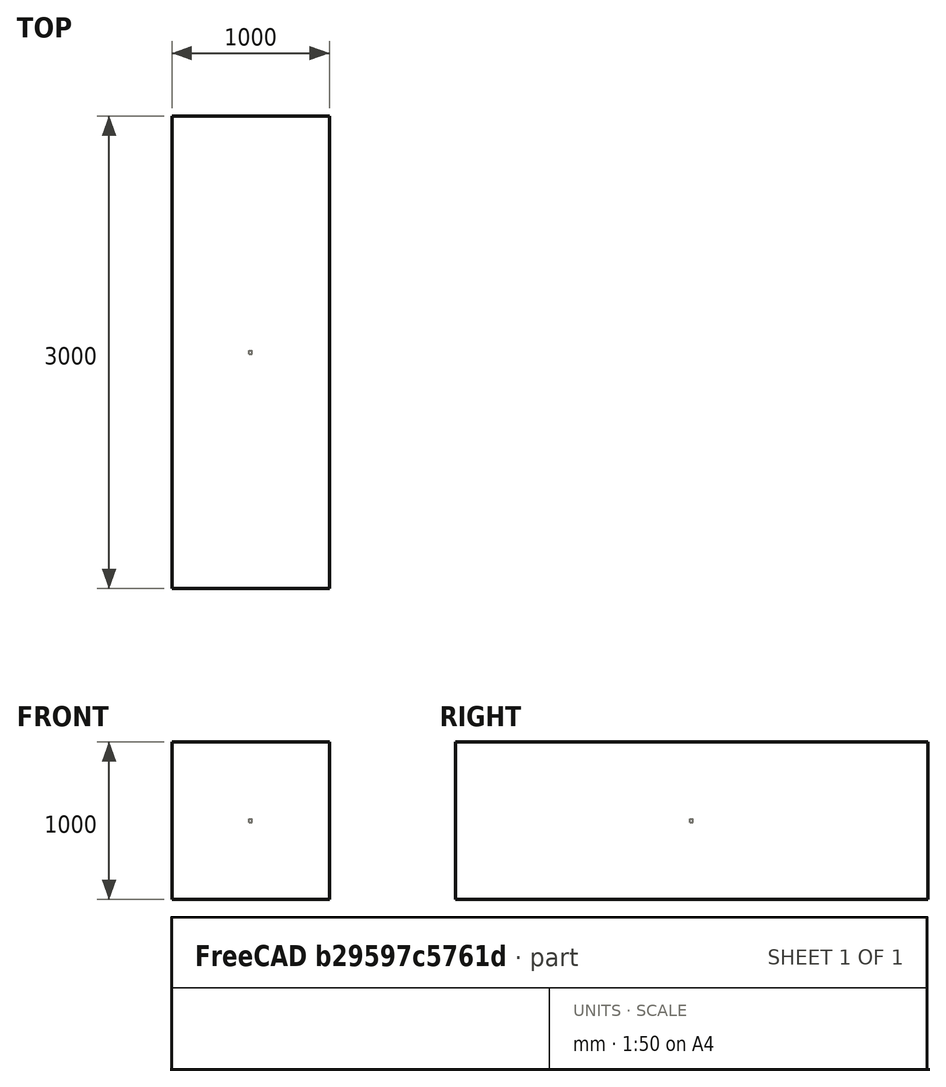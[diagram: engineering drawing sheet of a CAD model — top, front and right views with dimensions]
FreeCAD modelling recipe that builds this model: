
FCSTD DOCUMENT  (FreeCAD 1.0R39109 (Git))
Label: BeamDumpGDML
License: All rights reserved
LicenseURL: https://en.wikipedia.org/wiki/All_rights_reserved
objects: App::DocumentObjectGroupPython×1252, Part::FeaturePython×3, App::Part×3, Spreadsheet::Sheet×2
note: 2 computed .brp shape members not serialized (recipe doc carries the construction recipe); baked Part::Feature solids carry a one-line shape summary decoded from their .brp

FEATURE [Spreadsheet::Sheet] defines
  cells = A1='constant; B1='HALFPI; C1(HALFPI)==pi / 2; A2='constant; B2='PI; C2(PI)==1 * pi; A3='constant; B3='TWOPI; C3(TWOPI)==2 * pi
FEATURE [Spreadsheet::Sheet] gdmlInfo
FEATURE [App::DocumentObjectGroupPython] Define  # scripted group (container) (typed FeaturePython)
  Group = -> [defines,gdmlInfo]
FEATURE [App::DocumentObjectGroupPython] HALFPI  # scripted group (container) (typed FeaturePython)
  name = HALFPI
  value = pi/2.
FEATURE [App::DocumentObjectGroupPython] PI  # scripted group (container) (typed FeaturePython)
  name = PI
  value = 1.*pi
FEATURE [App::DocumentObjectGroupPython] TWOPI  # scripted group (container) (typed FeaturePython)
  name = TWOPI
  value = 2.*pi
FEATURE [App::DocumentObjectGroupPython] Constants  # scripted group (container) (typed FeaturePython)
  Group = -> [HALFPI,PI,TWOPI]
FEATURE [App::DocumentObjectGroupPython] Quantities  # scripted group (container) (typed FeaturePython)
FEATURE [App::DocumentObjectGroupPython] Variables  # scripted group (container) (typed FeaturePython)
FEATURE [App::DocumentObjectGroupPython] Isotopes  # scripted group (container) (typed FeaturePython)
FEATURE [App::DocumentObjectGroupPython] Elements  # scripted group (container) (typed FeaturePython)
FEATURE [App::DocumentObjectGroupPython] Matrix  # scripted group (container) (typed FeaturePython)
FEATURE [App::DocumentObjectGroupPython] Surfaces  # scripted group (container) (typed FeaturePython)
FEATURE [App::DocumentObjectGroupPython] Opticals  # scripted group (container) (typed FeaturePython)
  Group = -> [Matrix,Surfaces]
FEATURE [App::DocumentObjectGroupPython] G4Isotopes  # scripted group (container) (typed FeaturePython)
FEATURE [App::DocumentObjectGroupPython] H_element  # scripted group (container) (typed FeaturePython)
  Z = 1
  atom_value = 1.008
  formula = H
  name = H_element
FEATURE [App::DocumentObjectGroupPython] He_element  # scripted group (container) (typed FeaturePython)
  Z = 2
  atom_value = 4.0026
  formula = He
  name = He_element
FEATURE [App::DocumentObjectGroupPython] Li_element  # scripted group (container) (typed FeaturePython)
  Z = 3
  atom_value = 6.94
  formula = Li
  name = Li_element
FEATURE [App::DocumentObjectGroupPython] Be_element  # scripted group (container) (typed FeaturePython)
  Z = 4
  atom_value = 9.01218
  formula = Be
  name = Be_element
FEATURE [App::DocumentObjectGroupPython] B_element  # scripted group (container) (typed FeaturePython)
  Z = 5
  atom_value = 10.81
  formula = B
  name = B_element
FEATURE [App::DocumentObjectGroupPython] C_element  # scripted group (container) (typed FeaturePython)
  Z = 6
  atom_value = 12.011
  formula = C
  name = C_element
FEATURE [App::DocumentObjectGroupPython] N_element  # scripted group (container) (typed FeaturePython)
  Z = 7
  atom_value = 14.007
  formula = N
  name = N_element
FEATURE [App::DocumentObjectGroupPython] O_element  # scripted group (container) (typed FeaturePython)
  Z = 8
  atom_value = 15.999
  formula = O
  name = O_element
FEATURE [App::DocumentObjectGroupPython] F_element  # scripted group (container) (typed FeaturePython)
  Z = 9
  atom_value = 18.9984
  formula = F
  name = F_element
FEATURE [App::DocumentObjectGroupPython] Ne_element  # scripted group (container) (typed FeaturePython)
  Z = 10
  atom_value = 20.1797
  formula = Ne
  name = Ne_element
FEATURE [App::DocumentObjectGroupPython] Na_element  # scripted group (container) (typed FeaturePython)
  Z = 11
  atom_value = 22.9898
  formula = Na
  name = Na_element
FEATURE [App::DocumentObjectGroupPython] Mg_element  # scripted group (container) (typed FeaturePython)
  Z = 12
  atom_value = 24.305
  formula = Mg
  name = Mg_element
FEATURE [App::DocumentObjectGroupPython] Al_element  # scripted group (container) (typed FeaturePython)
  Z = 13
  atom_value = 26.9815
  formula = Al
  name = Al_element
FEATURE [App::DocumentObjectGroupPython] Si_element  # scripted group (container) (typed FeaturePython)
  Z = 14
  atom_value = 28.085
  formula = Si
  name = Si_element
FEATURE [App::DocumentObjectGroupPython] P_element  # scripted group (container) (typed FeaturePython)
  Z = 15
  atom_value = 30.9738
  formula = P
  name = P_element
FEATURE [App::DocumentObjectGroupPython] S_element  # scripted group (container) (typed FeaturePython)
  Z = 16
  atom_value = 32.06
  formula = S
  name = S_element
FEATURE [App::DocumentObjectGroupPython] Cl_element  # scripted group (container) (typed FeaturePython)
  Z = 17
  atom_value = 35.45
  formula = Cl
  name = Cl_element
FEATURE [App::DocumentObjectGroupPython] Ar_element  # scripted group (container) (typed FeaturePython)
  Z = 18
  atom_value = 39.95
  formula = Ar
  name = Ar_element
FEATURE [App::DocumentObjectGroupPython] K_element  # scripted group (container) (typed FeaturePython)
  Z = 19
  atom_value = 39.0983
  formula = K
  name = K_element
FEATURE [App::DocumentObjectGroupPython] Ca_element  # scripted group (container) (typed FeaturePython)
  Z = 20
  atom_value = 40.078
  formula = Ca
  name = Ca_element
FEATURE [App::DocumentObjectGroupPython] Sc_element  # scripted group (container) (typed FeaturePython)
  Z = 21
  atom_value = 44.9559
  formula = Sc
  name = Sc_element
FEATURE [App::DocumentObjectGroupPython] Ti_element  # scripted group (container) (typed FeaturePython)
  Z = 22
  atom_value = 47.867
  formula = Ti
  name = Ti_element
FEATURE [App::DocumentObjectGroupPython] V_element  # scripted group (container) (typed FeaturePython)
  Z = 23
  atom_value = 50.9415
  formula = V
  name = V_element
FEATURE [App::DocumentObjectGroupPython] Cr_element  # scripted group (container) (typed FeaturePython)
  Z = 24
  atom_value = 51.9961
  formula = Cr
  name = Cr_element
FEATURE [App::DocumentObjectGroupPython] Mn_element  # scripted group (container) (typed FeaturePython)
  Z = 25
  atom_value = 54.938
  formula = Mn
  name = Mn_element
FEATURE [App::DocumentObjectGroupPython] Fe_element  # scripted group (container) (typed FeaturePython)
  Z = 26
  atom_value = 55.845
  formula = Fe
  name = Fe_element
FEATURE [App::DocumentObjectGroupPython] Co_element  # scripted group (container) (typed FeaturePython)
  Z = 27
  atom_value = 58.9332
  formula = Co
  name = Co_element
FEATURE [App::DocumentObjectGroupPython] Ni_element  # scripted group (container) (typed FeaturePython)
  Z = 28
  atom_value = 58.6934
  formula = Ni
  name = Ni_element
FEATURE [App::DocumentObjectGroupPython] Cu_element  # scripted group (container) (typed FeaturePython)
  Z = 29
  atom_value = 63.546
  formula = Cu
  name = Cu_element
FEATURE [App::DocumentObjectGroupPython] Zn_element  # scripted group (container) (typed FeaturePython)
  Z = 30
  atom_value = 65.38
  formula = Zn
  name = Zn_element
FEATURE [App::DocumentObjectGroupPython] Ga_element  # scripted group (container) (typed FeaturePython)
  Z = 31
  atom_value = 69.723
  formula = Ga
  name = Ga_element
FEATURE [App::DocumentObjectGroupPython] Ge_element  # scripted group (container) (typed FeaturePython)
  Z = 32
  atom_value = 72.63
  formula = Ge
  name = Ge_element
FEATURE [App::DocumentObjectGroupPython] As_element  # scripted group (container) (typed FeaturePython)
  Z = 33
  atom_value = 74.9216
  formula = As
  name = As_element
FEATURE [App::DocumentObjectGroupPython] Se_element  # scripted group (container) (typed FeaturePython)
  Z = 34
  atom_value = 78.971
  formula = Se
  name = Se_element
FEATURE [App::DocumentObjectGroupPython] Br_element  # scripted group (container) (typed FeaturePython)
  Z = 35
  atom_value = 79.904
  formula = Br
  name = Br_element
FEATURE [App::DocumentObjectGroupPython] Kr_element  # scripted group (container) (typed FeaturePython)
  Z = 36
  atom_value = 83.798
  formula = Kr
  name = Kr_element
FEATURE [App::DocumentObjectGroupPython] Rb_element  # scripted group (container) (typed FeaturePython)
  Z = 37
  atom_value = 85.4678
  formula = Rb
  name = Rb_element
FEATURE [App::DocumentObjectGroupPython] Sr_element  # scripted group (container) (typed FeaturePython)
  Z = 38
  atom_value = 87.62
  formula = Sr
  name = Sr_element
FEATURE [App::DocumentObjectGroupPython] Y_element  # scripted group (container) (typed FeaturePython)
  Z = 39
  atom_value = 88.9058
  formula = Y
  name = Y_element
FEATURE [App::DocumentObjectGroupPython] Zr_element  # scripted group (container) (typed FeaturePython)
  Z = 40
  atom_value = 91.224
  formula = Zr
  name = Zr_element
FEATURE [App::DocumentObjectGroupPython] Nb_element  # scripted group (container) (typed FeaturePython)
  Z = 41
  atom_value = 92.9064
  formula = Nb
  name = Nb_element
FEATURE [App::DocumentObjectGroupPython] Mo_element  # scripted group (container) (typed FeaturePython)
  Z = 42
  atom_value = 95.95
  formula = Mo
  name = Mo_element
FEATURE [App::DocumentObjectGroupPython] Tc_element  # scripted group (container) (typed FeaturePython)
  Z = 43
  atom_value = 97
  formula = Tc
  name = Tc_element
FEATURE [App::DocumentObjectGroupPython] Ru_element  # scripted group (container) (typed FeaturePython)
  Z = 44
  atom_value = 101.07
  formula = Ru
  name = Ru_element
FEATURE [App::DocumentObjectGroupPython] Rh_element  # scripted group (container) (typed FeaturePython)
  Z = 45
  atom_value = 102.905
  formula = Rh
  name = Rh_element
FEATURE [App::DocumentObjectGroupPython] Pd_element  # scripted group (container) (typed FeaturePython)
  Z = 46
  atom_value = 106.42
  formula = Pd
  name = Pd_element
FEATURE [App::DocumentObjectGroupPython] Ag_element  # scripted group (container) (typed FeaturePython)
  Z = 47
  atom_value = 107.868
  formula = Ag
  name = Ag_element
FEATURE [App::DocumentObjectGroupPython] Cd_element  # scripted group (container) (typed FeaturePython)
  Z = 48
  atom_value = 112.414
  formula = Cd
  name = Cd_element
FEATURE [App::DocumentObjectGroupPython] In_element  # scripted group (container) (typed FeaturePython)
  Z = 49
  atom_value = 114.818
  formula = In
  name = In_element
FEATURE [App::DocumentObjectGroupPython] Sn_element  # scripted group (container) (typed FeaturePython)
  Z = 50
  atom_value = 118.71
  formula = Sn
  name = Sn_element
FEATURE [App::DocumentObjectGroupPython] Sb_element  # scripted group (container) (typed FeaturePython)
  Z = 51
  atom_value = 121.76
  formula = Sb
  name = Sb_element
FEATURE [App::DocumentObjectGroupPython] Te_element  # scripted group (container) (typed FeaturePython)
  Z = 52
  atom_value = 127.6
  formula = Te
  name = Te_element
FEATURE [App::DocumentObjectGroupPython] I_element  # scripted group (container) (typed FeaturePython)
  Z = 53
  atom_value = 126.904
  formula = I
  name = I_element
FEATURE [App::DocumentObjectGroupPython] Xe_element  # scripted group (container) (typed FeaturePython)
  Z = 54
  atom_value = 131.293
  formula = Xe
  name = Xe_element
FEATURE [App::DocumentObjectGroupPython] Cs_element  # scripted group (container) (typed FeaturePython)
  Z = 55
  atom_value = 132.905
  formula = Cs
  name = Cs_element
FEATURE [App::DocumentObjectGroupPython] Ba_element  # scripted group (container) (typed FeaturePython)
  Z = 56
  atom_value = 137.327
  formula = Ba
  name = Ba_element
FEATURE [App::DocumentObjectGroupPython] La_element  # scripted group (container) (typed FeaturePython)
  Z = 57
  atom_value = 138.905
  formula = La
  name = La_element
FEATURE [App::DocumentObjectGroupPython] Ce_element  # scripted group (container) (typed FeaturePython)
  Z = 58
  atom_value = 140.116
  formula = Ce
  name = Ce_element
FEATURE [App::DocumentObjectGroupPython] Pr_element  # scripted group (container) (typed FeaturePython)
  Z = 59
  atom_value = 140.908
  formula = Pr
  name = Pr_element
FEATURE [App::DocumentObjectGroupPython] Nd_element  # scripted group (container) (typed FeaturePython)
  Z = 60
  atom_value = 144.242
  formula = Nd
  name = Nd_element
FEATURE [App::DocumentObjectGroupPython] Pm_element  # scripted group (container) (typed FeaturePython)
  Z = 61
  atom_value = 145
  formula = Pm
  name = Pm_element
FEATURE [App::DocumentObjectGroupPython] Sm_element  # scripted group (container) (typed FeaturePython)
  Z = 62
  atom_value = 150.36
  formula = Sm
  name = Sm_element
FEATURE [App::DocumentObjectGroupPython] Eu_element  # scripted group (container) (typed FeaturePython)
  Z = 63
  atom_value = 151.964
  formula = Eu
  name = Eu_element
FEATURE [App::DocumentObjectGroupPython] Gd_element  # scripted group (container) (typed FeaturePython)
  Z = 64
  atom_value = 157.25
  formula = Gd
  name = Gd_element
FEATURE [App::DocumentObjectGroupPython] Tb_element  # scripted group (container) (typed FeaturePython)
  Z = 65
  atom_value = 158.925
  formula = Tb
  name = Tb_element
FEATURE [App::DocumentObjectGroupPython] Dy_element  # scripted group (container) (typed FeaturePython)
  Z = 66
  atom_value = 162.5
  formula = Dy
  name = Dy_element
FEATURE [App::DocumentObjectGroupPython] Ho_element  # scripted group (container) (typed FeaturePython)
  Z = 67
  atom_value = 164.93
  formula = Ho
  name = Ho_element
FEATURE [App::DocumentObjectGroupPython] Er_element  # scripted group (container) (typed FeaturePython)
  Z = 68
  atom_value = 167.259
  formula = Er
  name = Er_element
FEATURE [App::DocumentObjectGroupPython] Tm_element  # scripted group (container) (typed FeaturePython)
  Z = 69
  atom_value = 168.934
  formula = Tm
  name = Tm_element
FEATURE [App::DocumentObjectGroupPython] Yb_element  # scripted group (container) (typed FeaturePython)
  Z = 70
  atom_value = 173.045
  formula = Yb
  name = Yb_element
FEATURE [App::DocumentObjectGroupPython] Lu_element  # scripted group (container) (typed FeaturePython)
  Z = 71
  atom_value = 174.967
  formula = Lu
  name = Lu_element
FEATURE [App::DocumentObjectGroupPython] Hf_element  # scripted group (container) (typed FeaturePython)
  Z = 72
  atom_value = 178.49
  formula = Hf
  name = Hf_element
FEATURE [App::DocumentObjectGroupPython] Ta_element  # scripted group (container) (typed FeaturePython)
  Z = 73
  atom_value = 180.948
  formula = Ta
  name = Ta_element
FEATURE [App::DocumentObjectGroupPython] W_element  # scripted group (container) (typed FeaturePython)
  Z = 74
  atom_value = 183.84
  formula = W
  name = W_element
FEATURE [App::DocumentObjectGroupPython] Re_element  # scripted group (container) (typed FeaturePython)
  Z = 75
  atom_value = 186.207
  formula = Re
  name = Re_element
FEATURE [App::DocumentObjectGroupPython] Os_element  # scripted group (container) (typed FeaturePython)
  Z = 76
  atom_value = 190.23
  formula = Os
  name = Os_element
FEATURE [App::DocumentObjectGroupPython] Ir_element  # scripted group (container) (typed FeaturePython)
  Z = 77
  atom_value = 192.217
  formula = Ir
  name = Ir_element
FEATURE [App::DocumentObjectGroupPython] Pt_element  # scripted group (container) (typed FeaturePython)
  Z = 78
  atom_value = 195.084
  formula = Pt
  name = Pt_element
FEATURE [App::DocumentObjectGroupPython] Au_element  # scripted group (container) (typed FeaturePython)
  Z = 79
  atom_value = 196.967
  formula = Au
  name = Au_element
FEATURE [App::DocumentObjectGroupPython] Hg_element  # scripted group (container) (typed FeaturePython)
  Z = 80
  atom_value = 200.592
  formula = Hg
  name = Hg_element
FEATURE [App::DocumentObjectGroupPython] Tl_element  # scripted group (container) (typed FeaturePython)
  Z = 81
  atom_value = 204.38
  formula = Tl
  name = Tl_element
FEATURE [App::DocumentObjectGroupPython] Pb_element  # scripted group (container) (typed FeaturePython)
  Z = 82
  atom_value = 207.2
  formula = Pb
  name = Pb_element
FEATURE [App::DocumentObjectGroupPython] Bi_element  # scripted group (container) (typed FeaturePython)
  Z = 83
  atom_value = 208.98
  formula = Bi
  name = Bi_element
FEATURE [App::DocumentObjectGroupPython] Po_element  # scripted group (container) (typed FeaturePython)
  Z = 84
  atom_value = 209
  formula = Po
  name = Po_element
FEATURE [App::DocumentObjectGroupPython] At_element  # scripted group (container) (typed FeaturePython)
  Z = 85
  atom_value = 210
  formula = At
  name = At_element
FEATURE [App::DocumentObjectGroupPython] Rn_element  # scripted group (container) (typed FeaturePython)
  Z = 86
  atom_value = 222
  formula = Rn
  name = Rn_element
FEATURE [App::DocumentObjectGroupPython] Fr_element  # scripted group (container) (typed FeaturePython)
  Z = 87
  atom_value = 223
  formula = Fr
  name = Fr_element
FEATURE [App::DocumentObjectGroupPython] Ra_element  # scripted group (container) (typed FeaturePython)
  Z = 88
  atom_value = 226
  formula = Ra
  name = Ra_element
FEATURE [App::DocumentObjectGroupPython] Ac_element  # scripted group (container) (typed FeaturePython)
  Z = 89
  atom_value = 227
  formula = Ac
  name = Ac_element
FEATURE [App::DocumentObjectGroupPython] Th_element  # scripted group (container) (typed FeaturePython)
  Z = 90
  atom_value = 232.038
  formula = Th
  name = Th_element
FEATURE [App::DocumentObjectGroupPython] Pa_element  # scripted group (container) (typed FeaturePython)
  Z = 91
  atom_value = 231.036
  formula = Pa
  name = Pa_element
FEATURE [App::DocumentObjectGroupPython] U_element  # scripted group (container) (typed FeaturePython)
  Z = 92
  atom_value = 238.029
  formula = U
  name = U_element
FEATURE [App::DocumentObjectGroupPython] Np_element  # scripted group (container) (typed FeaturePython)
  Z = 93
  atom_value = 237
  formula = Np
  name = Np_element
FEATURE [App::DocumentObjectGroupPython] Pu_element  # scripted group (container) (typed FeaturePython)
  Z = 94
  atom_value = 244
  formula = Pu
  name = Pu_element
FEATURE [App::DocumentObjectGroupPython] Am_element  # scripted group (container) (typed FeaturePython)
  Z = 95
  atom_value = 243
  formula = Am
  name = Am_element
FEATURE [App::DocumentObjectGroupPython] Cm_element  # scripted group (container) (typed FeaturePython)
  Z = 96
  atom_value = 247
  formula = Cm
  name = Cm_element
FEATURE [App::DocumentObjectGroupPython] Bk_element  # scripted group (container) (typed FeaturePython)
  Z = 97
  atom_value = 247
  formula = Bk
  name = Bk_element
FEATURE [App::DocumentObjectGroupPython] Cf_element  # scripted group (container) (typed FeaturePython)
  Z = 98
  atom_value = 251
  formula = Cf
  name = Cf_element
FEATURE [App::DocumentObjectGroupPython] G4Elements  # scripted group (container) (typed FeaturePython)
  Group = -> [H_element,He_element,Li_element,Be_element,B_element,C_element,N_element,O_element,F_element,Ne_element,Na_element,Mg_element,Al_element,Si_element,P_element,S_element,Cl_element,Ar_element,K_element,Ca_element,Sc_element,Ti_element,V_element,Cr_element,Mn_element,Fe_element,Co_element,Ni_element,Cu_element,Zn_element,Ga_element,Ge_element,As_element,Se_element,Br_element,Kr_element,Rb_element,+61 more]
FEATURE [App::DocumentObjectGroupPython] H_element001  label="H_element : 0.101"  # scripted group (container) (typed FeaturePython)
  n = 0.101327
FEATURE [App::DocumentObjectGroupPython] C_element001  label="C_element : 0.775"  # scripted group (container) (typed FeaturePython)
  n = 0.7755
FEATURE [App::DocumentObjectGroupPython] N_element001  label="N_element : 0.035"  # scripted group (container) (typed FeaturePython)
  n = 0.035057
FEATURE [App::DocumentObjectGroupPython] O_element001  label="O_element : 0.052"  # scripted group (container) (typed FeaturePython)
  n = 0.0523159
FEATURE [App::DocumentObjectGroupPython] F_element001  label="F_element : 0.017"  # scripted group (container) (typed FeaturePython)
  n = 0.017422
FEATURE [App::DocumentObjectGroupPython] Ca_element001  label="Ca_element : 0.018"  # scripted group (container) (typed FeaturePython)
  n = 0.018378
FEATURE [App::DocumentObjectGroupPython] G4_A_150_TISSUE  label="G4_A-150_TISSUE"  # scripted group (container) (typed FeaturePython)
  Dunit = g/cm3
  Dvalue = 1.127
  Group = -> [H_element001,C_element001,N_element001,O_element001,F_element001,Ca_element001]
  conduct = 2
  density = 1
  expand = 3
  formula = G4_A-150_TISSUE
  name = G4_A-150_TISSUE
  specific = 4
FEATURE [App::DocumentObjectGroupPython] C_element002  label="C_element : 3"  # scripted group (container) (typed FeaturePython)
  n = 3
  ref = C_element
FEATURE [App::DocumentObjectGroupPython] H_element002  label="H_element : 6"  # scripted group (container) (typed FeaturePython)
  n = 6
  ref = H_element
FEATURE [App::DocumentObjectGroupPython] O_element002  label="O_element : 1"  # scripted group (container) (typed FeaturePython)
  n = 1
  ref = O_element
FEATURE [App::DocumentObjectGroupPython] G4_ACETONE  # scripted group (container) (typed FeaturePython)
  Dunit = g/cm3
  Dvalue = 0.7899
  Group = -> [C_element002,H_element002,O_element002]
  conduct = 2
  density = 1
  expand = 3
  formula = G4_ACETONE
  name = G4_ACETONE
  specific = 4
FEATURE [App::DocumentObjectGroupPython] C_element003  label="C_element : 2"  # scripted group (container) (typed FeaturePython)
  n = 2
  ref = C_element
FEATURE [App::DocumentObjectGroupPython] H_element003  label="H_element : 2"  # scripted group (container) (typed FeaturePython)
  n = 2
  ref = H_element
FEATURE [App::DocumentObjectGroupPython] G4_ACETYLENE  # scripted group (container) (typed FeaturePython)
  Dunit = g/cm3
  Dvalue = 0.0010967
  Group = -> [C_element003,H_element003]
  conduct = 2
  density = 1
  expand = 3
  formula = G4_ACETYLENE
  name = G4_ACETYLENE
  specific = 4
FEATURE [App::DocumentObjectGroupPython] C_element004  label="C_element : 5"  # scripted group (container) (typed FeaturePython)
  n = 5
  ref = C_element
FEATURE [App::DocumentObjectGroupPython] H_element004  label="H_element : 5"  # scripted group (container) (typed FeaturePython)
  n = 5
  ref = H_element
FEATURE [App::DocumentObjectGroupPython] N_element002  label="N_element : 5"  # scripted group (container) (typed FeaturePython)
  n = 5
  ref = N_element
FEATURE [App::DocumentObjectGroupPython] G4_ADENINE  # scripted group (container) (typed FeaturePython)
  Dunit = g/cm3
  Dvalue = 1.6
  Group = -> [C_element004,H_element004,N_element002]
  conduct = 2
  density = 1
  expand = 3
  formula = G4_ADENINE
  name = G4_ADENINE
  specific = 4
FEATURE [App::DocumentObjectGroupPython] H_element005  label="H_element : 0.114"  # scripted group (container) (typed FeaturePython)
  n = 0.114
FEATURE [App::DocumentObjectGroupPython] C_element005  label="C_element : 0.598"  # scripted group (container) (typed FeaturePython)
  n = 0.598
FEATURE [App::DocumentObjectGroupPython] N_element003  label="N_element : 0.007"  # scripted group (container) (typed FeaturePython)
  n = 0.007
FEATURE [App::DocumentObjectGroupPython] O_element003  label="O_element : 0.278"  # scripted group (container) (typed FeaturePython)
  n = 0.278
FEATURE [App::DocumentObjectGroupPython] Na_element001  label="Na_element : 0.001"  # scripted group (container) (typed FeaturePython)
  n = 0.001
FEATURE [App::DocumentObjectGroupPython] S_element001  label="S_element : 0.001"  # scripted group (container) (typed FeaturePython)
  n = 0.001
FEATURE [App::DocumentObjectGroupPython] Cl_element001  label="Cl_element : 0.001"  # scripted group (container) (typed FeaturePython)
  n = 0.001
FEATURE [App::DocumentObjectGroupPython] G4_ADIPOSE_TISSUE_ICRP  # scripted group (container) (typed FeaturePython)
  Dunit = g/cm3
  Dvalue = 0.95
  Group = -> [H_element005,C_element005,N_element003,O_element003,Na_element001,S_element001,Cl_element001]
  conduct = 2
  density = 1
  expand = 3
  formula = G4_ADIPOSE_TISSUE_ICRP
  name = G4_ADIPOSE_TISSUE_ICRP
  specific = 4
FEATURE [App::DocumentObjectGroupPython] C_element006  label="C_element : 0.000"  # scripted group (container) (typed FeaturePython)
  n = 0.000124
FEATURE [App::DocumentObjectGroupPython] N_element004  label="N_element : 0.755"  # scripted group (container) (typed FeaturePython)
  n = 0.755268
FEATURE [App::DocumentObjectGroupPython] O_element004  label="O_element : 0.232"  # scripted group (container) (typed FeaturePython)
  n = 0.231781
FEATURE [App::DocumentObjectGroupPython] Ar_element001  label="Ar_element : 0.013"  # scripted group (container) (typed FeaturePython)
  n = 0.012827
FEATURE [App::DocumentObjectGroupPython] G4_AIR  # scripted group (container) (typed FeaturePython)
  Dunit = g/cm3
  Dvalue = 0.00120479
  Group = -> [C_element006,N_element004,O_element004,Ar_element001]
  conduct = 2
  density = 1
  expand = 3
  formula = G4_AIR
  name = G4_AIR
  specific = 4
FEATURE [App::DocumentObjectGroupPython] C_element007  label="C_element : 006"  # scripted group (container) (typed FeaturePython)
  n = 3
  ref = C_element
FEATURE [App::DocumentObjectGroupPython] H_element006  label="H_element : 7"  # scripted group (container) (typed FeaturePython)
  n = 7
  ref = H_element
FEATURE [App::DocumentObjectGroupPython] N_element005  label="N_element : 1"  # scripted group (container) (typed FeaturePython)
  n = 1
  ref = N_element
FEATURE [App::DocumentObjectGroupPython] O_element005  label="O_element : 2"  # scripted group (container) (typed FeaturePython)
  n = 2
  ref = O_element
FEATURE [App::DocumentObjectGroupPython] G4_ALANINE  # scripted group (container) (typed FeaturePython)
  Dunit = g/cm3
  Dvalue = 1.42
  Group = -> [C_element007,H_element006,N_element005,O_element005]
  conduct = 2
  density = 1
  expand = 3
  formula = G4_ALANINE
  name = G4_ALANINE
  specific = 4
FEATURE [App::DocumentObjectGroupPython] Al_element001  label="Al_element : 2"  # scripted group (container) (typed FeaturePython)
  n = 2
  ref = Al_element
FEATURE [App::DocumentObjectGroupPython] O_element006  label="O_element : 3"  # scripted group (container) (typed FeaturePython)
  n = 3
  ref = O_element
FEATURE [App::DocumentObjectGroupPython] G4_ALUMINUM_OXIDE  # scripted group (container) (typed FeaturePython)
  Dunit = g/cm3
  Dvalue = 3.97
  Group = -> [Al_element001,O_element006]
  conduct = 2
  density = 1
  expand = 3
  formula = G4_ALUMINUM_OXIDE
  name = G4_ALUMINUM_OXIDE
  specific = 4
FEATURE [App::DocumentObjectGroupPython] H_element007  label="H_element : 0.106"  # scripted group (container) (typed FeaturePython)
  n = 0.10593
FEATURE [App::DocumentObjectGroupPython] C_element008  label="C_element : 0.789"  # scripted group (container) (typed FeaturePython)
  n = 0.788974
FEATURE [App::DocumentObjectGroupPython] O_element007  label="O_element : 0.105"  # scripted group (container) (typed FeaturePython)
  n = 0.105096
FEATURE [App::DocumentObjectGroupPython] G4_AMBER  # scripted group (container) (typed FeaturePython)
  Dunit = g/cm3
  Dvalue = 1.1
  Group = -> [H_element007,C_element008,O_element007]
  conduct = 2
  density = 1
  expand = 3
  formula = G4_AMBER
  name = G4_AMBER
  specific = 4
FEATURE [App::DocumentObjectGroupPython] N_element006  label="N_element : 006"  # scripted group (container) (typed FeaturePython)
  n = 1
  ref = N_element
FEATURE [App::DocumentObjectGroupPython] H_element008  label="H_element : 3"  # scripted group (container) (typed FeaturePython)
  n = 3
  ref = H_element
FEATURE [App::DocumentObjectGroupPython] G4_AMMONIA  # scripted group (container) (typed FeaturePython)
  Dunit = g/cm3
  Dvalue = 0.000826019
  Group = -> [N_element006,H_element008]
  conduct = 2
  density = 1
  expand = 3
  formula = G4_AMMONIA
  name = G4_AMMONIA
  specific = 4
FEATURE [App::DocumentObjectGroupPython] C_element009  label="C_element : 6"  # scripted group (container) (typed FeaturePython)
  n = 6
  ref = C_element
FEATURE [App::DocumentObjectGroupPython] H_element009  label="H_element : 008"  # scripted group (container) (typed FeaturePython)
  n = 7
  ref = H_element
FEATURE [App::DocumentObjectGroupPython] N_element007  label="N_element : 007"  # scripted group (container) (typed FeaturePython)
  n = 1
  ref = N_element
FEATURE [App::DocumentObjectGroupPython] G4_ANILINE  # scripted group (container) (typed FeaturePython)
  Dunit = g/cm3
  Dvalue = 1.0235
  Group = -> [C_element009,H_element009,N_element007]
  conduct = 2
  density = 1
  expand = 3
  formula = G4_ANILINE
  name = G4_ANILINE
  specific = 4
FEATURE [App::DocumentObjectGroupPython] C_element010  label="C_element : 14"  # scripted group (container) (typed FeaturePython)
  n = 14
  ref = C_element
FEATURE [App::DocumentObjectGroupPython] H_element010  label="H_element : 10"  # scripted group (container) (typed FeaturePython)
  n = 10
  ref = H_element
FEATURE [App::DocumentObjectGroupPython] G4_ANTHRACENE  # scripted group (container) (typed FeaturePython)
  Dunit = g/cm3
  Dvalue = 1.283
  Group = -> [C_element010,H_element010]
  conduct = 2
  density = 1
  expand = 3
  formula = G4_ANTHRACENE
  name = G4_ANTHRACENE
  specific = 4
FEATURE [App::DocumentObjectGroupPython] H_element011  label="H_element : 0.065"  # scripted group (container) (typed FeaturePython)
  n = 0.0654709
FEATURE [App::DocumentObjectGroupPython] C_element011  label="C_element : 0.537"  # scripted group (container) (typed FeaturePython)
  n = 0.536944
FEATURE [App::DocumentObjectGroupPython] N_element008  label="N_element : 0.021"  # scripted group (container) (typed FeaturePython)
  n = 0.0215
FEATURE [App::DocumentObjectGroupPython] O_element008  label="O_element : 0.032"  # scripted group (container) (typed FeaturePython)
  n = 0.032085
FEATURE [App::DocumentObjectGroupPython] F_element002  label="F_element : 0.167"  # scripted group (container) (typed FeaturePython)
  n = 0.167411
FEATURE [App::DocumentObjectGroupPython] Ca_element002  label="Ca_element : 0.177"  # scripted group (container) (typed FeaturePython)
  n = 0.176589
FEATURE [App::DocumentObjectGroupPython] G4_B_100_BONE  label="G4_B-100_BONE"  # scripted group (container) (typed FeaturePython)
  Dunit = g/cm3
  Dvalue = 1.45
  Group = -> [H_element011,C_element011,N_element008,O_element008,F_element002,Ca_element002]
  conduct = 2
  density = 1
  expand = 3
  formula = G4_B-100_BONE
  name = G4_B-100_BONE
  specific = 4
FEATURE [App::DocumentObjectGroupPython] H_element012  label="H_element : 0.057"  # scripted group (container) (typed FeaturePython)
  n = 0.057441
FEATURE [App::DocumentObjectGroupPython] C_element012  label="C_element : 0.790"  # scripted group (container) (typed FeaturePython)
  n = 0.774591
FEATURE [App::DocumentObjectGroupPython] O_element009  label="O_element : 0.168"  # scripted group (container) (typed FeaturePython)
  n = 0.167968
FEATURE [App::DocumentObjectGroupPython] G4_BAKELITE  # scripted group (container) (typed FeaturePython)
  Dunit = g/cm3
  Dvalue = 1.25
  Group = -> [H_element012,C_element012,O_element009]
  conduct = 2
  density = 1
  expand = 3
  formula = G4_BAKELITE
  name = G4_BAKELITE
  specific = 4
FEATURE [App::DocumentObjectGroupPython] Ba_element001  label="Ba_element : 1"  # scripted group (container) (typed FeaturePython)
  n = 1
  ref = Ba_element
FEATURE [App::DocumentObjectGroupPython] F_element003  label="F_element : 2"  # scripted group (container) (typed FeaturePython)
  n = 2
  ref = F_element
FEATURE [App::DocumentObjectGroupPython] G4_BARIUM_FLUORIDE  # scripted group (container) (typed FeaturePython)
  Dunit = g/cm3
  Dvalue = 4.89
  Group = -> [Ba_element001,F_element003]
  conduct = 2
  density = 1
  expand = 3
  formula = G4_BARIUM_FLUORIDE
  name = G4_BARIUM_FLUORIDE
  specific = 4
FEATURE [App::DocumentObjectGroupPython] Ba_element002  label="Ba_element : 002"  # scripted group (container) (typed FeaturePython)
  n = 1
  ref = Ba_element
FEATURE [App::DocumentObjectGroupPython] S_element002  label="S_element : 1"  # scripted group (container) (typed FeaturePython)
  n = 1
  ref = S_element
FEATURE [App::DocumentObjectGroupPython] O_element010  label="O_element : 4"  # scripted group (container) (typed FeaturePython)
  n = 4
  ref = O_element
FEATURE [App::DocumentObjectGroupPython] G4_BARIUM_SULFATE  # scripted group (container) (typed FeaturePython)
  Dunit = g/cm3
  Dvalue = 4.5
  Group = -> [Ba_element002,S_element002,O_element010]
  conduct = 2
  density = 1
  expand = 3
  formula = G4_BARIUM_SULFATE
  name = G4_BARIUM_SULFATE
  specific = 4
FEATURE [App::DocumentObjectGroupPython] C_element013  label="C_element : 007"  # scripted group (container) (typed FeaturePython)
  n = 6
  ref = C_element
FEATURE [App::DocumentObjectGroupPython] H_element013  label="H_element : 009"  # scripted group (container) (typed FeaturePython)
  n = 6
  ref = H_element
FEATURE [App::DocumentObjectGroupPython] G4_BENZENE  # scripted group (container) (typed FeaturePython)
  Dunit = g/cm3
  Dvalue = 0.87865
  Group = -> [C_element013,H_element013]
  conduct = 2
  density = 1
  expand = 3
  formula = G4_BENZENE
  name = G4_BENZENE
  specific = 4
FEATURE [App::DocumentObjectGroupPython] Be_element001  label="Be_element : 1"  # scripted group (container) (typed FeaturePython)
  n = 1
  ref = Be_element
FEATURE [App::DocumentObjectGroupPython] O_element011  label="O_element : 005"  # scripted group (container) (typed FeaturePython)
  n = 1
  ref = O_element
FEATURE [App::DocumentObjectGroupPython] G4_BERYLLIUM_OXIDE  # scripted group (container) (typed FeaturePython)
  Dunit = g/cm3
  Dvalue = 3.01
  Group = -> [Be_element001,O_element011]
  conduct = 2
  density = 1
  expand = 3
  formula = G4_BERYLLIUM_OXIDE
  name = G4_BERYLLIUM_OXIDE
  specific = 4
FEATURE [App::DocumentObjectGroupPython] Bi_element001  label="Bi_element : 4"  # scripted group (container) (typed FeaturePython)
  n = 4
  ref = Bi_element
FEATURE [App::DocumentObjectGroupPython] Ge_element001  label="Ge_element : 3"  # scripted group (container) (typed FeaturePython)
  n = 3
  ref = Ge_element
FEATURE [App::DocumentObjectGroupPython] O_element012  label="O_element : 12"  # scripted group (container) (typed FeaturePython)
  n = 12
  ref = O_element
FEATURE [App::DocumentObjectGroupPython] G4_BGO  # scripted group (container) (typed FeaturePython)
  Dunit = g/cm3
  Dvalue = 7.13
  Group = -> [Bi_element001,Ge_element001,O_element012]
  conduct = 2
  density = 1
  expand = 3
  formula = G4_BGO
  name = G4_BGO
  specific = 4
FEATURE [App::DocumentObjectGroupPython] H_element014  label="H_element : 0.102"  # scripted group (container) (typed FeaturePython)
  n = 0.102
FEATURE [App::DocumentObjectGroupPython] C_element014  label="C_element : 0.110"  # scripted group (container) (typed FeaturePython)
  n = 0.11
FEATURE [App::DocumentObjectGroupPython] N_element009  label="N_element : 0.033"  # scripted group (container) (typed FeaturePython)
  n = 0.033
FEATURE [App::DocumentObjectGroupPython] O_element013  label="O_element : 0.745"  # scripted group (container) (typed FeaturePython)
  n = 0.745
FEATURE [App::DocumentObjectGroupPython] Na_element002  label="Na_element : 0.002"  # scripted group (container) (typed FeaturePython)
  n = 0.001
FEATURE [App::DocumentObjectGroupPython] P_element001  label="P_element : 0.001"  # scripted group (container) (typed FeaturePython)
  n = 0.001
FEATURE [App::DocumentObjectGroupPython] S_element003  label="S_element : 0.002"  # scripted group (container) (typed FeaturePython)
  n = 0.002
FEATURE [App::DocumentObjectGroupPython] Cl_element002  label="Cl_element : 0.003"  # scripted group (container) (typed FeaturePython)
  n = 0.003
FEATURE [App::DocumentObjectGroupPython] K_element001  label="K_element : 0.002"  # scripted group (container) (typed FeaturePython)
  n = 0.002
FEATURE [App::DocumentObjectGroupPython] Fe_element001  label="Fe_element : 0.001"  # scripted group (container) (typed FeaturePython)
  n = 0.001
FEATURE [App::DocumentObjectGroupPython] G4_BLOOD_ICRP  # scripted group (container) (typed FeaturePython)
  Dunit = g/cm3
  Dvalue = 1.06
  Group = -> [H_element014,C_element014,N_element009,O_element013,Na_element002,P_element001,S_element003,Cl_element002,K_element001,Fe_element001]
  conduct = 2
  density = 1
  expand = 3
  formula = G4_BLOOD_ICRP
  name = G4_BLOOD_ICRP
  specific = 4
FEATURE [App::DocumentObjectGroupPython] H_element015  label="H_element : 0.064"  # scripted group (container) (typed FeaturePython)
  n = 0.064
FEATURE [App::DocumentObjectGroupPython] C_element015  label="C_element : 0.278"  # scripted group (container) (typed FeaturePython)
  n = 0.278
FEATURE [App::DocumentObjectGroupPython] N_element010  label="N_element : 0.027"  # scripted group (container) (typed FeaturePython)
  n = 0.027
FEATURE [App::DocumentObjectGroupPython] O_element014  label="O_element : 0.410"  # scripted group (container) (typed FeaturePython)
  n = 0.41
FEATURE [App::DocumentObjectGroupPython] Mg_element001  label="Mg_element : 0.002"  # scripted group (container) (typed FeaturePython)
  n = 0.002
FEATURE [App::DocumentObjectGroupPython] P_element002  label="P_element : 0.070"  # scripted group (container) (typed FeaturePython)
  n = 0.07
FEATURE [App::DocumentObjectGroupPython] S_element004  label="S_element : 0.003"  # scripted group (container) (typed FeaturePython)
  n = 0.002
FEATURE [App::DocumentObjectGroupPython] Ca_element003  label="Ca_element : 0.147"  # scripted group (container) (typed FeaturePython)
  n = 0.147
FEATURE [App::DocumentObjectGroupPython] G4_BONE_COMPACT_ICRU  # scripted group (container) (typed FeaturePython)
  Dunit = g/cm3
  Dvalue = 1.85
  Group = -> [H_element015,C_element015,N_element010,O_element014,Mg_element001,P_element002,S_element004,Ca_element003]
  conduct = 2
  density = 1
  expand = 3
  formula = G4_BONE_COMPACT_ICRU
  name = G4_BONE_COMPACT_ICRU
  specific = 4
FEATURE [App::DocumentObjectGroupPython] H_element016  label="H_element : 0.034"  # scripted group (container) (typed FeaturePython)
  n = 0.034
FEATURE [App::DocumentObjectGroupPython] C_element016  label="C_element : 0.155"  # scripted group (container) (typed FeaturePython)
  n = 0.155
FEATURE [App::DocumentObjectGroupPython] N_element011  label="N_element : 0.042"  # scripted group (container) (typed FeaturePython)
  n = 0.042
FEATURE [App::DocumentObjectGroupPython] O_element015  label="O_element : 0.435"  # scripted group (container) (typed FeaturePython)
  n = 0.435
FEATURE [App::DocumentObjectGroupPython] Na_element003  label="Na_element : 0.003"  # scripted group (container) (typed FeaturePython)
  n = 0.001
FEATURE [App::DocumentObjectGroupPython] Mg_element002  label="Mg_element : 0.003"  # scripted group (container) (typed FeaturePython)
  n = 0.002
FEATURE [App::DocumentObjectGroupPython] P_element003  label="P_element : 0.103"  # scripted group (container) (typed FeaturePython)
  n = 0.103
FEATURE [App::DocumentObjectGroupPython] S_element005  label="S_element : 0.004"  # scripted group (container) (typed FeaturePython)
  n = 0.003
FEATURE [App::DocumentObjectGroupPython] Ca_element004  label="Ca_element : 0.225"  # scripted group (container) (typed FeaturePython)
  n = 0.225
FEATURE [App::DocumentObjectGroupPython] G4_BONE_CORTICAL_ICRP  # scripted group (container) (typed FeaturePython)
  Dunit = g/cm3
  Dvalue = 1.92
  Group = -> [H_element016,C_element016,N_element011,O_element015,Na_element003,Mg_element002,P_element003,S_element005,Ca_element004]
  conduct = 2
  density = 1
  expand = 3
  formula = G4_BONE_CORTICAL_ICRP
  name = G4_BONE_CORTICAL_ICRP
  specific = 4
FEATURE [App::DocumentObjectGroupPython] B_element001  label="B_element : 4"  # scripted group (container) (typed FeaturePython)
  n = 4
  ref = B_element
FEATURE [App::DocumentObjectGroupPython] C_element017  label="C_element : 1"  # scripted group (container) (typed FeaturePython)
  n = 1
  ref = C_element
FEATURE [App::DocumentObjectGroupPython] G4_BORON_CARBIDE  # scripted group (container) (typed FeaturePython)
  Dunit = g/cm3
  Dvalue = 2.52
  Group = -> [B_element001,C_element017]
  conduct = 2
  density = 1
  expand = 3
  formula = G4_BORON_CARBIDE
  name = G4_BORON_CARBIDE
  specific = 4
FEATURE [App::DocumentObjectGroupPython] B_element002  label="B_element : 2"  # scripted group (container) (typed FeaturePython)
  n = 2
  ref = B_element
FEATURE [App::DocumentObjectGroupPython] O_element016  label="O_element : 006"  # scripted group (container) (typed FeaturePython)
  n = 3
  ref = O_element
FEATURE [App::DocumentObjectGroupPython] G4_BORON_OXIDE  # scripted group (container) (typed FeaturePython)
  Dunit = g/cm3
  Dvalue = 1.812
  Group = -> [B_element002,O_element016]
  conduct = 2
  density = 1
  expand = 3
  formula = G4_BORON_OXIDE
  name = G4_BORON_OXIDE
  specific = 4
FEATURE [App::DocumentObjectGroupPython] H_element017  label="H_element : 0.107"  # scripted group (container) (typed FeaturePython)
  n = 0.107
FEATURE [App::DocumentObjectGroupPython] C_element018  label="C_element : 0.145"  # scripted group (container) (typed FeaturePython)
  n = 0.145
FEATURE [App::DocumentObjectGroupPython] N_element012  label="N_element : 0.022"  # scripted group (container) (typed FeaturePython)
  n = 0.022
FEATURE [App::DocumentObjectGroupPython] O_element017  label="O_element : 0.712"  # scripted group (container) (typed FeaturePython)
  n = 0.712
FEATURE [App::DocumentObjectGroupPython] Na_element004  label="Na_element : 0.004"  # scripted group (container) (typed FeaturePython)
  n = 0.002
FEATURE [App::DocumentObjectGroupPython] P_element004  label="P_element : 0.004"  # scripted group (container) (typed FeaturePython)
  n = 0.004
FEATURE [App::DocumentObjectGroupPython] S_element006  label="S_element : 0.005"  # scripted group (container) (typed FeaturePython)
  n = 0.002
FEATURE [App::DocumentObjectGroupPython] Cl_element003  label="Cl_element : 0.004"  # scripted group (container) (typed FeaturePython)
  n = 0.003
FEATURE [App::DocumentObjectGroupPython] K_element002  label="K_element : 0.003"  # scripted group (container) (typed FeaturePython)
  n = 0.003
FEATURE [App::DocumentObjectGroupPython] G4_BRAIN_ICRP  # scripted group (container) (typed FeaturePython)
  Dunit = g/cm3
  Dvalue = 1.04
  Group = -> [H_element017,C_element018,N_element012,O_element017,Na_element004,P_element004,S_element006,Cl_element003,K_element002]
  conduct = 2
  density = 1
  expand = 3
  formula = G4_BRAIN_ICRP
  name = G4_BRAIN_ICRP
  specific = 4
FEATURE [App::DocumentObjectGroupPython] C_element019  label="C_element : 4"  # scripted group (container) (typed FeaturePython)
  n = 4
  ref = C_element
FEATURE [App::DocumentObjectGroupPython] H_element018  label="H_element : 010"  # scripted group (container) (typed FeaturePython)
  n = 10
  ref = H_element
FEATURE [App::DocumentObjectGroupPython] G4_BUTANE  # scripted group (container) (typed FeaturePython)
  Dunit = g/cm3
  Dvalue = 0.00249343
  Group = -> [C_element019,H_element018]
  conduct = 2
  density = 1
  expand = 3
  formula = G4_BUTANE
  name = G4_BUTANE
  specific = 4
FEATURE [App::DocumentObjectGroupPython] C_element020  label="C_element : 008"  # scripted group (container) (typed FeaturePython)
  n = 4
  ref = C_element
FEATURE [App::DocumentObjectGroupPython] H_element019  label="H_element : 011"  # scripted group (container) (typed FeaturePython)
  n = 10
  ref = H_element
FEATURE [App::DocumentObjectGroupPython] O_element018  label="O_element : 007"  # scripted group (container) (typed FeaturePython)
  n = 1
  ref = O_element
FEATURE [App::DocumentObjectGroupPython] G4_N_BUTYL_ALCOHOL  label="G4_N-BUTYL_ALCOHOL"  # scripted group (container) (typed FeaturePython)
  Dunit = g/cm3
  Dvalue = 0.8098
  Group = -> [C_element020,H_element019,O_element018]
  conduct = 2
  density = 1
  expand = 3
  formula = G4_N-BUTYL_ALCOHOL
  name = G4_N-BUTYL_ALCOHOL
  specific = 4
FEATURE [App::DocumentObjectGroupPython] H_element020  label="H_element : 0.025"  # scripted group (container) (typed FeaturePython)
  n = 0.02468
FEATURE [App::DocumentObjectGroupPython] C_element021  label="C_element : 0.502"  # scripted group (container) (typed FeaturePython)
  n = 0.501611
FEATURE [App::DocumentObjectGroupPython] O_element019  label="O_element : 0.005"  # scripted group (container) (typed FeaturePython)
  n = 0.004527
FEATURE [App::DocumentObjectGroupPython] F_element004  label="F_element : 0.465"  # scripted group (container) (typed FeaturePython)
  n = 0.465209
FEATURE [App::DocumentObjectGroupPython] Si_element001  label="Si_element : 0.004"  # scripted group (container) (typed FeaturePython)
  n = 0.003973
FEATURE [App::DocumentObjectGroupPython] G4_C_552  label="G4_C-552"  # scripted group (container) (typed FeaturePython)
  Dunit = g/cm3
  Dvalue = 1.76
  Group = -> [H_element020,C_element021,O_element019,F_element004,Si_element001]
  conduct = 2
  density = 1
  expand = 3
  formula = G4_C-552
  name = G4_C-552
  specific = 4
FEATURE [App::DocumentObjectGroupPython] Cd_element001  label="Cd_element : 1"  # scripted group (container) (typed FeaturePython)
  n = 1
  ref = Cd_element
FEATURE [App::DocumentObjectGroupPython] Te_element001  label="Te_element : 1"  # scripted group (container) (typed FeaturePython)
  n = 1
  ref = Te_element
FEATURE [App::DocumentObjectGroupPython] G4_CADMIUM_TELLURIDE  # scripted group (container) (typed FeaturePython)
  Dunit = g/cm3
  Dvalue = 6.2
  Group = -> [Cd_element001,Te_element001]
  conduct = 2
  density = 1
  expand = 3
  formula = G4_CADMIUM_TELLURIDE
  name = G4_CADMIUM_TELLURIDE
  specific = 4
FEATURE [App::DocumentObjectGroupPython] Cd_element002  label="Cd_element : 002"  # scripted group (container) (typed FeaturePython)
  n = 1
  ref = Cd_element
FEATURE [App::DocumentObjectGroupPython] W_element001  label="W_element : 1"  # scripted group (container) (typed FeaturePython)
  n = 1
  ref = W_element
FEATURE [App::DocumentObjectGroupPython] O_element020  label="O_element : 008"  # scripted group (container) (typed FeaturePython)
  n = 4
  ref = O_element
FEATURE [App::DocumentObjectGroupPython] G4_CADMIUM_TUNGSTATE  # scripted group (container) (typed FeaturePython)
  Dunit = g/cm3
  Dvalue = 7.9
  Group = -> [Cd_element002,W_element001,O_element020]
  conduct = 2
  density = 1
  expand = 3
  formula = G4_CADMIUM_TUNGSTATE
  name = G4_CADMIUM_TUNGSTATE
  specific = 4
FEATURE [App::DocumentObjectGroupPython] Ca_element005  label="Ca_element : 1"  # scripted group (container) (typed FeaturePython)
  n = 1
  ref = Ca_element
FEATURE [App::DocumentObjectGroupPython] C_element022  label="C_element : 009"  # scripted group (container) (typed FeaturePython)
  n = 1
  ref = C_element
FEATURE [App::DocumentObjectGroupPython] O_element021  label="O_element : 009"  # scripted group (container) (typed FeaturePython)
  n = 3
  ref = O_element
FEATURE [App::DocumentObjectGroupPython] G4_CALCIUM_CARBONATE  # scripted group (container) (typed FeaturePython)
  Dunit = g/cm3
  Dvalue = 2.8
  Group = -> [Ca_element005,C_element022,O_element021]
  conduct = 2
  density = 1
  expand = 3
  formula = G4_CALCIUM_CARBONATE
  name = G4_CALCIUM_CARBONATE
  specific = 4
FEATURE [App::DocumentObjectGroupPython] Ca_element006  label="Ca_element : 002"  # scripted group (container) (typed FeaturePython)
  n = 1
  ref = Ca_element
FEATURE [App::DocumentObjectGroupPython] F_element005  label="F_element : 003"  # scripted group (container) (typed FeaturePython)
  n = 2
  ref = F_element
FEATURE [App::DocumentObjectGroupPython] G4_CALCIUM_FLUORIDE  # scripted group (container) (typed FeaturePython)
  Dunit = g/cm3
  Dvalue = 3.18
  Group = -> [Ca_element006,F_element005]
  conduct = 2
  density = 1
  expand = 3
  formula = G4_CALCIUM_FLUORIDE
  name = G4_CALCIUM_FLUORIDE
  specific = 4
FEATURE [App::DocumentObjectGroupPython] Ca_element007  label="Ca_element : 003"  # scripted group (container) (typed FeaturePython)
  n = 1
  ref = Ca_element
FEATURE [App::DocumentObjectGroupPython] O_element022  label="O_element : 010"  # scripted group (container) (typed FeaturePython)
  n = 1
  ref = O_element
FEATURE [App::DocumentObjectGroupPython] G4_CALCIUM_OXIDE  # scripted group (container) (typed FeaturePython)
  Dunit = g/cm3
  Dvalue = 3.3
  Group = -> [Ca_element007,O_element022]
  conduct = 2
  density = 1
  expand = 3
  formula = G4_CALCIUM_OXIDE
  name = G4_CALCIUM_OXIDE
  specific = 4
FEATURE [App::DocumentObjectGroupPython] Ca_element008  label="Ca_element : 004"  # scripted group (container) (typed FeaturePython)
  n = 1
  ref = Ca_element
FEATURE [App::DocumentObjectGroupPython] S_element007  label="S_element : 002"  # scripted group (container) (typed FeaturePython)
  n = 1
  ref = S_element
FEATURE [App::DocumentObjectGroupPython] O_element023  label="O_element : 011"  # scripted group (container) (typed FeaturePython)
  n = 4
  ref = O_element
FEATURE [App::DocumentObjectGroupPython] G4_CALCIUM_SULFATE  # scripted group (container) (typed FeaturePython)
  Dunit = g/cm3
  Dvalue = 2.96
  Group = -> [Ca_element008,S_element007,O_element023]
  conduct = 2
  density = 1
  expand = 3
  formula = G4_CALCIUM_SULFATE
  name = G4_CALCIUM_SULFATE
  specific = 4
FEATURE [App::DocumentObjectGroupPython] Ca_element009  label="Ca_element : 005"  # scripted group (container) (typed FeaturePython)
  n = 1
  ref = Ca_element
FEATURE [App::DocumentObjectGroupPython] W_element002  label="W_element : 002"  # scripted group (container) (typed FeaturePython)
  n = 1
  ref = W_element
FEATURE [App::DocumentObjectGroupPython] O_element024  label="O_element : 012"  # scripted group (container) (typed FeaturePython)
  n = 4
  ref = O_element
FEATURE [App::DocumentObjectGroupPython] G4_CALCIUM_TUNGSTATE  # scripted group (container) (typed FeaturePython)
  Dunit = g/cm3
  Dvalue = 6.062
  Group = -> [Ca_element009,W_element002,O_element024]
  conduct = 2
  density = 1
  expand = 3
  formula = G4_CALCIUM_TUNGSTATE
  name = G4_CALCIUM_TUNGSTATE
  specific = 4
FEATURE [App::DocumentObjectGroupPython] C_element023  label="C_element : 010"  # scripted group (container) (typed FeaturePython)
  n = 1
  ref = C_element
FEATURE [App::DocumentObjectGroupPython] O_element025  label="O_element : 013"  # scripted group (container) (typed FeaturePython)
  n = 2
  ref = O_element
FEATURE [App::DocumentObjectGroupPython] G4_CARBON_DIOXIDE  # scripted group (container) (typed FeaturePython)
  Dunit = g/cm3
  Dvalue = 0.00184212
  Group = -> [C_element023,O_element025]
  conduct = 2
  density = 1
  expand = 3
  formula = G4_CARBON_DIOXIDE
  name = G4_CARBON_DIOXIDE
  specific = 4
FEATURE [App::DocumentObjectGroupPython] C_element024  label="C_element : 011"  # scripted group (container) (typed FeaturePython)
  n = 1
  ref = C_element
FEATURE [App::DocumentObjectGroupPython] Cl_element004  label="Cl_element : 4"  # scripted group (container) (typed FeaturePython)
  n = 4
  ref = Cl_element
FEATURE [App::DocumentObjectGroupPython] G4_CARBON_TETRACHLORIDE  # scripted group (container) (typed FeaturePython)
  Dunit = g/cm3
  Dvalue = 1.594
  Group = -> [C_element024,Cl_element004]
  conduct = 2
  density = 1
  expand = 3
  formula = G4_CARBON_TETRACHLORIDE
  name = G4_CARBON_TETRACHLORIDE
  specific = 4
FEATURE [App::DocumentObjectGroupPython] C_element025  label="C_element : 012"  # scripted group (container) (typed FeaturePython)
  n = 6
  ref = C_element
FEATURE [App::DocumentObjectGroupPython] H_element021  label="H_element : 012"  # scripted group (container) (typed FeaturePython)
  n = 10
  ref = H_element
FEATURE [App::DocumentObjectGroupPython] O_element026  label="O_element : 5"  # scripted group (container) (typed FeaturePython)
  n = 5
  ref = O_element
FEATURE [App::DocumentObjectGroupPython] G4_CELLULOSE_CELLOPHANE  # scripted group (container) (typed FeaturePython)
  Dunit = g/cm3
  Dvalue = 1.42
  Group = -> [C_element025,H_element021,O_element026]
  conduct = 2
  density = 1
  expand = 3
  formula = G4_CELLULOSE_CELLOPHANE
  name = G4_CELLULOSE_CELLOPHANE
  specific = 4
FEATURE [App::DocumentObjectGroupPython] H_element022  label="H_element : 0.067"  # scripted group (container) (typed FeaturePython)
  n = 0.067125
FEATURE [App::DocumentObjectGroupPython] C_element026  label="C_element : 0.545"  # scripted group (container) (typed FeaturePython)
  n = 0.545403
FEATURE [App::DocumentObjectGroupPython] O_element027  label="O_element : 0.387"  # scripted group (container) (typed FeaturePython)
  n = 0.387472
FEATURE [App::DocumentObjectGroupPython] G4_CELLULOSE_BUTYRATE  # scripted group (container) (typed FeaturePython)
  Dunit = g/cm3
  Dvalue = 1.2
  Group = -> [H_element022,C_element026,O_element027]
  conduct = 2
  density = 1
  expand = 3
  formula = G4_CELLULOSE_BUTYRATE
  name = G4_CELLULOSE_BUTYRATE
  specific = 4
FEATURE [App::DocumentObjectGroupPython] H_element023  label="H_element : 0.029"  # scripted group (container) (typed FeaturePython)
  n = 0.029216
FEATURE [App::DocumentObjectGroupPython] C_element027  label="C_element : 0.271"  # scripted group (container) (typed FeaturePython)
  n = 0.271296
FEATURE [App::DocumentObjectGroupPython] N_element013  label="N_element : 0.121"  # scripted group (container) (typed FeaturePython)
  n = 0.121276
FEATURE [App::DocumentObjectGroupPython] O_element028  label="O_element : 0.578"  # scripted group (container) (typed FeaturePython)
  n = 0.578212
FEATURE [App::DocumentObjectGroupPython] G4_CELLULOSE_NITRATE  # scripted group (container) (typed FeaturePython)
  Dunit = g/cm3
  Dvalue = 1.49
  Group = -> [H_element023,C_element027,N_element013,O_element028]
  conduct = 2
  density = 1
  expand = 3
  formula = G4_CELLULOSE_NITRATE
  name = G4_CELLULOSE_NITRATE
  specific = 4
FEATURE [App::DocumentObjectGroupPython] H_element024  label="H_element : 0.108"  # scripted group (container) (typed FeaturePython)
  n = 0.107596
FEATURE [App::DocumentObjectGroupPython] N_element014  label="N_element : 0.001"  # scripted group (container) (typed FeaturePython)
  n = 0.0008
FEATURE [App::DocumentObjectGroupPython] O_element029  label="O_element : 0.875"  # scripted group (container) (typed FeaturePython)
  n = 0.874976
FEATURE [App::DocumentObjectGroupPython] S_element008  label="S_element : 0.015"  # scripted group (container) (typed FeaturePython)
  n = 0.014627
FEATURE [App::DocumentObjectGroupPython] Ce_element001  label="Ce_element : 0.002"  # scripted group (container) (typed FeaturePython)
  n = 0.002001
FEATURE [App::DocumentObjectGroupPython] G4_CERIC_SULFATE  # scripted group (container) (typed FeaturePython)
  Dunit = g/cm3
  Dvalue = 1.03
  Group = -> [H_element024,N_element014,O_element029,S_element008,Ce_element001]
  conduct = 2
  density = 1
  expand = 3
  formula = G4_CERIC_SULFATE
  name = G4_CERIC_SULFATE
  specific = 4
FEATURE [App::DocumentObjectGroupPython] Cs_element001  label="Cs_element : 1"  # scripted group (container) (typed FeaturePython)
  n = 1
  ref = Cs_element
FEATURE [App::DocumentObjectGroupPython] F_element006  label="F_element : 1"  # scripted group (container) (typed FeaturePython)
  n = 1
  ref = F_element
FEATURE [App::DocumentObjectGroupPython] G4_CESIUM_FLUORIDE  # scripted group (container) (typed FeaturePython)
  Dunit = g/cm3
  Dvalue = 4.115
  Group = -> [Cs_element001,F_element006]
  conduct = 2
  density = 1
  expand = 3
  formula = G4_CESIUM_FLUORIDE
  name = G4_CESIUM_FLUORIDE
  specific = 4
FEATURE [App::DocumentObjectGroupPython] Cs_element002  label="Cs_element : 002"  # scripted group (container) (typed FeaturePython)
  n = 1
  ref = Cs_element
FEATURE [App::DocumentObjectGroupPython] I_element001  label="I_element : 1"  # scripted group (container) (typed FeaturePython)
  n = 1
  ref = I_element
FEATURE [App::DocumentObjectGroupPython] G4_CESIUM_IODIDE  # scripted group (container) (typed FeaturePython)
  Dunit = g/cm3
  Dvalue = 4.51
  Group = -> [Cs_element002,I_element001]
  conduct = 2
  density = 1
  expand = 3
  formula = G4_CESIUM_IODIDE
  name = G4_CESIUM_IODIDE
  specific = 4
FEATURE [App::DocumentObjectGroupPython] C_element028  label="C_element : 013"  # scripted group (container) (typed FeaturePython)
  n = 6
  ref = C_element
FEATURE [App::DocumentObjectGroupPython] H_element025  label="H_element : 013"  # scripted group (container) (typed FeaturePython)
  n = 5
  ref = H_element
FEATURE [App::DocumentObjectGroupPython] Cl_element005  label="Cl_element : 1"  # scripted group (container) (typed FeaturePython)
  n = 1
  ref = Cl_element
FEATURE [App::DocumentObjectGroupPython] G4_CHLOROBENZENE  # scripted group (container) (typed FeaturePython)
  Dunit = g/cm3
  Dvalue = 1.1058
  Group = -> [C_element028,H_element025,Cl_element005]
  conduct = 2
  density = 1
  expand = 3
  formula = G4_CHLOROBENZENE
  name = G4_CHLOROBENZENE
  specific = 4
FEATURE [App::DocumentObjectGroupPython] C_element029  label="C_element : 014"  # scripted group (container) (typed FeaturePython)
  n = 1
  ref = C_element
FEATURE [App::DocumentObjectGroupPython] H_element026  label="H_element : 1"  # scripted group (container) (typed FeaturePython)
  n = 1
  ref = H_element
FEATURE [App::DocumentObjectGroupPython] Cl_element006  label="Cl_element : 3"  # scripted group (container) (typed FeaturePython)
  n = 3
  ref = Cl_element
FEATURE [App::DocumentObjectGroupPython] G4_CHLOROFORM  # scripted group (container) (typed FeaturePython)
  Dunit = g/cm3
  Dvalue = 1.4832
  Group = -> [C_element029,H_element026,Cl_element006]
  conduct = 2
  density = 1
  expand = 3
  formula = G4_CHLOROFORM
  name = G4_CHLOROFORM
  specific = 4
FEATURE [App::DocumentObjectGroupPython] H_element027  label="H_element : 0.010"  # scripted group (container) (typed FeaturePython)
  n = 0.01
FEATURE [App::DocumentObjectGroupPython] C_element030  label="C_element : 0.001"  # scripted group (container) (typed FeaturePython)
  n = 0.001
FEATURE [App::DocumentObjectGroupPython] O_element030  label="O_element : 0.529"  # scripted group (container) (typed FeaturePython)
  n = 0.529107
FEATURE [App::DocumentObjectGroupPython] Na_element005  label="Na_element : 0.016"  # scripted group (container) (typed FeaturePython)
  n = 0.016
FEATURE [App::DocumentObjectGroupPython] Mg_element003  label="Mg_element : 0.004"  # scripted group (container) (typed FeaturePython)
  n = 0.002
FEATURE [App::DocumentObjectGroupPython] Al_element002  label="Al_element : 0.034"  # scripted group (container) (typed FeaturePython)
  n = 0.033872
FEATURE [App::DocumentObjectGroupPython] Si_element002  label="Si_element : 0.337"  # scripted group (container) (typed FeaturePython)
  n = 0.337021
FEATURE [App::DocumentObjectGroupPython] K_element003  label="K_element : 0.013"  # scripted group (container) (typed FeaturePython)
  n = 0.013
FEATURE [App::DocumentObjectGroupPython] Ca_element010  label="Ca_element : 0.044"  # scripted group (container) (typed FeaturePython)
  n = 0.044
FEATURE [App::DocumentObjectGroupPython] Fe_element002  label="Fe_element : 0.014"  # scripted group (container) (typed FeaturePython)
  n = 0.014
FEATURE [App::DocumentObjectGroupPython] G4_CONCRETE  # scripted group (container) (typed FeaturePython)
  Dunit = g/cm3
  Dvalue = 2.3
  Group = -> [H_element027,C_element030,O_element030,Na_element005,Mg_element003,Al_element002,Si_element002,K_element003,Ca_element010,Fe_element002]
  conduct = 2
  density = 1
  expand = 3
  formula = G4_CONCRETE
  name = G4_CONCRETE
  specific = 4
FEATURE [App::DocumentObjectGroupPython] C_element031  label="C_element : 015"  # scripted group (container) (typed FeaturePython)
  n = 6
  ref = C_element
FEATURE [App::DocumentObjectGroupPython] H_element028  label="H_element : 12"  # scripted group (container) (typed FeaturePython)
  n = 12
  ref = H_element
FEATURE [App::DocumentObjectGroupPython] G4_CYCLOHEXANE  # scripted group (container) (typed FeaturePython)
  Dunit = g/cm3
  Dvalue = 0.779
  Group = -> [C_element031,H_element028]
  conduct = 2
  density = 1
  expand = 3
  formula = G4_CYCLOHEXANE
  name = G4_CYCLOHEXANE
  specific = 4
FEATURE [App::DocumentObjectGroupPython] C_element032  label="C_element : 016"  # scripted group (container) (typed FeaturePython)
  n = 6
  ref = C_element
FEATURE [App::DocumentObjectGroupPython] H_element029  label="H_element : 4"  # scripted group (container) (typed FeaturePython)
  n = 4
  ref = H_element
FEATURE [App::DocumentObjectGroupPython] Cl_element007  label="Cl_element : 2"  # scripted group (container) (typed FeaturePython)
  n = 2
  ref = Cl_element
FEATURE [App::DocumentObjectGroupPython] G4_1_2_DICHLOROBENZENE  label="G4_1.2-DICHLOROBENZENE"  # scripted group (container) (typed FeaturePython)
  Dunit = g/cm3
  Dvalue = 1.3048
  Group = -> [C_element032,H_element029,Cl_element007]
  conduct = 2
  density = 1
  expand = 3
  formula = G4_1.2-DICHLOROBENZENE
  name = G4_1.2-DICHLOROBENZENE
  specific = 4
FEATURE [App::DocumentObjectGroupPython] C_element033  label="C_element : 017"  # scripted group (container) (typed FeaturePython)
  n = 4
  ref = C_element
FEATURE [App::DocumentObjectGroupPython] H_element030  label="H_element : 8"  # scripted group (container) (typed FeaturePython)
  n = 8
  ref = H_element
FEATURE [App::DocumentObjectGroupPython] O_element031  label="O_element : 014"  # scripted group (container) (typed FeaturePython)
  n = 1
  ref = O_element
FEATURE [App::DocumentObjectGroupPython] Cl_element008  label="Cl_element : 005"  # scripted group (container) (typed FeaturePython)
  n = 2
  ref = Cl_element
FEATURE [App::DocumentObjectGroupPython] G4_DICHLORODIETHYL_ETHER  # scripted group (container) (typed FeaturePython)
  Dunit = g/cm3
  Dvalue = 1.2199
  Group = -> [C_element033,H_element030,O_element031,Cl_element008]
  conduct = 2
  density = 1
  expand = 3
  formula = G4_DICHLORODIETHYL_ETHER
  name = G4_DICHLORODIETHYL_ETHER
  specific = 4
FEATURE [App::DocumentObjectGroupPython] C_element034  label="C_element : 018"  # scripted group (container) (typed FeaturePython)
  n = 2
  ref = C_element
FEATURE [App::DocumentObjectGroupPython] H_element031  label="H_element : 014"  # scripted group (container) (typed FeaturePython)
  n = 4
  ref = H_element
FEATURE [App::DocumentObjectGroupPython] Cl_element009  label="Cl_element : 006"  # scripted group (container) (typed FeaturePython)
  n = 2
  ref = Cl_element
FEATURE [App::DocumentObjectGroupPython] G4_1_2_DICHLOROETHANE  label="G4_1.2-DICHLOROETHANE"  # scripted group (container) (typed FeaturePython)
  Dunit = g/cm3
  Dvalue = 1.2351
  Group = -> [C_element034,H_element031,Cl_element009]
  conduct = 2
  density = 1
  expand = 3
  formula = G4_1.2-DICHLOROETHANE
  name = G4_1.2-DICHLOROETHANE
  specific = 4
FEATURE [App::DocumentObjectGroupPython] C_element035  label="C_element : 019"  # scripted group (container) (typed FeaturePython)
  n = 4
  ref = C_element
FEATURE [App::DocumentObjectGroupPython] H_element032  label="H_element : 015"  # scripted group (container) (typed FeaturePython)
  n = 10
  ref = H_element
FEATURE [App::DocumentObjectGroupPython] O_element032  label="O_element : 015"  # scripted group (container) (typed FeaturePython)
  n = 1
  ref = O_element
FEATURE [App::DocumentObjectGroupPython] G4_DIETHYL_ETHER  # scripted group (container) (typed FeaturePython)
  Dunit = g/cm3
  Dvalue = 0.71378
  Group = -> [C_element035,H_element032,O_element032]
  conduct = 2
  density = 1
  expand = 3
  formula = G4_DIETHYL_ETHER
  name = G4_DIETHYL_ETHER
  specific = 4
FEATURE [App::DocumentObjectGroupPython] C_element036  label="C_element : 020"  # scripted group (container) (typed FeaturePython)
  n = 3
  ref = C_element
FEATURE [App::DocumentObjectGroupPython] H_element033  label="H_element : 016"  # scripted group (container) (typed FeaturePython)
  n = 7
  ref = H_element
FEATURE [App::DocumentObjectGroupPython] N_element015  label="N_element : 008"  # scripted group (container) (typed FeaturePython)
  n = 1
  ref = N_element
FEATURE [App::DocumentObjectGroupPython] O_element033  label="O_element : 016"  # scripted group (container) (typed FeaturePython)
  n = 1
  ref = O_element
FEATURE [App::DocumentObjectGroupPython] G4_N_N_DIMETHYL_FORMAMIDE  label="G4_N.N-DIMETHYL_FORMAMIDE"  # scripted group (container) (typed FeaturePython)
  Dunit = g/cm3
  Dvalue = 0.9487
  Group = -> [C_element036,H_element033,N_element015,O_element033]
  conduct = 2
  density = 1
  expand = 3
  formula = G4_N.N-DIMETHYL_FORMAMIDE
  name = G4_N.N-DIMETHYL_FORMAMIDE
  specific = 4
FEATURE [App::DocumentObjectGroupPython] C_element037  label="C_element : 021"  # scripted group (container) (typed FeaturePython)
  n = 2
  ref = C_element
FEATURE [App::DocumentObjectGroupPython] H_element034  label="H_element : 017"  # scripted group (container) (typed FeaturePython)
  n = 6
  ref = H_element
FEATURE [App::DocumentObjectGroupPython] O_element034  label="O_element : 017"  # scripted group (container) (typed FeaturePython)
  n = 1
  ref = O_element
FEATURE [App::DocumentObjectGroupPython] S_element009  label="S_element : 003"  # scripted group (container) (typed FeaturePython)
  n = 1
  ref = S_element
FEATURE [App::DocumentObjectGroupPython] G4_DIMETHYL_SULFOXIDE  # scripted group (container) (typed FeaturePython)
  Dunit = g/cm3
  Dvalue = 1.1014
  Group = -> [C_element037,H_element034,O_element034,S_element009]
  conduct = 2
  density = 1
  expand = 3
  formula = G4_DIMETHYL_SULFOXIDE
  name = G4_DIMETHYL_SULFOXIDE
  specific = 4
FEATURE [App::DocumentObjectGroupPython] C_element038  label="C_element : 022"  # scripted group (container) (typed FeaturePython)
  n = 2
  ref = C_element
FEATURE [App::DocumentObjectGroupPython] H_element035  label="H_element : 018"  # scripted group (container) (typed FeaturePython)
  n = 6
  ref = H_element
FEATURE [App::DocumentObjectGroupPython] G4_ETHANE  # scripted group (container) (typed FeaturePython)
  Dunit = g/cm3
  Dvalue = 0.00125324
  Group = -> [C_element038,H_element035]
  conduct = 2
  density = 1
  expand = 3
  formula = G4_ETHANE
  name = G4_ETHANE
  specific = 4
FEATURE [App::DocumentObjectGroupPython] C_element039  label="C_element : 023"  # scripted group (container) (typed FeaturePython)
  n = 2
  ref = C_element
FEATURE [App::DocumentObjectGroupPython] H_element036  label="H_element : 019"  # scripted group (container) (typed FeaturePython)
  n = 6
  ref = H_element
FEATURE [App::DocumentObjectGroupPython] O_element035  label="O_element : 018"  # scripted group (container) (typed FeaturePython)
  n = 1
  ref = O_element
FEATURE [App::DocumentObjectGroupPython] G4_ETHYL_ALCOHOL  # scripted group (container) (typed FeaturePython)
  Dunit = g/cm3
  Dvalue = 0.7893
  Group = -> [C_element039,H_element036,O_element035]
  conduct = 2
  density = 1
  expand = 3
  formula = G4_ETHYL_ALCOHOL
  name = G4_ETHYL_ALCOHOL
  specific = 4
FEATURE [App::DocumentObjectGroupPython] H_element037  label="H_element : 0.090"  # scripted group (container) (typed FeaturePython)
  n = 0.090027
FEATURE [App::DocumentObjectGroupPython] C_element040  label="C_element : 0.585"  # scripted group (container) (typed FeaturePython)
  n = 0.585182
FEATURE [App::DocumentObjectGroupPython] O_element036  label="O_element : 0.325"  # scripted group (container) (typed FeaturePython)
  n = 0.324791
FEATURE [App::DocumentObjectGroupPython] G4_ETHYL_CELLULOSE  # scripted group (container) (typed FeaturePython)
  Dunit = g/cm3
  Dvalue = 1.13
  Group = -> [H_element037,C_element040,O_element036]
  conduct = 2
  density = 1
  expand = 3
  formula = G4_ETHYL_CELLULOSE
  name = G4_ETHYL_CELLULOSE
  specific = 4
FEATURE [App::DocumentObjectGroupPython] C_element041  label="C_element : 024"  # scripted group (container) (typed FeaturePython)
  n = 2
  ref = C_element
FEATURE [App::DocumentObjectGroupPython] H_element038  label="H_element : 020"  # scripted group (container) (typed FeaturePython)
  n = 4
  ref = H_element
FEATURE [App::DocumentObjectGroupPython] G4_ETHYLENE  # scripted group (container) (typed FeaturePython)
  Dunit = g/cm3
  Dvalue = 0.00117497
  Group = -> [C_element041,H_element038]
  conduct = 2
  density = 1
  expand = 3
  formula = G4_ETHYLENE
  name = G4_ETHYLENE
  specific = 4
FEATURE [App::DocumentObjectGroupPython] H_element039  label="H_element : 0.096"  # scripted group (container) (typed FeaturePython)
  n = 0.096
FEATURE [App::DocumentObjectGroupPython] C_element042  label="C_element : 0.195"  # scripted group (container) (typed FeaturePython)
  n = 0.195
FEATURE [App::DocumentObjectGroupPython] N_element016  label="N_element : 0.057"  # scripted group (container) (typed FeaturePython)
  n = 0.057
FEATURE [App::DocumentObjectGroupPython] O_element037  label="O_element : 0.646"  # scripted group (container) (typed FeaturePython)
  n = 0.646
FEATURE [App::DocumentObjectGroupPython] Na_element006  label="Na_element : 0.017"  # scripted group (container) (typed FeaturePython)
  n = 0.001
FEATURE [App::DocumentObjectGroupPython] P_element005  label="P_element : 0.104"  # scripted group (container) (typed FeaturePython)
  n = 0.001
FEATURE [App::DocumentObjectGroupPython] S_element010  label="S_element : 0.016"  # scripted group (container) (typed FeaturePython)
  n = 0.003
FEATURE [App::DocumentObjectGroupPython] Cl_element010  label="Cl_element : 0.005"  # scripted group (container) (typed FeaturePython)
  n = 0.001
FEATURE [App::DocumentObjectGroupPython] G4_EYE_LENS_ICRP  # scripted group (container) (typed FeaturePython)
  Dunit = g/cm3
  Dvalue = 1.07
  Group = -> [H_element039,C_element042,N_element016,O_element037,Na_element006,P_element005,S_element010,Cl_element010]
  conduct = 2
  density = 1
  expand = 3
  formula = G4_EYE_LENS_ICRP
  name = G4_EYE_LENS_ICRP
  specific = 4
FEATURE [App::DocumentObjectGroupPython] Fe_element003  label="Fe_element : 2"  # scripted group (container) (typed FeaturePython)
  n = 2
  ref = Fe_element
FEATURE [App::DocumentObjectGroupPython] O_element038  label="O_element : 019"  # scripted group (container) (typed FeaturePython)
  n = 3
  ref = O_element
FEATURE [App::DocumentObjectGroupPython] G4_FERRIC_OXIDE  # scripted group (container) (typed FeaturePython)
  Dunit = g/cm3
  Dvalue = 5.2
  Group = -> [Fe_element003,O_element038]
  conduct = 2
  density = 1
  expand = 3
  formula = G4_FERRIC_OXIDE
  name = G4_FERRIC_OXIDE
  specific = 4
FEATURE [App::DocumentObjectGroupPython] Fe_element004  label="Fe_element : 1"  # scripted group (container) (typed FeaturePython)
  n = 1
  ref = Fe_element
FEATURE [App::DocumentObjectGroupPython] B_element003  label="B_element : 1"  # scripted group (container) (typed FeaturePython)
  n = 1
  ref = B_element
FEATURE [App::DocumentObjectGroupPython] G4_FERROBORIDE  # scripted group (container) (typed FeaturePython)
  Dunit = g/cm3
  Dvalue = 7.15
  Group = -> [Fe_element004,B_element003]
  conduct = 2
  density = 1
  expand = 3
  formula = G4_FERROBORIDE
  name = G4_FERROBORIDE
  specific = 4
FEATURE [App::DocumentObjectGroupPython] Fe_element005  label="Fe_element : 003"  # scripted group (container) (typed FeaturePython)
  n = 1
  ref = Fe_element
FEATURE [App::DocumentObjectGroupPython] O_element039  label="O_element : 020"  # scripted group (container) (typed FeaturePython)
  n = 1
  ref = O_element
FEATURE [App::DocumentObjectGroupPython] G4_FERROUS_OXIDE  # scripted group (container) (typed FeaturePython)
  Dunit = g/cm3
  Dvalue = 5.7
  Group = -> [Fe_element005,O_element039]
  conduct = 2
  density = 1
  expand = 3
  formula = G4_FERROUS_OXIDE
  name = G4_FERROUS_OXIDE
  specific = 4
FEATURE [App::DocumentObjectGroupPython] H_element040  label="H_element : 0.115"  # scripted group (container) (typed FeaturePython)
  n = 0.108259
FEATURE [App::DocumentObjectGroupPython] N_element017  label="N_element : 0.000"  # scripted group (container) (typed FeaturePython)
  n = 2.7e-05
FEATURE [App::DocumentObjectGroupPython] O_element040  label="O_element : 0.879"  # scripted group (container) (typed FeaturePython)
  n = 0.878636
FEATURE [App::DocumentObjectGroupPython] Na_element007  label="Na_element : 0.000"  # scripted group (container) (typed FeaturePython)
  n = 2.2e-05
FEATURE [App::DocumentObjectGroupPython] S_element011  label="S_element : 0.013"  # scripted group (container) (typed FeaturePython)
  n = 0.012968
FEATURE [App::DocumentObjectGroupPython] Cl_element011  label="Cl_element : 0.000"  # scripted group (container) (typed FeaturePython)
  n = 3.4e-05
FEATURE [App::DocumentObjectGroupPython] Fe_element006  label="Fe_element : 0.000"  # scripted group (container) (typed FeaturePython)
  n = 5.4e-05
FEATURE [App::DocumentObjectGroupPython] G4_FERROUS_SULFATE  # scripted group (container) (typed FeaturePython)
  Dunit = g/cm3
  Dvalue = 1.024
  Group = -> [H_element040,N_element017,O_element040,Na_element007,S_element011,Cl_element011,Fe_element006]
  conduct = 2
  density = 1
  expand = 3
  formula = G4_FERROUS_SULFATE
  name = G4_FERROUS_SULFATE
  specific = 4
FEATURE [App::DocumentObjectGroupPython] C_element043  label="C_element : 0.099"  # scripted group (container) (typed FeaturePython)
  n = 0.099335
FEATURE [App::DocumentObjectGroupPython] F_element007  label="F_element : 0.314"  # scripted group (container) (typed FeaturePython)
  n = 0.314247
FEATURE [App::DocumentObjectGroupPython] Cl_element012  label="Cl_element : 0.586"  # scripted group (container) (typed FeaturePython)
  n = 0.586418
FEATURE [App::DocumentObjectGroupPython] G4_FREON_12  label="G4_FREON-12"  # scripted group (container) (typed FeaturePython)
  Dunit = g/cm3
  Dvalue = 1.12
  Group = -> [C_element043,F_element007,Cl_element012]
  conduct = 2
  density = 1
  expand = 3
  formula = G4_FREON-12
  name = G4_FREON-12
  specific = 4
FEATURE [App::DocumentObjectGroupPython] C_element044  label="C_element : 0.057"  # scripted group (container) (typed FeaturePython)
  n = 0.057245
FEATURE [App::DocumentObjectGroupPython] F_element008  label="F_element : 0.181"  # scripted group (container) (typed FeaturePython)
  n = 0.181096
FEATURE [App::DocumentObjectGroupPython] Br_element001  label="Br_element : 0.762"  # scripted group (container) (typed FeaturePython)
  n = 0.761659
FEATURE [App::DocumentObjectGroupPython] G4_FREON_12B2  label="G4_FREON-12B2"  # scripted group (container) (typed FeaturePython)
  Dunit = g/cm3
  Dvalue = 1.8
  Group = -> [C_element044,F_element008,Br_element001]
  conduct = 2
  density = 1
  expand = 3
  formula = G4_FREON-12B2
  name = G4_FREON-12B2
  specific = 4
FEATURE [App::DocumentObjectGroupPython] C_element045  label="C_element : 0.115"  # scripted group (container) (typed FeaturePython)
  n = 0.114983
FEATURE [App::DocumentObjectGroupPython] F_element009  label="F_element : 0.546"  # scripted group (container) (typed FeaturePython)
  n = 0.545621
FEATURE [App::DocumentObjectGroupPython] Cl_element013  label="Cl_element : 0.339"  # scripted group (container) (typed FeaturePython)
  n = 0.339396
FEATURE [App::DocumentObjectGroupPython] G4_FREON_13  label="G4_FREON-13"  # scripted group (container) (typed FeaturePython)
  Dunit = g/cm3
  Dvalue = 0.95
  Group = -> [C_element045,F_element009,Cl_element013]
  conduct = 2
  density = 1
  expand = 3
  formula = G4_FREON-13
  name = G4_FREON-13
  specific = 4
FEATURE [App::DocumentObjectGroupPython] C_element046  label="C_element : 025"  # scripted group (container) (typed FeaturePython)
  n = 1
  ref = C_element
FEATURE [App::DocumentObjectGroupPython] F_element010  label="F_element : 3"  # scripted group (container) (typed FeaturePython)
  n = 3
  ref = F_element
FEATURE [App::DocumentObjectGroupPython] Br_element002  label="Br_element : 1"  # scripted group (container) (typed FeaturePython)
  n = 1
  ref = Br_element
FEATURE [App::DocumentObjectGroupPython] G4_FREON_13B1  label="G4_FREON-13B1"  # scripted group (container) (typed FeaturePython)
  Dunit = g/cm3
  Dvalue = 1.5
  Group = -> [C_element046,F_element010,Br_element002]
  conduct = 2
  density = 1
  expand = 3
  formula = G4_FREON-13B1
  name = G4_FREON-13B1
  specific = 4
FEATURE [App::DocumentObjectGroupPython] C_element047  label="C_element : 0.061"  # scripted group (container) (typed FeaturePython)
  n = 0.061309
FEATURE [App::DocumentObjectGroupPython] F_element011  label="F_element : 0.291"  # scripted group (container) (typed FeaturePython)
  n = 0.290924
FEATURE [App::DocumentObjectGroupPython] I_element002  label="I_element : 0.648"  # scripted group (container) (typed FeaturePython)
  n = 0.647767
FEATURE [App::DocumentObjectGroupPython] G4_FREON_13I1  label="G4_FREON-13I1"  # scripted group (container) (typed FeaturePython)
  Dunit = g/cm3
  Dvalue = 1.8
  Group = -> [C_element047,F_element011,I_element002]
  conduct = 2
  density = 1
  expand = 3
  formula = G4_FREON-13I1
  name = G4_FREON-13I1
  specific = 4
FEATURE [App::DocumentObjectGroupPython] Gd_element001  label="Gd_element : 2"  # scripted group (container) (typed FeaturePython)
  n = 2
  ref = Gd_element
FEATURE [App::DocumentObjectGroupPython] O_element041  label="O_element : 021"  # scripted group (container) (typed FeaturePython)
  n = 2
  ref = O_element
FEATURE [App::DocumentObjectGroupPython] S_element012  label="S_element : 004"  # scripted group (container) (typed FeaturePython)
  n = 1
  ref = S_element
FEATURE [App::DocumentObjectGroupPython] G4_GADOLINIUM_OXYSULFIDE  # scripted group (container) (typed FeaturePython)
  Dunit = g/cm3
  Dvalue = 7.44
  Group = -> [Gd_element001,O_element041,S_element012]
  conduct = 2
  density = 1
  expand = 3
  formula = G4_GADOLINIUM_OXYSULFIDE
  name = G4_GADOLINIUM_OXYSULFIDE
  specific = 4
FEATURE [App::DocumentObjectGroupPython] Ga_element001  label="Ga_element : 1"  # scripted group (container) (typed FeaturePython)
  n = 1
  ref = Ga_element
FEATURE [App::DocumentObjectGroupPython] As_element001  label="As_element : 1"  # scripted group (container) (typed FeaturePython)
  n = 1
  ref = As_element
FEATURE [App::DocumentObjectGroupPython] G4_GALLIUM_ARSENIDE  # scripted group (container) (typed FeaturePython)
  Dunit = g/cm3
  Dvalue = 5.31
  Group = -> [Ga_element001,As_element001]
  conduct = 2
  density = 1
  expand = 3
  formula = G4_GALLIUM_ARSENIDE
  name = G4_GALLIUM_ARSENIDE
  specific = 4
FEATURE [App::DocumentObjectGroupPython] H_element041  label="H_element : 0.081"  # scripted group (container) (typed FeaturePython)
  n = 0.08118
FEATURE [App::DocumentObjectGroupPython] C_element048  label="C_element : 0.416"  # scripted group (container) (typed FeaturePython)
  n = 0.41606
FEATURE [App::DocumentObjectGroupPython] N_element018  label="N_element : 0.111"  # scripted group (container) (typed FeaturePython)
  n = 0.11124
FEATURE [App::DocumentObjectGroupPython] O_element042  label="O_element : 0.381"  # scripted group (container) (typed FeaturePython)
  n = 0.38064
FEATURE [App::DocumentObjectGroupPython] S_element013  label="S_element : 0.011"  # scripted group (container) (typed FeaturePython)
  n = 0.01088
FEATURE [App::DocumentObjectGroupPython] G4_GEL_PHOTO_EMULSION  # scripted group (container) (typed FeaturePython)
  Dunit = g/cm3
  Dvalue = 1.2914
  Group = -> [H_element041,C_element048,N_element018,O_element042,S_element013]
  conduct = 2
  density = 1
  expand = 3
  formula = G4_GEL_PHOTO_EMULSION
  name = G4_GEL_PHOTO_EMULSION
  specific = 4
FEATURE [App::DocumentObjectGroupPython] B_element004  label="B_element : 0.040"  # scripted group (container) (typed FeaturePython)
  n = 0.0400639
FEATURE [App::DocumentObjectGroupPython] O_element043  label="O_element : 0.540"  # scripted group (container) (typed FeaturePython)
  n = 0.539561
FEATURE [App::DocumentObjectGroupPython] Na_element008  label="Na_element : 0.028"  # scripted group (container) (typed FeaturePython)
  n = 0.0281909
FEATURE [App::DocumentObjectGroupPython] Al_element003  label="Al_element : 0.012"  # scripted group (container) (typed FeaturePython)
  n = 0.011644
FEATURE [App::DocumentObjectGroupPython] Si_element003  label="Si_element : 0.377"  # scripted group (container) (typed FeaturePython)
  n = 0.377219
FEATURE [App::DocumentObjectGroupPython] K_element004  label="K_element : 0.014"  # scripted group (container) (typed FeaturePython)
  n = 0.00332099
FEATURE [App::DocumentObjectGroupPython] G4_Pyrex_Glass  # scripted group (container) (typed FeaturePython)
  Dunit = g/cm3
  Dvalue = 2.23
  Group = -> [B_element004,O_element043,Na_element008,Al_element003,Si_element003,K_element004]
  conduct = 2
  density = 1
  expand = 3
  formula = G4_Pyrex_Glass
  name = G4_Pyrex_Glass
  specific = 4
FEATURE [App::DocumentObjectGroupPython] O_element044  label="O_element : 0.156"  # scripted group (container) (typed FeaturePython)
  n = 0.156453
FEATURE [App::DocumentObjectGroupPython] Si_element004  label="Si_element : 0.081"  # scripted group (container) (typed FeaturePython)
  n = 0.080866
FEATURE [App::DocumentObjectGroupPython] Ti_element001  label="Ti_element : 0.008"  # scripted group (container) (typed FeaturePython)
  n = 0.008092
FEATURE [App::DocumentObjectGroupPython] As_element002  label="As_element : 0.003"  # scripted group (container) (typed FeaturePython)
  n = 0.002651
FEATURE [App::DocumentObjectGroupPython] Pb_element001  label="Pb_element : 0.752"  # scripted group (container) (typed FeaturePython)
  n = 0.751938
FEATURE [App::DocumentObjectGroupPython] G4_GLASS_LEAD  # scripted group (container) (typed FeaturePython)
  Dunit = g/cm3
  Dvalue = 6.22
  Group = -> [O_element044,Si_element004,Ti_element001,As_element002,Pb_element001]
  conduct = 2
  density = 1
  expand = 3
  formula = G4_GLASS_LEAD
  name = G4_GLASS_LEAD
  specific = 4
FEATURE [App::DocumentObjectGroupPython] O_element045  label="O_element : 0.460"  # scripted group (container) (typed FeaturePython)
  n = 0.4598
FEATURE [App::DocumentObjectGroupPython] Na_element009  label="Na_element : 0.096"  # scripted group (container) (typed FeaturePython)
  n = 0.0964411
FEATURE [App::DocumentObjectGroupPython] Si_element005  label="Si_element : 0.378"  # scripted group (container) (typed FeaturePython)
  n = 0.336553
FEATURE [App::DocumentObjectGroupPython] Ca_element011  label="Ca_element : 0.107"  # scripted group (container) (typed FeaturePython)
  n = 0.107205
FEATURE [App::DocumentObjectGroupPython] G4_GLASS_PLATE  # scripted group (container) (typed FeaturePython)
  Dunit = g/cm3
  Dvalue = 2.4
  Group = -> [O_element045,Na_element009,Si_element005,Ca_element011]
  conduct = 2
  density = 1
  expand = 3
  formula = G4_GLASS_PLATE
  name = G4_GLASS_PLATE
  specific = 4
FEATURE [App::DocumentObjectGroupPython] C_element049  label="C_element : 026"  # scripted group (container) (typed FeaturePython)
  n = 5
  ref = C_element
FEATURE [App::DocumentObjectGroupPython] H_element042  label="H_element : 021"  # scripted group (container) (typed FeaturePython)
  n = 10
  ref = H_element
FEATURE [App::DocumentObjectGroupPython] N_element019  label="N_element : 2"  # scripted group (container) (typed FeaturePython)
  n = 2
  ref = N_element
FEATURE [App::DocumentObjectGroupPython] O_element046  label="O_element : 022"  # scripted group (container) (typed FeaturePython)
  n = 3
  ref = O_element
FEATURE [App::DocumentObjectGroupPython] G4_GLUTAMINE  # scripted group (container) (typed FeaturePython)
  Dunit = g/cm3
  Dvalue = 1.46
  Group = -> [C_element049,H_element042,N_element019,O_element046]
  conduct = 2
  density = 1
  expand = 3
  formula = G4_GLUTAMINE
  name = G4_GLUTAMINE
  specific = 4
FEATURE [App::DocumentObjectGroupPython] C_element050  label="C_element : 027"  # scripted group (container) (typed FeaturePython)
  n = 3
  ref = C_element
FEATURE [App::DocumentObjectGroupPython] H_element043  label="H_element : 022"  # scripted group (container) (typed FeaturePython)
  n = 8
  ref = H_element
FEATURE [App::DocumentObjectGroupPython] O_element047  label="O_element : 023"  # scripted group (container) (typed FeaturePython)
  n = 3
  ref = O_element
FEATURE [App::DocumentObjectGroupPython] G4_GLYCEROL  # scripted group (container) (typed FeaturePython)
  Dunit = g/cm3
  Dvalue = 1.2613
  Group = -> [C_element050,H_element043,O_element047]
  conduct = 2
  density = 1
  expand = 3
  formula = G4_GLYCEROL
  name = G4_GLYCEROL
  specific = 4
FEATURE [App::DocumentObjectGroupPython] C_element051  label="C_element : 028"  # scripted group (container) (typed FeaturePython)
  n = 5
  ref = C_element
FEATURE [App::DocumentObjectGroupPython] H_element044  label="H_element : 023"  # scripted group (container) (typed FeaturePython)
  n = 5
  ref = H_element
FEATURE [App::DocumentObjectGroupPython] N_element020  label="N_element : 009"  # scripted group (container) (typed FeaturePython)
  n = 5
  ref = N_element
FEATURE [App::DocumentObjectGroupPython] O_element048  label="O_element : 024"  # scripted group (container) (typed FeaturePython)
  n = 1
  ref = O_element
FEATURE [App::DocumentObjectGroupPython] G4_GUANINE  # scripted group (container) (typed FeaturePython)
  Dunit = g/cm3
  Dvalue = 2.2
  Group = -> [C_element051,H_element044,N_element020,O_element048]
  conduct = 2
  density = 1
  expand = 3
  formula = G4_GUANINE
  name = G4_GUANINE
  specific = 4
FEATURE [App::DocumentObjectGroupPython] Ca_element012  label="Ca_element : 006"  # scripted group (container) (typed FeaturePython)
  n = 1
  ref = Ca_element
FEATURE [App::DocumentObjectGroupPython] S_element014  label="S_element : 005"  # scripted group (container) (typed FeaturePython)
  n = 1
  ref = S_element
FEATURE [App::DocumentObjectGroupPython] O_element049  label="O_element : 6"  # scripted group (container) (typed FeaturePython)
  n = 6
  ref = O_element
FEATURE [App::DocumentObjectGroupPython] H_element045  label="H_element : 024"  # scripted group (container) (typed FeaturePython)
  n = 4
  ref = H_element
FEATURE [App::DocumentObjectGroupPython] G4_GYPSUM  # scripted group (container) (typed FeaturePython)
  Dunit = g/cm3
  Dvalue = 2.32
  Group = -> [Ca_element012,S_element014,O_element049,H_element045]
  conduct = 2
  density = 1
  expand = 3
  formula = G4_GYPSUM
  name = G4_GYPSUM
  specific = 4
FEATURE [App::DocumentObjectGroupPython] C_element052  label="C_element : 7"  # scripted group (container) (typed FeaturePython)
  n = 7
  ref = C_element
FEATURE [App::DocumentObjectGroupPython] H_element046  label="H_element : 16"  # scripted group (container) (typed FeaturePython)
  n = 16
  ref = H_element
FEATURE [App::DocumentObjectGroupPython] G4_N_HEPTANE  label="G4_N-HEPTANE"  # scripted group (container) (typed FeaturePython)
  Dunit = g/cm3
  Dvalue = 0.68376
  Group = -> [C_element052,H_element046]
  conduct = 2
  density = 1
  expand = 3
  formula = G4_N-HEPTANE
  name = G4_N-HEPTANE
  specific = 4
FEATURE [App::DocumentObjectGroupPython] C_element053  label="C_element : 029"  # scripted group (container) (typed FeaturePython)
  n = 6
  ref = C_element
FEATURE [App::DocumentObjectGroupPython] H_element047  label="H_element : 14"  # scripted group (container) (typed FeaturePython)
  n = 14
  ref = H_element
FEATURE [App::DocumentObjectGroupPython] G4_N_HEXANE  label="G4_N-HEXANE"  # scripted group (container) (typed FeaturePython)
  Dunit = g/cm3
  Dvalue = 0.6603
  Group = -> [C_element053,H_element047]
  conduct = 2
  density = 1
  expand = 3
  formula = G4_N-HEXANE
  name = G4_N-HEXANE
  specific = 4
FEATURE [App::DocumentObjectGroupPython] C_element054  label="C_element : 22"  # scripted group (container) (typed FeaturePython)
  n = 22
  ref = C_element
FEATURE [App::DocumentObjectGroupPython] H_element048  label="H_element : 025"  # scripted group (container) (typed FeaturePython)
  n = 10
  ref = H_element
FEATURE [App::DocumentObjectGroupPython] N_element021  label="N_element : 010"  # scripted group (container) (typed FeaturePython)
  n = 2
  ref = N_element
FEATURE [App::DocumentObjectGroupPython] O_element050  label="O_element : 025"  # scripted group (container) (typed FeaturePython)
  n = 5
  ref = O_element
FEATURE [App::DocumentObjectGroupPython] G4_KAPTON  # scripted group (container) (typed FeaturePython)
  Dunit = g/cm3
  Dvalue = 1.42
  Group = -> [C_element054,H_element048,N_element021,O_element050]
  conduct = 2
  density = 1
  expand = 3
  formula = G4_KAPTON
  name = G4_KAPTON
  specific = 4
FEATURE [App::DocumentObjectGroupPython] La_element001  label="La_element : 1"  # scripted group (container) (typed FeaturePython)
  n = 1
  ref = La_element
FEATURE [App::DocumentObjectGroupPython] Br_element003  label="Br_element : 002"  # scripted group (container) (typed FeaturePython)
  n = 1
  ref = Br_element
FEATURE [App::DocumentObjectGroupPython] O_element051  label="O_element : 026"  # scripted group (container) (typed FeaturePython)
  n = 1
  ref = O_element
FEATURE [App::DocumentObjectGroupPython] G4_LANTHANUM_OXYBROMIDE  # scripted group (container) (typed FeaturePython)
  Dunit = g/cm3
  Dvalue = 6.28
  Group = -> [La_element001,Br_element003,O_element051]
  conduct = 2
  density = 1
  expand = 3
  formula = G4_LANTHANUM_OXYBROMIDE
  name = G4_LANTHANUM_OXYBROMIDE
  specific = 4
FEATURE [App::DocumentObjectGroupPython] La_element002  label="La_element : 2"  # scripted group (container) (typed FeaturePython)
  n = 2
  ref = La_element
FEATURE [App::DocumentObjectGroupPython] O_element052  label="O_element : 027"  # scripted group (container) (typed FeaturePython)
  n = 2
  ref = O_element
FEATURE [App::DocumentObjectGroupPython] S_element015  label="S_element : 006"  # scripted group (container) (typed FeaturePython)
  n = 1
  ref = S_element
FEATURE [App::DocumentObjectGroupPython] G4_LANTHANUM_OXYSULFIDE  # scripted group (container) (typed FeaturePython)
  Dunit = g/cm3
  Dvalue = 5.86
  Group = -> [La_element002,O_element052,S_element015]
  conduct = 2
  density = 1
  expand = 3
  formula = G4_LANTHANUM_OXYSULFIDE
  name = G4_LANTHANUM_OXYSULFIDE
  specific = 4
FEATURE [App::DocumentObjectGroupPython] O_element053  label="O_element : 0.072"  # scripted group (container) (typed FeaturePython)
  n = 0.071682
FEATURE [App::DocumentObjectGroupPython] Pb_element002  label="Pb_element : 0.928"  # scripted group (container) (typed FeaturePython)
  n = 0.928318
FEATURE [App::DocumentObjectGroupPython] G4_LEAD_OXIDE  # scripted group (container) (typed FeaturePython)
  Dunit = g/cm3
  Dvalue = 9.53
  Group = -> [O_element053,Pb_element002]
  conduct = 2
  density = 1
  expand = 3
  formula = G4_LEAD_OXIDE
  name = G4_LEAD_OXIDE
  specific = 4
FEATURE [App::DocumentObjectGroupPython] Li_element001  label="Li_element : 1"  # scripted group (container) (typed FeaturePython)
  n = 1
  ref = Li_element
FEATURE [App::DocumentObjectGroupPython] N_element022  label="N_element : 011"  # scripted group (container) (typed FeaturePython)
  n = 1
  ref = N_element
FEATURE [App::DocumentObjectGroupPython] H_element049  label="H_element : 026"  # scripted group (container) (typed FeaturePython)
  n = 2
  ref = H_element
FEATURE [App::DocumentObjectGroupPython] G4_LITHIUM_AMIDE  # scripted group (container) (typed FeaturePython)
  Dunit = g/cm3
  Dvalue = 1.178
  Group = -> [Li_element001,N_element022,H_element049]
  conduct = 2
  density = 1
  expand = 3
  formula = G4_LITHIUM_AMIDE
  name = G4_LITHIUM_AMIDE
  specific = 4
FEATURE [App::DocumentObjectGroupPython] Li_element002  label="Li_element : 2"  # scripted group (container) (typed FeaturePython)
  n = 2
  ref = Li_element
FEATURE [App::DocumentObjectGroupPython] C_element055  label="C_element : 030"  # scripted group (container) (typed FeaturePython)
  n = 1
  ref = C_element
FEATURE [App::DocumentObjectGroupPython] O_element054  label="O_element : 028"  # scripted group (container) (typed FeaturePython)
  n = 3
  ref = O_element
FEATURE [App::DocumentObjectGroupPython] G4_LITHIUM_CARBONATE  # scripted group (container) (typed FeaturePython)
  Dunit = g/cm3
  Dvalue = 2.11
  Group = -> [Li_element002,C_element055,O_element054]
  conduct = 2
  density = 1
  expand = 3
  formula = G4_LITHIUM_CARBONATE
  name = G4_LITHIUM_CARBONATE
  specific = 4
FEATURE [App::DocumentObjectGroupPython] Li_element003  label="Li_element : 003"  # scripted group (container) (typed FeaturePython)
  n = 1
  ref = Li_element
FEATURE [App::DocumentObjectGroupPython] F_element012  label="F_element : 004"  # scripted group (container) (typed FeaturePython)
  n = 1
  ref = F_element
FEATURE [App::DocumentObjectGroupPython] G4_LITHIUM_FLUORIDE  # scripted group (container) (typed FeaturePython)
  Dunit = g/cm3
  Dvalue = 2.635
  Group = -> [Li_element003,F_element012]
  conduct = 2
  density = 1
  expand = 3
  formula = G4_LITHIUM_FLUORIDE
  name = G4_LITHIUM_FLUORIDE
  specific = 4
FEATURE [App::DocumentObjectGroupPython] Li_element004  label="Li_element : 004"  # scripted group (container) (typed FeaturePython)
  n = 1
  ref = Li_element
FEATURE [App::DocumentObjectGroupPython] H_element050  label="H_element : 027"  # scripted group (container) (typed FeaturePython)
  n = 1
  ref = H_element
FEATURE [App::DocumentObjectGroupPython] G4_LITHIUM_HYDRIDE  # scripted group (container) (typed FeaturePython)
  Dunit = g/cm3
  Dvalue = 0.82
  Group = -> [Li_element004,H_element050]
  conduct = 2
  density = 1
  expand = 3
  formula = G4_LITHIUM_HYDRIDE
  name = G4_LITHIUM_HYDRIDE
  specific = 4
FEATURE [App::DocumentObjectGroupPython] Li_element005  label="Li_element : 005"  # scripted group (container) (typed FeaturePython)
  n = 1
  ref = Li_element
FEATURE [App::DocumentObjectGroupPython] I_element003  label="I_element : 002"  # scripted group (container) (typed FeaturePython)
  n = 1
  ref = I_element
FEATURE [App::DocumentObjectGroupPython] G4_LITHIUM_IODIDE  # scripted group (container) (typed FeaturePython)
  Dunit = g/cm3
  Dvalue = 3.494
  Group = -> [Li_element005,I_element003]
  conduct = 2
  density = 1
  expand = 3
  formula = G4_LITHIUM_IODIDE
  name = G4_LITHIUM_IODIDE
  specific = 4
FEATURE [App::DocumentObjectGroupPython] Li_element006  label="Li_element : 006"  # scripted group (container) (typed FeaturePython)
  n = 2
  ref = Li_element
FEATURE [App::DocumentObjectGroupPython] O_element055  label="O_element : 029"  # scripted group (container) (typed FeaturePython)
  n = 1
  ref = O_element
FEATURE [App::DocumentObjectGroupPython] G4_LITHIUM_OXIDE  # scripted group (container) (typed FeaturePython)
  Dunit = g/cm3
  Dvalue = 2.013
  Group = -> [Li_element006,O_element055]
  conduct = 2
  density = 1
  expand = 3
  formula = G4_LITHIUM_OXIDE
  name = G4_LITHIUM_OXIDE
  specific = 4
FEATURE [App::DocumentObjectGroupPython] Li_element007  label="Li_element : 007"  # scripted group (container) (typed FeaturePython)
  n = 2
  ref = Li_element
FEATURE [App::DocumentObjectGroupPython] B_element005  label="B_element : 005"  # scripted group (container) (typed FeaturePython)
  n = 4
  ref = B_element
FEATURE [App::DocumentObjectGroupPython] O_element056  label="O_element : 7"  # scripted group (container) (typed FeaturePython)
  n = 7
  ref = O_element
FEATURE [App::DocumentObjectGroupPython] G4_LITHIUM_TETRABORATE  # scripted group (container) (typed FeaturePython)
  Dunit = g/cm3
  Dvalue = 2.44
  Group = -> [Li_element007,B_element005,O_element056]
  conduct = 2
  density = 1
  expand = 3
  formula = G4_LITHIUM_TETRABORATE
  name = G4_LITHIUM_TETRABORATE
  specific = 4
FEATURE [App::DocumentObjectGroupPython] H_element051  label="H_element : 0.105"  # scripted group (container) (typed FeaturePython)
  n = 0.105
FEATURE [App::DocumentObjectGroupPython] C_element056  label="C_element : 0.083"  # scripted group (container) (typed FeaturePython)
  n = 0.083
FEATURE [App::DocumentObjectGroupPython] N_element023  label="N_element : 0.023"  # scripted group (container) (typed FeaturePython)
  n = 0.023
FEATURE [App::DocumentObjectGroupPython] O_element057  label="O_element : 0.779"  # scripted group (container) (typed FeaturePython)
  n = 0.779
FEATURE [App::DocumentObjectGroupPython] Na_element010  label="Na_element : 0.097"  # scripted group (container) (typed FeaturePython)
  n = 0.002
FEATURE [App::DocumentObjectGroupPython] P_element006  label="P_element : 0.105"  # scripted group (container) (typed FeaturePython)
  n = 0.001
FEATURE [App::DocumentObjectGroupPython] S_element016  label="S_element : 0.017"  # scripted group (container) (typed FeaturePython)
  n = 0.002
FEATURE [App::DocumentObjectGroupPython] Cl_element014  label="Cl_element : 0.587"  # scripted group (container) (typed FeaturePython)
  n = 0.003
FEATURE [App::DocumentObjectGroupPython] K_element005  label="K_element : 0.015"  # scripted group (container) (typed FeaturePython)
  n = 0.002
FEATURE [App::DocumentObjectGroupPython] G4_LUNG_ICRP  # scripted group (container) (typed FeaturePython)
  Dunit = g/cm3
  Dvalue = 1.04
  Group = -> [H_element051,C_element056,N_element023,O_element057,Na_element010,P_element006,S_element016,Cl_element014,K_element005]
  conduct = 2
  density = 1
  expand = 3
  formula = G4_LUNG_ICRP
  name = G4_LUNG_ICRP
  specific = 4
FEATURE [App::DocumentObjectGroupPython] H_element052  label="H_element : 0.116"  # scripted group (container) (typed FeaturePython)
  n = 0.114318
FEATURE [App::DocumentObjectGroupPython] C_element057  label="C_element : 0.656"  # scripted group (container) (typed FeaturePython)
  n = 0.655824
FEATURE [App::DocumentObjectGroupPython] O_element058  label="O_element : 0.092"  # scripted group (container) (typed FeaturePython)
  n = 0.0921831
FEATURE [App::DocumentObjectGroupPython] Mg_element004  label="Mg_element : 0.135"  # scripted group (container) (typed FeaturePython)
  n = 0.134792
FEATURE [App::DocumentObjectGroupPython] Ca_element013  label="Ca_element : 0.003"  # scripted group (container) (typed FeaturePython)
  n = 0.002883
FEATURE [App::DocumentObjectGroupPython] G4_M3_WAX  # scripted group (container) (typed FeaturePython)
  Dunit = g/cm3
  Dvalue = 1.05
  Group = -> [H_element052,C_element057,O_element058,Mg_element004,Ca_element013]
  conduct = 2
  density = 1
  expand = 3
  formula = G4_M3_WAX
  name = G4_M3_WAX
  specific = 4
FEATURE [App::DocumentObjectGroupPython] Mg_element005  label="Mg_element : 1"  # scripted group (container) (typed FeaturePython)
  n = 1
  ref = Mg_element
FEATURE [App::DocumentObjectGroupPython] C_element058  label="C_element : 031"  # scripted group (container) (typed FeaturePython)
  n = 1
  ref = C_element
FEATURE [App::DocumentObjectGroupPython] O_element059  label="O_element : 030"  # scripted group (container) (typed FeaturePython)
  n = 3
  ref = O_element
FEATURE [App::DocumentObjectGroupPython] G4_MAGNESIUM_CARBONATE  # scripted group (container) (typed FeaturePython)
  Dunit = g/cm3
  Dvalue = 2.958
  Group = -> [Mg_element005,C_element058,O_element059]
  conduct = 2
  density = 1
  expand = 3
  formula = G4_MAGNESIUM_CARBONATE
  name = G4_MAGNESIUM_CARBONATE
  specific = 4
FEATURE [App::DocumentObjectGroupPython] Mg_element006  label="Mg_element : 002"  # scripted group (container) (typed FeaturePython)
  n = 1
  ref = Mg_element
FEATURE [App::DocumentObjectGroupPython] F_element013  label="F_element : 005"  # scripted group (container) (typed FeaturePython)
  n = 2
  ref = F_element
FEATURE [App::DocumentObjectGroupPython] G4_MAGNESIUM_FLUORIDE  # scripted group (container) (typed FeaturePython)
  Dunit = g/cm3
  Dvalue = 3
  Group = -> [Mg_element006,F_element013]
  conduct = 2
  density = 1
  expand = 3
  formula = G4_MAGNESIUM_FLUORIDE
  name = G4_MAGNESIUM_FLUORIDE
  specific = 4
FEATURE [App::DocumentObjectGroupPython] Mg_element007  label="Mg_element : 003"  # scripted group (container) (typed FeaturePython)
  n = 1
  ref = Mg_element
FEATURE [App::DocumentObjectGroupPython] O_element060  label="O_element : 031"  # scripted group (container) (typed FeaturePython)
  n = 1
  ref = O_element
FEATURE [App::DocumentObjectGroupPython] G4_MAGNESIUM_OXIDE  # scripted group (container) (typed FeaturePython)
  Dunit = g/cm3
  Dvalue = 3.58
  Group = -> [Mg_element007,O_element060]
  conduct = 2
  density = 1
  expand = 3
  formula = G4_MAGNESIUM_OXIDE
  name = G4_MAGNESIUM_OXIDE
  specific = 4
FEATURE [App::DocumentObjectGroupPython] Mg_element008  label="Mg_element : 004"  # scripted group (container) (typed FeaturePython)
  n = 1
  ref = Mg_element
FEATURE [App::DocumentObjectGroupPython] B_element006  label="B_element : 006"  # scripted group (container) (typed FeaturePython)
  n = 4
  ref = B_element
FEATURE [App::DocumentObjectGroupPython] O_element061  label="O_element : 032"  # scripted group (container) (typed FeaturePython)
  n = 7
  ref = O_element
FEATURE [App::DocumentObjectGroupPython] G4_MAGNESIUM_TETRABORATE  # scripted group (container) (typed FeaturePython)
  Dunit = g/cm3
  Dvalue = 2.53
  Group = -> [Mg_element008,B_element006,O_element061]
  conduct = 2
  density = 1
  expand = 3
  formula = G4_MAGNESIUM_TETRABORATE
  name = G4_MAGNESIUM_TETRABORATE
  specific = 4
FEATURE [App::DocumentObjectGroupPython] Hg_element001  label="Hg_element : 1"  # scripted group (container) (typed FeaturePython)
  n = 1
  ref = Hg_element
FEATURE [App::DocumentObjectGroupPython] I_element004  label="I_element : 2"  # scripted group (container) (typed FeaturePython)
  n = 2
  ref = I_element
FEATURE [App::DocumentObjectGroupPython] G4_MERCURIC_IODIDE  # scripted group (container) (typed FeaturePython)
  Dunit = g/cm3
  Dvalue = 6.36
  Group = -> [Hg_element001,I_element004]
  conduct = 2
  density = 1
  expand = 3
  formula = G4_MERCURIC_IODIDE
  name = G4_MERCURIC_IODIDE
  specific = 4
FEATURE [App::DocumentObjectGroupPython] C_element059  label="C_element : 032"  # scripted group (container) (typed FeaturePython)
  n = 1
  ref = C_element
FEATURE [App::DocumentObjectGroupPython] H_element053  label="H_element : 028"  # scripted group (container) (typed FeaturePython)
  n = 4
  ref = H_element
FEATURE [App::DocumentObjectGroupPython] G4_METHANE  # scripted group (container) (typed FeaturePython)
  Dunit = g/cm3
  Dvalue = 0.000667151
  Group = -> [C_element059,H_element053]
  conduct = 2
  density = 1
  expand = 3
  formula = G4_METHANE
  name = G4_METHANE
  specific = 4
FEATURE [App::DocumentObjectGroupPython] C_element060  label="C_element : 033"  # scripted group (container) (typed FeaturePython)
  n = 1
  ref = C_element
FEATURE [App::DocumentObjectGroupPython] H_element054  label="H_element : 029"  # scripted group (container) (typed FeaturePython)
  n = 4
  ref = H_element
FEATURE [App::DocumentObjectGroupPython] O_element062  label="O_element : 033"  # scripted group (container) (typed FeaturePython)
  n = 1
  ref = O_element
FEATURE [App::DocumentObjectGroupPython] G4_METHANOL  # scripted group (container) (typed FeaturePython)
  Dunit = g/cm3
  Dvalue = 0.7914
  Group = -> [C_element060,H_element054,O_element062]
  conduct = 2
  density = 1
  expand = 3
  formula = G4_METHANOL
  name = G4_METHANOL
  specific = 4
FEATURE [App::DocumentObjectGroupPython] H_element055  label="H_element : 0.134"  # scripted group (container) (typed FeaturePython)
  n = 0.13404
FEATURE [App::DocumentObjectGroupPython] C_element061  label="C_element : 0.778"  # scripted group (container) (typed FeaturePython)
  n = 0.77796
FEATURE [App::DocumentObjectGroupPython] O_element063  label="O_element : 0.035"  # scripted group (container) (typed FeaturePython)
  n = 0.03502
FEATURE [App::DocumentObjectGroupPython] Mg_element009  label="Mg_element : 0.039"  # scripted group (container) (typed FeaturePython)
  n = 0.038594
FEATURE [App::DocumentObjectGroupPython] Ti_element002  label="Ti_element : 0.014"  # scripted group (container) (typed FeaturePython)
  n = 0.014386
FEATURE [App::DocumentObjectGroupPython] G4_MIX_D_WAX  # scripted group (container) (typed FeaturePython)
  Dunit = g/cm3
  Dvalue = 0.99
  Group = -> [H_element055,C_element061,O_element063,Mg_element009,Ti_element002]
  conduct = 2
  density = 1
  expand = 3
  formula = G4_MIX_D_WAX
  name = G4_MIX_D_WAX
  specific = 4
FEATURE [App::DocumentObjectGroupPython] H_element056  label="H_element : 0.135"  # scripted group (container) (typed FeaturePython)
  n = 0.081192
FEATURE [App::DocumentObjectGroupPython] C_element062  label="C_element : 0.583"  # scripted group (container) (typed FeaturePython)
  n = 0.583442
FEATURE [App::DocumentObjectGroupPython] N_element024  label="N_element : 0.018"  # scripted group (container) (typed FeaturePython)
  n = 0.017798
FEATURE [App::DocumentObjectGroupPython] O_element064  label="O_element : 0.186"  # scripted group (container) (typed FeaturePython)
  n = 0.186381
FEATURE [App::DocumentObjectGroupPython] Mg_element010  label="Mg_element : 0.130"  # scripted group (container) (typed FeaturePython)
  n = 0.130287
FEATURE [App::DocumentObjectGroupPython] Cl_element015  label="Cl_element : 0.588"  # scripted group (container) (typed FeaturePython)
  n = 0.0009
FEATURE [App::DocumentObjectGroupPython] G4_MS20_TISSUE  # scripted group (container) (typed FeaturePython)
  Dunit = g/cm3
  Dvalue = 1
  Group = -> [H_element056,C_element062,N_element024,O_element064,Mg_element010,Cl_element015]
  conduct = 2
  density = 1
  expand = 3
  formula = G4_MS20_TISSUE
  name = G4_MS20_TISSUE
  specific = 4
FEATURE [App::DocumentObjectGroupPython] H_element057  label="H_element : 0.136"  # scripted group (container) (typed FeaturePython)
  n = 0.102
FEATURE [App::DocumentObjectGroupPython] C_element063  label="C_element : 0.143"  # scripted group (container) (typed FeaturePython)
  n = 0.143
FEATURE [App::DocumentObjectGroupPython] N_element025  label="N_element : 0.034"  # scripted group (container) (typed FeaturePython)
  n = 0.034
FEATURE [App::DocumentObjectGroupPython] O_element065  label="O_element : 0.710"  # scripted group (container) (typed FeaturePython)
  n = 0.71
FEATURE [App::DocumentObjectGroupPython] Na_element011  label="Na_element : 0.098"  # scripted group (container) (typed FeaturePython)
  n = 0.001
FEATURE [App::DocumentObjectGroupPython] P_element007  label="P_element : 0.002"  # scripted group (container) (typed FeaturePython)
  n = 0.002
FEATURE [App::DocumentObjectGroupPython] S_element017  label="S_element : 0.018"  # scripted group (container) (typed FeaturePython)
  n = 0.003
FEATURE [App::DocumentObjectGroupPython] Cl_element016  label="Cl_element : 0.589"  # scripted group (container) (typed FeaturePython)
  n = 0.001
FEATURE [App::DocumentObjectGroupPython] K_element006  label="K_element : 0.004"  # scripted group (container) (typed FeaturePython)
  n = 0.004
FEATURE [App::DocumentObjectGroupPython] G4_MUSCLE_SKELETAL_ICRP  # scripted group (container) (typed FeaturePython)
  Dunit = g/cm3
  Dvalue = 1.05
  Group = -> [H_element057,C_element063,N_element025,O_element065,Na_element011,P_element007,S_element017,Cl_element016,K_element006]
  conduct = 2
  density = 1
  expand = 3
  formula = G4_MUSCLE_SKELETAL_ICRP
  name = G4_MUSCLE_SKELETAL_ICRP
  specific = 4
FEATURE [App::DocumentObjectGroupPython] H_element058  label="H_element : 0.137"  # scripted group (container) (typed FeaturePython)
  n = 0.102102
FEATURE [App::DocumentObjectGroupPython] C_element064  label="C_element : 0.123"  # scripted group (container) (typed FeaturePython)
  n = 0.123123
FEATURE [App::DocumentObjectGroupPython] N_element026  label="N_element : 0.756"  # scripted group (container) (typed FeaturePython)
  n = 0.035035
FEATURE [App::DocumentObjectGroupPython] O_element066  label="O_element : 0.730"  # scripted group (container) (typed FeaturePython)
  n = 0.72973
FEATURE [App::DocumentObjectGroupPython] Na_element012  label="Na_element : 0.099"  # scripted group (container) (typed FeaturePython)
  n = 0.001001
FEATURE [App::DocumentObjectGroupPython] P_element008  label="P_element : 0.106"  # scripted group (container) (typed FeaturePython)
  n = 0.002002
FEATURE [App::DocumentObjectGroupPython] S_element018  label="S_element : 0.019"  # scripted group (container) (typed FeaturePython)
  n = 0.004004
FEATURE [App::DocumentObjectGroupPython] K_element007  label="K_element : 0.016"  # scripted group (container) (typed FeaturePython)
  n = 0.003003
FEATURE [App::DocumentObjectGroupPython] G4_MUSCLE_STRIATED_ICRU  # scripted group (container) (typed FeaturePython)
  Dunit = g/cm3
  Dvalue = 1.04
  Group = -> [H_element058,C_element064,N_element026,O_element066,Na_element012,P_element008,S_element018,K_element007]
  conduct = 2
  density = 1
  expand = 3
  formula = G4_MUSCLE_STRIATED_ICRU
  name = G4_MUSCLE_STRIATED_ICRU
  specific = 4
FEATURE [App::DocumentObjectGroupPython] H_element059  label="H_element : 0.098"  # scripted group (container) (typed FeaturePython)
  n = 0.0982341
FEATURE [App::DocumentObjectGroupPython] C_element065  label="C_element : 0.156"  # scripted group (container) (typed FeaturePython)
  n = 0.156214
FEATURE [App::DocumentObjectGroupPython] N_element027  label="N_element : 0.757"  # scripted group (container) (typed FeaturePython)
  n = 0.035451
FEATURE [App::DocumentObjectGroupPython] O_element067  label="O_element : 0.880"  # scripted group (container) (typed FeaturePython)
  n = 0.710101
FEATURE [App::DocumentObjectGroupPython] G4_MUSCLE_WITH_SUCROSE  # scripted group (container) (typed FeaturePython)
  Dunit = g/cm3
  Dvalue = 1.11
  Group = -> [H_element059,C_element065,N_element027,O_element067]
  conduct = 2
  density = 1
  expand = 3
  formula = G4_MUSCLE_WITH_SUCROSE
  name = G4_MUSCLE_WITH_SUCROSE
  specific = 4
FEATURE [App::DocumentObjectGroupPython] H_element060  label="H_element : 0.138"  # scripted group (container) (typed FeaturePython)
  n = 0.101969
FEATURE [App::DocumentObjectGroupPython] C_element066  label="C_element : 0.120"  # scripted group (container) (typed FeaturePython)
  n = 0.120058
FEATURE [App::DocumentObjectGroupPython] N_element028  label="N_element : 0.758"  # scripted group (container) (typed FeaturePython)
  n = 0.035451
FEATURE [App::DocumentObjectGroupPython] O_element068  label="O_element : 0.743"  # scripted group (container) (typed FeaturePython)
  n = 0.742522
FEATURE [App::DocumentObjectGroupPython] G4_MUSCLE_WITHOUT_SUCROSE  # scripted group (container) (typed FeaturePython)
  Dunit = g/cm3
  Dvalue = 1.07
  Group = -> [H_element060,C_element066,N_element028,O_element068]
  conduct = 2
  density = 1
  expand = 3
  formula = G4_MUSCLE_WITHOUT_SUCROSE
  name = G4_MUSCLE_WITHOUT_SUCROSE
  specific = 4
FEATURE [App::DocumentObjectGroupPython] C_element067  label="C_element : 10"  # scripted group (container) (typed FeaturePython)
  n = 10
  ref = C_element
FEATURE [App::DocumentObjectGroupPython] H_element061  label="H_element : 030"  # scripted group (container) (typed FeaturePython)
  n = 8
  ref = H_element
FEATURE [App::DocumentObjectGroupPython] G4_NAPHTHALENE  # scripted group (container) (typed FeaturePython)
  Dunit = g/cm3
  Dvalue = 1.145
  Group = -> [C_element067,H_element061]
  conduct = 2
  density = 1
  expand = 3
  formula = G4_NAPHTHALENE
  name = G4_NAPHTHALENE
  specific = 4
FEATURE [App::DocumentObjectGroupPython] C_element068  label="C_element : 034"  # scripted group (container) (typed FeaturePython)
  n = 6
  ref = C_element
FEATURE [App::DocumentObjectGroupPython] H_element062  label="H_element : 031"  # scripted group (container) (typed FeaturePython)
  n = 5
  ref = H_element
FEATURE [App::DocumentObjectGroupPython] N_element029  label="N_element : 012"  # scripted group (container) (typed FeaturePython)
  n = 1
  ref = N_element
FEATURE [App::DocumentObjectGroupPython] O_element069  label="O_element : 034"  # scripted group (container) (typed FeaturePython)
  n = 2
  ref = O_element
FEATURE [App::DocumentObjectGroupPython] G4_NITROBENZENE  # scripted group (container) (typed FeaturePython)
  Dunit = g/cm3
  Dvalue = 1.19867
  Group = -> [C_element068,H_element062,N_element029,O_element069]
  conduct = 2
  density = 1
  expand = 3
  formula = G4_NITROBENZENE
  name = G4_NITROBENZENE
  specific = 4
FEATURE [App::DocumentObjectGroupPython] N_element030  label="N_element : 013"  # scripted group (container) (typed FeaturePython)
  n = 2
  ref = N_element
FEATURE [App::DocumentObjectGroupPython] O_element070  label="O_element : 035"  # scripted group (container) (typed FeaturePython)
  n = 1
  ref = O_element
FEATURE [App::DocumentObjectGroupPython] G4_NITROUS_OXIDE  # scripted group (container) (typed FeaturePython)
  Dunit = g/cm3
  Dvalue = 0.00183094
  Group = -> [N_element030,O_element070]
  conduct = 2
  density = 1
  expand = 3
  formula = G4_NITROUS_OXIDE
  name = G4_NITROUS_OXIDE
  specific = 4
FEATURE [App::DocumentObjectGroupPython] H_element063  label="H_element : 0.104"  # scripted group (container) (typed FeaturePython)
  n = 0.103509
FEATURE [App::DocumentObjectGroupPython] C_element069  label="C_element : 0.648"  # scripted group (container) (typed FeaturePython)
  n = 0.648416
FEATURE [App::DocumentObjectGroupPython] N_element031  label="N_element : 0.100"  # scripted group (container) (typed FeaturePython)
  n = 0.0995361
FEATURE [App::DocumentObjectGroupPython] O_element071  label="O_element : 0.149"  # scripted group (container) (typed FeaturePython)
  n = 0.148539
FEATURE [App::DocumentObjectGroupPython] G4_NYLON_8062  label="G4_NYLON-8062"  # scripted group (container) (typed FeaturePython)
  Dunit = g/cm3
  Dvalue = 1.08
  Group = -> [H_element063,C_element069,N_element031,O_element071]
  conduct = 2
  density = 1
  expand = 3
  formula = G4_NYLON-8062
  name = G4_NYLON-8062
  specific = 4
FEATURE [App::DocumentObjectGroupPython] C_element070  label="C_element : 035"  # scripted group (container) (typed FeaturePython)
  n = 6
  ref = C_element
FEATURE [App::DocumentObjectGroupPython] H_element064  label="H_element : 11"  # scripted group (container) (typed FeaturePython)
  n = 11
  ref = H_element
FEATURE [App::DocumentObjectGroupPython] N_element032  label="N_element : 014"  # scripted group (container) (typed FeaturePython)
  n = 1
  ref = N_element
FEATURE [App::DocumentObjectGroupPython] O_element072  label="O_element : 036"  # scripted group (container) (typed FeaturePython)
  n = 1
  ref = O_element
FEATURE [App::DocumentObjectGroupPython] G4_NYLON_6_6  label="G4_NYLON-6-6"  # scripted group (container) (typed FeaturePython)
  Dunit = g/cm3
  Dvalue = 1.14
  Group = -> [C_element070,H_element064,N_element032,O_element072]
  conduct = 2
  density = 1
  expand = 3
  formula = G4_NYLON-6-6
  name = G4_NYLON-6-6
  specific = 4
FEATURE [App::DocumentObjectGroupPython] H_element065  label="H_element : 0.139"  # scripted group (container) (typed FeaturePython)
  n = 0.107062
FEATURE [App::DocumentObjectGroupPython] C_element071  label="C_element : 0.680"  # scripted group (container) (typed FeaturePython)
  n = 0.680449
FEATURE [App::DocumentObjectGroupPython] N_element033  label="N_element : 0.099"  # scripted group (container) (typed FeaturePython)
  n = 0.099189
FEATURE [App::DocumentObjectGroupPython] O_element073  label="O_element : 0.113"  # scripted group (container) (typed FeaturePython)
  n = 0.1133
FEATURE [App::DocumentObjectGroupPython] G4_NYLON_6_10  label="G4_NYLON-6-10"  # scripted group (container) (typed FeaturePython)
  Dunit = g/cm3
  Dvalue = 1.14
  Group = -> [H_element065,C_element071,N_element033,O_element073]
  conduct = 2
  density = 1
  expand = 3
  formula = G4_NYLON-6-10
  name = G4_NYLON-6-10
  specific = 4
FEATURE [App::DocumentObjectGroupPython] H_element066  label="H_element : 0.140"  # scripted group (container) (typed FeaturePython)
  n = 0.115476
FEATURE [App::DocumentObjectGroupPython] C_element072  label="C_element : 0.721"  # scripted group (container) (typed FeaturePython)
  n = 0.720818
FEATURE [App::DocumentObjectGroupPython] N_element034  label="N_element : 0.076"  # scripted group (container) (typed FeaturePython)
  n = 0.0764169
FEATURE [App::DocumentObjectGroupPython] O_element074  label="O_element : 0.087"  # scripted group (container) (typed FeaturePython)
  n = 0.0872889
FEATURE [App::DocumentObjectGroupPython] G4_NYLON_11_RILSAN  label="G4_NYLON-11_RILSAN"  # scripted group (container) (typed FeaturePython)
  Dunit = g/cm3
  Dvalue = 1.425
  Group = -> [H_element066,C_element072,N_element034,O_element074]
  conduct = 2
  density = 1
  expand = 3
  formula = G4_NYLON-11_RILSAN
  name = G4_NYLON-11_RILSAN
  specific = 4
FEATURE [App::DocumentObjectGroupPython] C_element073  label="C_element : 8"  # scripted group (container) (typed FeaturePython)
  n = 8
  ref = C_element
FEATURE [App::DocumentObjectGroupPython] H_element067  label="H_element : 18"  # scripted group (container) (typed FeaturePython)
  n = 18
  ref = H_element
FEATURE [App::DocumentObjectGroupPython] G4_OCTANE  # scripted group (container) (typed FeaturePython)
  Dunit = g/cm3
  Dvalue = 0.7026
  Group = -> [C_element073,H_element067]
  conduct = 2
  density = 1
  expand = 3
  formula = G4_OCTANE
  name = G4_OCTANE
  specific = 4
FEATURE [App::DocumentObjectGroupPython] C_element074  label="C_element : 25"  # scripted group (container) (typed FeaturePython)
  n = 25
  ref = C_element
FEATURE [App::DocumentObjectGroupPython] H_element068  label="H_element : 52"  # scripted group (container) (typed FeaturePython)
  n = 52
  ref = H_element
FEATURE [App::DocumentObjectGroupPython] G4_PARAFFIN  # scripted group (container) (typed FeaturePython)
  Dunit = g/cm3
  Dvalue = 0.93
  Group = -> [C_element074,H_element068]
  conduct = 2
  density = 1
  expand = 3
  formula = G4_PARAFFIN
  name = G4_PARAFFIN
  specific = 4
FEATURE [App::DocumentObjectGroupPython] C_element075  label="C_element : 036"  # scripted group (container) (typed FeaturePython)
  n = 5
  ref = C_element
FEATURE [App::DocumentObjectGroupPython] H_element069  label="H_element : 032"  # scripted group (container) (typed FeaturePython)
  n = 12
  ref = H_element
FEATURE [App::DocumentObjectGroupPython] G4_N_PENTANE  label="G4_N-PENTANE"  # scripted group (container) (typed FeaturePython)
  Dunit = g/cm3
  Dvalue = 0.6262
  Group = -> [C_element075,H_element069]
  conduct = 2
  density = 1
  expand = 3
  formula = G4_N-PENTANE
  name = G4_N-PENTANE
  specific = 4
FEATURE [App::DocumentObjectGroupPython] H_element070  label="H_element : 0.014"  # scripted group (container) (typed FeaturePython)
  n = 0.0141
FEATURE [App::DocumentObjectGroupPython] C_element076  label="C_element : 0.072"  # scripted group (container) (typed FeaturePython)
  n = 0.072261
FEATURE [App::DocumentObjectGroupPython] N_element035  label="N_element : 0.019"  # scripted group (container) (typed FeaturePython)
  n = 0.01932
FEATURE [App::DocumentObjectGroupPython] O_element075  label="O_element : 0.066"  # scripted group (container) (typed FeaturePython)
  n = 0.066101
FEATURE [App::DocumentObjectGroupPython] S_element019  label="S_element : 0.020"  # scripted group (container) (typed FeaturePython)
  n = 0.00189
FEATURE [App::DocumentObjectGroupPython] Br_element004  label="Br_element : 0.349"  # scripted group (container) (typed FeaturePython)
  n = 0.349103
FEATURE [App::DocumentObjectGroupPython] Ag_element001  label="Ag_element : 0.474"  # scripted group (container) (typed FeaturePython)
  n = 0.474105
FEATURE [App::DocumentObjectGroupPython] I_element005  label="I_element : 0.003"  # scripted group (container) (typed FeaturePython)
  n = 0.00312
FEATURE [App::DocumentObjectGroupPython] G4_PHOTO_EMULSION  # scripted group (container) (typed FeaturePython)
  Dunit = g/cm3
  Dvalue = 3.815
  Group = -> [H_element070,C_element076,N_element035,O_element075,S_element019,Br_element004,Ag_element001,I_element005]
  conduct = 2
  density = 1
  expand = 3
  formula = G4_PHOTO_EMULSION
  name = G4_PHOTO_EMULSION
  specific = 4
FEATURE [App::DocumentObjectGroupPython] C_element077  label="C_element : 9"  # scripted group (container) (typed FeaturePython)
  n = 9
  ref = C_element
FEATURE [App::DocumentObjectGroupPython] H_element071  label="H_element : 033"  # scripted group (container) (typed FeaturePython)
  n = 10
  ref = H_element
FEATURE [App::DocumentObjectGroupPython] G4_PLASTIC_SC_VINYLTOLUENE  # scripted group (container) (typed FeaturePython)
  Dunit = g/cm3
  Dvalue = 1.032
  Group = -> [C_element077,H_element071]
  conduct = 2
  density = 1
  expand = 3
  formula = G4_PLASTIC_SC_VINYLTOLUENE
  name = G4_PLASTIC_SC_VINYLTOLUENE
  specific = 4
FEATURE [App::DocumentObjectGroupPython] Pu_element001  label="Pu_element : 1"  # scripted group (container) (typed FeaturePython)
  n = 1
  ref = Pu_element
FEATURE [App::DocumentObjectGroupPython] O_element076  label="O_element : 037"  # scripted group (container) (typed FeaturePython)
  n = 2
  ref = O_element
FEATURE [App::DocumentObjectGroupPython] G4_PLUTONIUM_DIOXIDE  # scripted group (container) (typed FeaturePython)
  Dunit = g/cm3
  Dvalue = 11.46
  Group = -> [Pu_element001,O_element076]
  conduct = 2
  density = 1
  expand = 3
  formula = G4_PLUTONIUM_DIOXIDE
  name = G4_PLUTONIUM_DIOXIDE
  specific = 4
FEATURE [App::DocumentObjectGroupPython] C_element078  label="C_element : 037"  # scripted group (container) (typed FeaturePython)
  n = 3
  ref = C_element
FEATURE [App::DocumentObjectGroupPython] H_element072  label="H_element : 034"  # scripted group (container) (typed FeaturePython)
  n = 3
  ref = H_element
FEATURE [App::DocumentObjectGroupPython] N_element036  label="N_element : 015"  # scripted group (container) (typed FeaturePython)
  n = 1
  ref = N_element
FEATURE [App::DocumentObjectGroupPython] G4_POLYACRYLONITRILE  # scripted group (container) (typed FeaturePython)
  Dunit = g/cm3
  Dvalue = 1.17
  Group = -> [C_element078,H_element072,N_element036]
  conduct = 2
  density = 1
  expand = 3
  formula = G4_POLYACRYLONITRILE
  name = G4_POLYACRYLONITRILE
  specific = 4
FEATURE [App::DocumentObjectGroupPython] C_element079  label="C_element : 16"  # scripted group (container) (typed FeaturePython)
  n = 16
  ref = C_element
FEATURE [App::DocumentObjectGroupPython] H_element073  label="H_element : 035"  # scripted group (container) (typed FeaturePython)
  n = 14
  ref = H_element
FEATURE [App::DocumentObjectGroupPython] O_element077  label="O_element : 038"  # scripted group (container) (typed FeaturePython)
  n = 3
  ref = O_element
FEATURE [App::DocumentObjectGroupPython] G4_POLYCARBONATE  # scripted group (container) (typed FeaturePython)
  Dunit = g/cm3
  Dvalue = 1.2
  Group = -> [C_element079,H_element073,O_element077]
  conduct = 2
  density = 1
  expand = 3
  formula = G4_POLYCARBONATE
  name = G4_POLYCARBONATE
  specific = 4
FEATURE [App::DocumentObjectGroupPython] C_element080  label="C_element : 038"  # scripted group (container) (typed FeaturePython)
  n = 8
  ref = C_element
FEATURE [App::DocumentObjectGroupPython] H_element074  label="H_element : 036"  # scripted group (container) (typed FeaturePython)
  n = 7
  ref = H_element
FEATURE [App::DocumentObjectGroupPython] Cl_element017  label="Cl_element : 007"  # scripted group (container) (typed FeaturePython)
  n = 1
  ref = Cl_element
FEATURE [App::DocumentObjectGroupPython] G4_POLYCHLOROSTYRENE  # scripted group (container) (typed FeaturePython)
  Dunit = g/cm3
  Dvalue = 1.3
  Group = -> [C_element080,H_element074,Cl_element017]
  conduct = 2
  density = 1
  expand = 3
  formula = G4_POLYCHLOROSTYRENE
  name = G4_POLYCHLOROSTYRENE
  specific = 4
FEATURE [App::DocumentObjectGroupPython] C_element081  label="C_element : 039"  # scripted group (container) (typed FeaturePython)
  n = 1
  ref = C_element
FEATURE [App::DocumentObjectGroupPython] H_element075  label="H_element : 037"  # scripted group (container) (typed FeaturePython)
  n = 2
  ref = H_element
FEATURE [App::DocumentObjectGroupPython] G4_POLYETHYLENE  # scripted group (container) (typed FeaturePython)
  Dunit = g/cm3
  Dvalue = 0.94
  Group = -> [C_element081,H_element075]
  conduct = 2
  density = 1
  expand = 3
  formula = G4_POLYETHYLENE
  name = G4_POLYETHYLENE
  specific = 4
FEATURE [App::DocumentObjectGroupPython] C_element082  label="C_element : 040"  # scripted group (container) (typed FeaturePython)
  n = 10
  ref = C_element
FEATURE [App::DocumentObjectGroupPython] H_element076  label="H_element : 038"  # scripted group (container) (typed FeaturePython)
  n = 8
  ref = H_element
FEATURE [App::DocumentObjectGroupPython] O_element078  label="O_element : 039"  # scripted group (container) (typed FeaturePython)
  n = 4
  ref = O_element
FEATURE [App::DocumentObjectGroupPython] G4_MYLAR  # scripted group (container) (typed FeaturePython)
  Dunit = g/cm3
  Dvalue = 1.4
  Group = -> [C_element082,H_element076,O_element078]
  conduct = 2
  density = 1
  expand = 3
  formula = G4_MYLAR
  name = G4_MYLAR
  specific = 4
FEATURE [App::DocumentObjectGroupPython] C_element083  label="C_element : 041"  # scripted group (container) (typed FeaturePython)
  n = 5
  ref = C_element
FEATURE [App::DocumentObjectGroupPython] H_element077  label="H_element : 039"  # scripted group (container) (typed FeaturePython)
  n = 8
  ref = H_element
FEATURE [App::DocumentObjectGroupPython] O_element079  label="O_element : 040"  # scripted group (container) (typed FeaturePython)
  n = 2
  ref = O_element
FEATURE [App::DocumentObjectGroupPython] G4_PLEXIGLASS  # scripted group (container) (typed FeaturePython)
  Dunit = g/cm3
  Dvalue = 1.19
  Group = -> [C_element083,H_element077,O_element079]
  conduct = 2
  density = 1
  expand = 3
  formula = G4_PLEXIGLASS
  name = G4_PLEXIGLASS
  specific = 4
FEATURE [App::DocumentObjectGroupPython] C_element084  label="C_element : 042"  # scripted group (container) (typed FeaturePython)
  n = 1
  ref = C_element
FEATURE [App::DocumentObjectGroupPython] H_element078  label="H_element : 040"  # scripted group (container) (typed FeaturePython)
  n = 2
  ref = H_element
FEATURE [App::DocumentObjectGroupPython] O_element080  label="O_element : 041"  # scripted group (container) (typed FeaturePython)
  n = 1
  ref = O_element
FEATURE [App::DocumentObjectGroupPython] G4_POLYOXYMETHYLENE  # scripted group (container) (typed FeaturePython)
  Dunit = g/cm3
  Dvalue = 1.425
  Group = -> [C_element084,H_element078,O_element080]
  conduct = 2
  density = 1
  expand = 3
  formula = G4_POLYOXYMETHYLENE
  name = G4_POLYOXYMETHYLENE
  specific = 4
FEATURE [App::DocumentObjectGroupPython] C_element085  label="C_element : 043"  # scripted group (container) (typed FeaturePython)
  n = 2
  ref = C_element
FEATURE [App::DocumentObjectGroupPython] H_element079  label="H_element : 041"  # scripted group (container) (typed FeaturePython)
  n = 4
  ref = H_element
FEATURE [App::DocumentObjectGroupPython] G4_POLYPROPYLENE  # scripted group (container) (typed FeaturePython)
  Dunit = g/cm3
  Dvalue = 0.9
  Group = -> [C_element085,H_element079]
  conduct = 2
  density = 1
  expand = 3
  formula = G4_POLYPROPYLENE
  name = G4_POLYPROPYLENE
  specific = 4
FEATURE [App::DocumentObjectGroupPython] C_element086  label="C_element : 044"  # scripted group (container) (typed FeaturePython)
  n = 8
  ref = C_element
FEATURE [App::DocumentObjectGroupPython] H_element080  label="H_element : 042"  # scripted group (container) (typed FeaturePython)
  n = 8
  ref = H_element
FEATURE [App::DocumentObjectGroupPython] G4_POLYSTYRENE  # scripted group (container) (typed FeaturePython)
  Dunit = g/cm3
  Dvalue = 1.06
  Group = -> [C_element086,H_element080]
  conduct = 2
  density = 1
  expand = 3
  formula = G4_POLYSTYRENE
  name = G4_POLYSTYRENE
  specific = 4
FEATURE [App::DocumentObjectGroupPython] C_element087  label="C_element : 045"  # scripted group (container) (typed FeaturePython)
  n = 2
  ref = C_element
FEATURE [App::DocumentObjectGroupPython] F_element014  label="F_element : 4"  # scripted group (container) (typed FeaturePython)
  n = 4
  ref = F_element
FEATURE [App::DocumentObjectGroupPython] G4_TEFLON  # scripted group (container) (typed FeaturePython)
  Dunit = g/cm3
  Dvalue = 2.2
  Group = -> [C_element087,F_element014]
  conduct = 2
  density = 1
  expand = 3
  formula = G4_TEFLON
  name = G4_TEFLON
  specific = 4
FEATURE [App::DocumentObjectGroupPython] C_element088  label="C_element : 046"  # scripted group (container) (typed FeaturePython)
  n = 2
  ref = C_element
FEATURE [App::DocumentObjectGroupPython] F_element015  label="F_element : 006"  # scripted group (container) (typed FeaturePython)
  n = 3
  ref = F_element
FEATURE [App::DocumentObjectGroupPython] Cl_element018  label="Cl_element : 008"  # scripted group (container) (typed FeaturePython)
  n = 1
  ref = Cl_element
FEATURE [App::DocumentObjectGroupPython] G4_POLYTRIFLUOROCHLOROETHYLENE  # scripted group (container) (typed FeaturePython)
  Dunit = g/cm3
  Dvalue = 2.1
  Group = -> [C_element088,F_element015,Cl_element018]
  conduct = 2
  density = 1
  expand = 3
  formula = G4_POLYTRIFLUOROCHLOROETHYLENE
  name = G4_POLYTRIFLUOROCHLOROETHYLENE
  specific = 4
FEATURE [App::DocumentObjectGroupPython] C_element089  label="C_element : 047"  # scripted group (container) (typed FeaturePython)
  n = 4
  ref = C_element
FEATURE [App::DocumentObjectGroupPython] H_element081  label="H_element : 043"  # scripted group (container) (typed FeaturePython)
  n = 6
  ref = H_element
FEATURE [App::DocumentObjectGroupPython] O_element081  label="O_element : 042"  # scripted group (container) (typed FeaturePython)
  n = 2
  ref = O_element
FEATURE [App::DocumentObjectGroupPython] G4_POLYVINYL_ACETATE  # scripted group (container) (typed FeaturePython)
  Dunit = g/cm3
  Dvalue = 1.19
  Group = -> [C_element089,H_element081,O_element081]
  conduct = 2
  density = 1
  expand = 3
  formula = G4_POLYVINYL_ACETATE
  name = G4_POLYVINYL_ACETATE
  specific = 4
FEATURE [App::DocumentObjectGroupPython] C_element090  label="C_element : 048"  # scripted group (container) (typed FeaturePython)
  n = 2
  ref = C_element
FEATURE [App::DocumentObjectGroupPython] H_element082  label="H_element : 044"  # scripted group (container) (typed FeaturePython)
  n = 4
  ref = H_element
FEATURE [App::DocumentObjectGroupPython] O_element082  label="O_element : 043"  # scripted group (container) (typed FeaturePython)
  n = 1
  ref = O_element
FEATURE [App::DocumentObjectGroupPython] G4_POLYVINYL_ALCOHOL  # scripted group (container) (typed FeaturePython)
  Dunit = g/cm3
  Dvalue = 1.3
  Group = -> [C_element090,H_element082,O_element082]
  conduct = 2
  density = 1
  expand = 3
  formula = G4_POLYVINYL_ALCOHOL
  name = G4_POLYVINYL_ALCOHOL
  specific = 4
FEATURE [App::DocumentObjectGroupPython] C_element091  label="C_element : 049"  # scripted group (container) (typed FeaturePython)
  n = 8
  ref = C_element
FEATURE [App::DocumentObjectGroupPython] H_element083  label="H_element : 045"  # scripted group (container) (typed FeaturePython)
  n = 14
  ref = H_element
FEATURE [App::DocumentObjectGroupPython] O_element083  label="O_element : 044"  # scripted group (container) (typed FeaturePython)
  n = 2
  ref = O_element
FEATURE [App::DocumentObjectGroupPython] G4_POLYVINYL_BUTYRAL  # scripted group (container) (typed FeaturePython)
  Dunit = g/cm3
  Dvalue = 1.12
  Group = -> [C_element091,H_element083,O_element083]
  conduct = 2
  density = 1
  expand = 3
  formula = G4_POLYVINYL_BUTYRAL
  name = G4_POLYVINYL_BUTYRAL
  specific = 4
FEATURE [App::DocumentObjectGroupPython] C_element092  label="C_element : 050"  # scripted group (container) (typed FeaturePython)
  n = 2
  ref = C_element
FEATURE [App::DocumentObjectGroupPython] H_element084  label="H_element : 046"  # scripted group (container) (typed FeaturePython)
  n = 3
  ref = H_element
FEATURE [App::DocumentObjectGroupPython] Cl_element019  label="Cl_element : 009"  # scripted group (container) (typed FeaturePython)
  n = 1
  ref = Cl_element
FEATURE [App::DocumentObjectGroupPython] G4_POLYVINYL_CHLORIDE  # scripted group (container) (typed FeaturePython)
  Dunit = g/cm3
  Dvalue = 1.3
  Group = -> [C_element092,H_element084,Cl_element019]
  conduct = 2
  density = 1
  expand = 3
  formula = G4_POLYVINYL_CHLORIDE
  name = G4_POLYVINYL_CHLORIDE
  specific = 4
FEATURE [App::DocumentObjectGroupPython] C_element093  label="C_element : 051"  # scripted group (container) (typed FeaturePython)
  n = 2
  ref = C_element
FEATURE [App::DocumentObjectGroupPython] H_element085  label="H_element : 047"  # scripted group (container) (typed FeaturePython)
  n = 2
  ref = H_element
FEATURE [App::DocumentObjectGroupPython] Cl_element020  label="Cl_element : 010"  # scripted group (container) (typed FeaturePython)
  n = 2
  ref = Cl_element
FEATURE [App::DocumentObjectGroupPython] G4_POLYVINYLIDENE_CHLORIDE  # scripted group (container) (typed FeaturePython)
  Dunit = g/cm3
  Dvalue = 1.7
  Group = -> [C_element093,H_element085,Cl_element020]
  conduct = 2
  density = 1
  expand = 3
  formula = G4_POLYVINYLIDENE_CHLORIDE
  name = G4_POLYVINYLIDENE_CHLORIDE
  specific = 4
FEATURE [App::DocumentObjectGroupPython] C_element094  label="C_element : 052"  # scripted group (container) (typed FeaturePython)
  n = 2
  ref = C_element
FEATURE [App::DocumentObjectGroupPython] H_element086  label="H_element : 048"  # scripted group (container) (typed FeaturePython)
  n = 2
  ref = H_element
FEATURE [App::DocumentObjectGroupPython] F_element016  label="F_element : 007"  # scripted group (container) (typed FeaturePython)
  n = 2
  ref = F_element
FEATURE [App::DocumentObjectGroupPython] G4_POLYVINYLIDENE_FLUORIDE  # scripted group (container) (typed FeaturePython)
  Dunit = g/cm3
  Dvalue = 1.76
  Group = -> [C_element094,H_element086,F_element016]
  conduct = 2
  density = 1
  expand = 3
  formula = G4_POLYVINYLIDENE_FLUORIDE
  name = G4_POLYVINYLIDENE_FLUORIDE
  specific = 4
FEATURE [App::DocumentObjectGroupPython] C_element095  label="C_element : 053"  # scripted group (container) (typed FeaturePython)
  n = 6
  ref = C_element
FEATURE [App::DocumentObjectGroupPython] H_element087  label="H_element : 9"  # scripted group (container) (typed FeaturePython)
  n = 9
  ref = H_element
FEATURE [App::DocumentObjectGroupPython] N_element037  label="N_element : 016"  # scripted group (container) (typed FeaturePython)
  n = 1
  ref = N_element
FEATURE [App::DocumentObjectGroupPython] O_element084  label="O_element : 045"  # scripted group (container) (typed FeaturePython)
  n = 1
  ref = O_element
FEATURE [App::DocumentObjectGroupPython] G4_POLYVINYL_PYRROLIDONE  # scripted group (container) (typed FeaturePython)
  Dunit = g/cm3
  Dvalue = 1.25
  Group = -> [C_element095,H_element087,N_element037,O_element084]
  conduct = 2
  density = 1
  expand = 3
  formula = G4_POLYVINYL_PYRROLIDONE
  name = G4_POLYVINYL_PYRROLIDONE
  specific = 4
FEATURE [App::DocumentObjectGroupPython] K_element008  label="K_element : 1"  # scripted group (container) (typed FeaturePython)
  n = 1
  ref = K_element
FEATURE [App::DocumentObjectGroupPython] I_element006  label="I_element : 003"  # scripted group (container) (typed FeaturePython)
  n = 1
  ref = I_element
FEATURE [App::DocumentObjectGroupPython] G4_POTASSIUM_IODIDE  # scripted group (container) (typed FeaturePython)
  Dunit = g/cm3
  Dvalue = 3.13
  Group = -> [K_element008,I_element006]
  conduct = 2
  density = 1
  expand = 3
  formula = G4_POTASSIUM_IODIDE
  name = G4_POTASSIUM_IODIDE
  specific = 4
FEATURE [App::DocumentObjectGroupPython] K_element009  label="K_element : 2"  # scripted group (container) (typed FeaturePython)
  n = 2
  ref = K_element
FEATURE [App::DocumentObjectGroupPython] O_element085  label="O_element : 046"  # scripted group (container) (typed FeaturePython)
  n = 1
  ref = O_element
FEATURE [App::DocumentObjectGroupPython] G4_POTASSIUM_OXIDE  # scripted group (container) (typed FeaturePython)
  Dunit = g/cm3
  Dvalue = 2.32
  Group = -> [K_element009,O_element085]
  conduct = 2
  density = 1
  expand = 3
  formula = G4_POTASSIUM_OXIDE
  name = G4_POTASSIUM_OXIDE
  specific = 4
FEATURE [App::DocumentObjectGroupPython] C_element096  label="C_element : 054"  # scripted group (container) (typed FeaturePython)
  n = 3
  ref = C_element
FEATURE [App::DocumentObjectGroupPython] H_element088  label="H_element : 049"  # scripted group (container) (typed FeaturePython)
  n = 8
  ref = H_element
FEATURE [App::DocumentObjectGroupPython] G4_PROPANE  # scripted group (container) (typed FeaturePython)
  Dunit = g/cm3
  Dvalue = 0.00187939
  Group = -> [C_element096,H_element088]
  conduct = 2
  density = 1
  expand = 3
  formula = G4_PROPANE
  name = G4_PROPANE
  specific = 4
FEATURE [App::DocumentObjectGroupPython] C_element097  label="C_element : 055"  # scripted group (container) (typed FeaturePython)
  n = 3
  ref = C_element
FEATURE [App::DocumentObjectGroupPython] H_element089  label="H_element : 050"  # scripted group (container) (typed FeaturePython)
  n = 8
  ref = H_element
FEATURE [App::DocumentObjectGroupPython] G4_lPROPANE  # scripted group (container) (typed FeaturePython)
  Dunit = g/cm3
  Dvalue = 0.43
  Group = -> [C_element097,H_element089]
  conduct = 2
  density = 1
  expand = 3
  formula = G4_lPROPANE
  name = G4_lPROPANE
  specific = 4
FEATURE [App::DocumentObjectGroupPython] C_element098  label="C_element : 056"  # scripted group (container) (typed FeaturePython)
  n = 3
  ref = C_element
FEATURE [App::DocumentObjectGroupPython] H_element090  label="H_element : 051"  # scripted group (container) (typed FeaturePython)
  n = 8
  ref = H_element
FEATURE [App::DocumentObjectGroupPython] O_element086  label="O_element : 047"  # scripted group (container) (typed FeaturePython)
  n = 1
  ref = O_element
FEATURE [App::DocumentObjectGroupPython] G4_N_PROPYL_ALCOHOL  label="G4_N-PROPYL_ALCOHOL"  # scripted group (container) (typed FeaturePython)
  Dunit = g/cm3
  Dvalue = 0.8035
  Group = -> [C_element098,H_element090,O_element086]
  conduct = 2
  density = 1
  expand = 3
  formula = G4_N-PROPYL_ALCOHOL
  name = G4_N-PROPYL_ALCOHOL
  specific = 4
FEATURE [App::DocumentObjectGroupPython] C_element099  label="C_element : 057"  # scripted group (container) (typed FeaturePython)
  n = 5
  ref = C_element
FEATURE [App::DocumentObjectGroupPython] H_element091  label="H_element : 052"  # scripted group (container) (typed FeaturePython)
  n = 5
  ref = H_element
FEATURE [App::DocumentObjectGroupPython] N_element038  label="N_element : 017"  # scripted group (container) (typed FeaturePython)
  n = 1
  ref = N_element
FEATURE [App::DocumentObjectGroupPython] G4_PYRIDINE  # scripted group (container) (typed FeaturePython)
  Dunit = g/cm3
  Dvalue = 0.9819
  Group = -> [C_element099,H_element091,N_element038]
  conduct = 2
  density = 1
  expand = 3
  formula = G4_PYRIDINE
  name = G4_PYRIDINE
  specific = 4
FEATURE [App::DocumentObjectGroupPython] H_element092  label="H_element : 0.144"  # scripted group (container) (typed FeaturePython)
  n = 0.143711
FEATURE [App::DocumentObjectGroupPython] C_element100  label="C_element : 0.856"  # scripted group (container) (typed FeaturePython)
  n = 0.856289
FEATURE [App::DocumentObjectGroupPython] G4_RUBBER_BUTYL  # scripted group (container) (typed FeaturePython)
  Dunit = g/cm3
  Dvalue = 0.92
  Group = -> [H_element092,C_element100]
  conduct = 2
  density = 1
  expand = 3
  formula = G4_RUBBER_BUTYL
  name = G4_RUBBER_BUTYL
  specific = 4
FEATURE [App::DocumentObjectGroupPython] H_element093  label="H_element : 0.118"  # scripted group (container) (typed FeaturePython)
  n = 0.118371
FEATURE [App::DocumentObjectGroupPython] C_element101  label="C_element : 0.882"  # scripted group (container) (typed FeaturePython)
  n = 0.881629
FEATURE [App::DocumentObjectGroupPython] G4_RUBBER_NATURAL  # scripted group (container) (typed FeaturePython)
  Dunit = g/cm3
  Dvalue = 0.92
  Group = -> [H_element093,C_element101]
  conduct = 2
  density = 1
  expand = 3
  formula = G4_RUBBER_NATURAL
  name = G4_RUBBER_NATURAL
  specific = 4
FEATURE [App::DocumentObjectGroupPython] H_element094  label="H_element : 0.145"  # scripted group (container) (typed FeaturePython)
  n = 0.05692
FEATURE [App::DocumentObjectGroupPython] C_element102  label="C_element : 0.543"  # scripted group (container) (typed FeaturePython)
  n = 0.542646
FEATURE [App::DocumentObjectGroupPython] Cl_element021  label="Cl_element : 0.400"  # scripted group (container) (typed FeaturePython)
  n = 0.400434
FEATURE [App::DocumentObjectGroupPython] G4_RUBBER_NEOPRENE  # scripted group (container) (typed FeaturePython)
  Dunit = g/cm3
  Dvalue = 1.23
  Group = -> [H_element094,C_element102,Cl_element021]
  conduct = 2
  density = 1
  expand = 3
  formula = G4_RUBBER_NEOPRENE
  name = G4_RUBBER_NEOPRENE
  specific = 4
FEATURE [App::DocumentObjectGroupPython] Si_element006  label="Si_element : 1"  # scripted group (container) (typed FeaturePython)
  n = 1
  ref = Si_element
FEATURE [App::DocumentObjectGroupPython] O_element087  label="O_element : 048"  # scripted group (container) (typed FeaturePython)
  n = 2
  ref = O_element
FEATURE [App::DocumentObjectGroupPython] G4_SILICON_DIOXIDE  # scripted group (container) (typed FeaturePython)
  Dunit = g/cm3
  Dvalue = 2.32
  Group = -> [Si_element006,O_element087]
  conduct = 2
  density = 1
  expand = 3
  formula = G4_SILICON_DIOXIDE
  name = G4_SILICON_DIOXIDE
  specific = 4
FEATURE [App::DocumentObjectGroupPython] Ag_element002  label="Ag_element : 1"  # scripted group (container) (typed FeaturePython)
  n = 1
  ref = Ag_element
FEATURE [App::DocumentObjectGroupPython] Br_element005  label="Br_element : 003"  # scripted group (container) (typed FeaturePython)
  n = 1
  ref = Br_element
FEATURE [App::DocumentObjectGroupPython] G4_SILVER_BROMIDE  # scripted group (container) (typed FeaturePython)
  Dunit = g/cm3
  Dvalue = 6.473
  Group = -> [Ag_element002,Br_element005]
  conduct = 2
  density = 1
  expand = 3
  formula = G4_SILVER_BROMIDE
  name = G4_SILVER_BROMIDE
  specific = 4
FEATURE [App::DocumentObjectGroupPython] Ag_element003  label="Ag_element : 002"  # scripted group (container) (typed FeaturePython)
  n = 1
  ref = Ag_element
FEATURE [App::DocumentObjectGroupPython] Cl_element022  label="Cl_element : 011"  # scripted group (container) (typed FeaturePython)
  n = 1
  ref = Cl_element
FEATURE [App::DocumentObjectGroupPython] G4_SILVER_CHLORIDE  # scripted group (container) (typed FeaturePython)
  Dunit = g/cm3
  Dvalue = 5.56
  Group = -> [Ag_element003,Cl_element022]
  conduct = 2
  density = 1
  expand = 3
  formula = G4_SILVER_CHLORIDE
  name = G4_SILVER_CHLORIDE
  specific = 4
FEATURE [App::DocumentObjectGroupPython] Br_element006  label="Br_element : 0.423"  # scripted group (container) (typed FeaturePython)
  n = 0.422895
FEATURE [App::DocumentObjectGroupPython] Ag_element004  label="Ag_element : 0.574"  # scripted group (container) (typed FeaturePython)
  n = 0.573748
FEATURE [App::DocumentObjectGroupPython] I_element007  label="I_element : 0.649"  # scripted group (container) (typed FeaturePython)
  n = 0.003357
FEATURE [App::DocumentObjectGroupPython] G4_SILVER_HALIDES  # scripted group (container) (typed FeaturePython)
  Dunit = g/cm3
  Dvalue = 6.47
  Group = -> [Br_element006,Ag_element004,I_element007]
  conduct = 2
  density = 1
  expand = 3
  formula = G4_SILVER_HALIDES
  name = G4_SILVER_HALIDES
  specific = 4
FEATURE [App::DocumentObjectGroupPython] Ag_element005  label="Ag_element : 003"  # scripted group (container) (typed FeaturePython)
  n = 1
  ref = Ag_element
FEATURE [App::DocumentObjectGroupPython] I_element008  label="I_element : 004"  # scripted group (container) (typed FeaturePython)
  n = 1
  ref = I_element
FEATURE [App::DocumentObjectGroupPython] G4_SILVER_IODIDE  # scripted group (container) (typed FeaturePython)
  Dunit = g/cm3
  Dvalue = 6.01
  Group = -> [Ag_element005,I_element008]
  conduct = 2
  density = 1
  expand = 3
  formula = G4_SILVER_IODIDE
  name = G4_SILVER_IODIDE
  specific = 4
FEATURE [App::DocumentObjectGroupPython] H_element095  label="H_element : 0.100"  # scripted group (container) (typed FeaturePython)
  n = 0.1
FEATURE [App::DocumentObjectGroupPython] C_element103  label="C_element : 0.204"  # scripted group (container) (typed FeaturePython)
  n = 0.204
FEATURE [App::DocumentObjectGroupPython] N_element039  label="N_element : 0.759"  # scripted group (container) (typed FeaturePython)
  n = 0.042
FEATURE [App::DocumentObjectGroupPython] O_element088  label="O_element : 0.645"  # scripted group (container) (typed FeaturePython)
  n = 0.645
FEATURE [App::DocumentObjectGroupPython] Na_element013  label="Na_element : 0.100"  # scripted group (container) (typed FeaturePython)
  n = 0.002
FEATURE [App::DocumentObjectGroupPython] P_element009  label="P_element : 0.107"  # scripted group (container) (typed FeaturePython)
  n = 0.001
FEATURE [App::DocumentObjectGroupPython] S_element020  label="S_element : 0.021"  # scripted group (container) (typed FeaturePython)
  n = 0.002
FEATURE [App::DocumentObjectGroupPython] Cl_element023  label="Cl_element : 0.590"  # scripted group (container) (typed FeaturePython)
  n = 0.003
FEATURE [App::DocumentObjectGroupPython] K_element010  label="K_element : 0.001"  # scripted group (container) (typed FeaturePython)
  n = 0.001
FEATURE [App::DocumentObjectGroupPython] G4_SKIN_ICRP  # scripted group (container) (typed FeaturePython)
  Dunit = g/cm3
  Dvalue = 1.09
  Group = -> [H_element095,C_element103,N_element039,O_element088,Na_element013,P_element009,S_element020,Cl_element023,K_element010]
  conduct = 2
  density = 1
  expand = 3
  formula = G4_SKIN_ICRP
  name = G4_SKIN_ICRP
  specific = 4
FEATURE [App::DocumentObjectGroupPython] Na_element014  label="Na_element : 2"  # scripted group (container) (typed FeaturePython)
  n = 2
  ref = Na_element
FEATURE [App::DocumentObjectGroupPython] C_element104  label="C_element : 058"  # scripted group (container) (typed FeaturePython)
  n = 1
  ref = C_element
FEATURE [App::DocumentObjectGroupPython] O_element089  label="O_element : 049"  # scripted group (container) (typed FeaturePython)
  n = 3
  ref = O_element
FEATURE [App::DocumentObjectGroupPython] G4_SODIUM_CARBONATE  # scripted group (container) (typed FeaturePython)
  Dunit = g/cm3
  Dvalue = 2.532
  Group = -> [Na_element014,C_element104,O_element089]
  conduct = 2
  density = 1
  expand = 3
  formula = G4_SODIUM_CARBONATE
  name = G4_SODIUM_CARBONATE
  specific = 4
FEATURE [App::DocumentObjectGroupPython] Na_element015  label="Na_element : 1"  # scripted group (container) (typed FeaturePython)
  n = 1
  ref = Na_element
FEATURE [App::DocumentObjectGroupPython] I_element009  label="I_element : 005"  # scripted group (container) (typed FeaturePython)
  n = 1
  ref = I_element
FEATURE [App::DocumentObjectGroupPython] G4_SODIUM_IODIDE  # scripted group (container) (typed FeaturePython)
  Dunit = g/cm3
  Dvalue = 3.667
  Group = -> [Na_element015,I_element009]
  conduct = 2
  density = 1
  expand = 3
  formula = G4_SODIUM_IODIDE
  name = G4_SODIUM_IODIDE
  specific = 4
FEATURE [App::DocumentObjectGroupPython] Na_element016  label="Na_element : 003"  # scripted group (container) (typed FeaturePython)
  n = 2
  ref = Na_element
FEATURE [App::DocumentObjectGroupPython] O_element090  label="O_element : 050"  # scripted group (container) (typed FeaturePython)
  n = 1
  ref = O_element
FEATURE [App::DocumentObjectGroupPython] G4_SODIUM_MONOXIDE  # scripted group (container) (typed FeaturePython)
  Dunit = g/cm3
  Dvalue = 2.27
  Group = -> [Na_element016,O_element090]
  conduct = 2
  density = 1
  expand = 3
  formula = G4_SODIUM_MONOXIDE
  name = G4_SODIUM_MONOXIDE
  specific = 4
FEATURE [App::DocumentObjectGroupPython] Na_element017  label="Na_element : 004"  # scripted group (container) (typed FeaturePython)
  n = 1
  ref = Na_element
FEATURE [App::DocumentObjectGroupPython] N_element040  label="N_element : 018"  # scripted group (container) (typed FeaturePython)
  n = 1
  ref = N_element
FEATURE [App::DocumentObjectGroupPython] O_element091  label="O_element : 051"  # scripted group (container) (typed FeaturePython)
  n = 3
  ref = O_element
FEATURE [App::DocumentObjectGroupPython] G4_SODIUM_NITRATE  # scripted group (container) (typed FeaturePython)
  Dunit = g/cm3
  Dvalue = 2.261
  Group = -> [Na_element017,N_element040,O_element091]
  conduct = 2
  density = 1
  expand = 3
  formula = G4_SODIUM_NITRATE
  name = G4_SODIUM_NITRATE
  specific = 4
FEATURE [App::DocumentObjectGroupPython] C_element105  label="C_element : 059"  # scripted group (container) (typed FeaturePython)
  n = 14
  ref = C_element
FEATURE [App::DocumentObjectGroupPython] H_element096  label="H_element : 053"  # scripted group (container) (typed FeaturePython)
  n = 12
  ref = H_element
FEATURE [App::DocumentObjectGroupPython] G4_STILBENE  # scripted group (container) (typed FeaturePython)
  Dunit = g/cm3
  Dvalue = 0.9707
  Group = -> [C_element105,H_element096]
  conduct = 2
  density = 1
  expand = 3
  formula = G4_STILBENE
  name = G4_STILBENE
  specific = 4
FEATURE [App::DocumentObjectGroupPython] C_element106  label="C_element : 12"  # scripted group (container) (typed FeaturePython)
  n = 12
  ref = C_element
FEATURE [App::DocumentObjectGroupPython] H_element097  label="H_element : 22"  # scripted group (container) (typed FeaturePython)
  n = 22
  ref = H_element
FEATURE [App::DocumentObjectGroupPython] O_element092  label="O_element : 11"  # scripted group (container) (typed FeaturePython)
  n = 11
  ref = O_element
FEATURE [App::DocumentObjectGroupPython] G4_SUCROSE  # scripted group (container) (typed FeaturePython)
  Dunit = g/cm3
  Dvalue = 1.5805
  Group = -> [C_element106,H_element097,O_element092]
  conduct = 2
  density = 1
  expand = 3
  formula = G4_SUCROSE
  name = G4_SUCROSE
  specific = 4
FEATURE [App::DocumentObjectGroupPython] C_element107  label="C_element : 18"  # scripted group (container) (typed FeaturePython)
  n = 18
  ref = C_element
FEATURE [App::DocumentObjectGroupPython] H_element098  label="H_element : 054"  # scripted group (container) (typed FeaturePython)
  n = 14
  ref = H_element
FEATURE [App::DocumentObjectGroupPython] G4_TERPHENYL  # scripted group (container) (typed FeaturePython)
  Dunit = g/cm3
  Dvalue = 1.24
  Group = -> [C_element107,H_element098]
  conduct = 2
  density = 1
  expand = 3
  formula = G4_TERPHENYL
  name = G4_TERPHENYL
  specific = 4
FEATURE [App::DocumentObjectGroupPython] H_element099  label="H_element : 0.146"  # scripted group (container) (typed FeaturePython)
  n = 0.106
FEATURE [App::DocumentObjectGroupPython] C_element108  label="C_element : 0.883"  # scripted group (container) (typed FeaturePython)
  n = 0.099
FEATURE [App::DocumentObjectGroupPython] N_element041  label="N_element : 0.020"  # scripted group (container) (typed FeaturePython)
  n = 0.02
FEATURE [App::DocumentObjectGroupPython] O_element093  label="O_element : 0.766"  # scripted group (container) (typed FeaturePython)
  n = 0.766
FEATURE [App::DocumentObjectGroupPython] Na_element018  label="Na_element : 0.101"  # scripted group (container) (typed FeaturePython)
  n = 0.002
FEATURE [App::DocumentObjectGroupPython] P_element010  label="P_element : 0.108"  # scripted group (container) (typed FeaturePython)
  n = 0.001
FEATURE [App::DocumentObjectGroupPython] S_element021  label="S_element : 0.022"  # scripted group (container) (typed FeaturePython)
  n = 0.002
FEATURE [App::DocumentObjectGroupPython] Cl_element024  label="Cl_element : 0.002"  # scripted group (container) (typed FeaturePython)
  n = 0.002
FEATURE [App::DocumentObjectGroupPython] K_element011  label="K_element : 0.017"  # scripted group (container) (typed FeaturePython)
  n = 0.002
FEATURE [App::DocumentObjectGroupPython] G4_TESTIS_ICRP  # scripted group (container) (typed FeaturePython)
  Dunit = g/cm3
  Dvalue = 1.04
  Group = -> [H_element099,C_element108,N_element041,O_element093,Na_element018,P_element010,S_element021,Cl_element024,K_element011]
  conduct = 2
  density = 1
  expand = 3
  formula = G4_TESTIS_ICRP
  name = G4_TESTIS_ICRP
  specific = 4
FEATURE [App::DocumentObjectGroupPython] C_element109  label="C_element : 060"  # scripted group (container) (typed FeaturePython)
  n = 2
  ref = C_element
FEATURE [App::DocumentObjectGroupPython] Cl_element025  label="Cl_element : 012"  # scripted group (container) (typed FeaturePython)
  n = 4
  ref = Cl_element
FEATURE [App::DocumentObjectGroupPython] G4_TETRACHLOROETHYLENE  # scripted group (container) (typed FeaturePython)
  Dunit = g/cm3
  Dvalue = 1.625
  Group = -> [C_element109,Cl_element025]
  conduct = 2
  density = 1
  expand = 3
  formula = G4_TETRACHLOROETHYLENE
  name = G4_TETRACHLOROETHYLENE
  specific = 4
FEATURE [App::DocumentObjectGroupPython] Tl_element001  label="Tl_element : 1"  # scripted group (container) (typed FeaturePython)
  n = 1
  ref = Tl_element
FEATURE [App::DocumentObjectGroupPython] Cl_element026  label="Cl_element : 013"  # scripted group (container) (typed FeaturePython)
  n = 1
  ref = Cl_element
FEATURE [App::DocumentObjectGroupPython] G4_THALLIUM_CHLORIDE  # scripted group (container) (typed FeaturePython)
  Dunit = g/cm3
  Dvalue = 7.004
  Group = -> [Tl_element001,Cl_element026]
  conduct = 2
  density = 1
  expand = 3
  formula = G4_THALLIUM_CHLORIDE
  name = G4_THALLIUM_CHLORIDE
  specific = 4
FEATURE [App::DocumentObjectGroupPython] H_element100  label="H_element : 0.147"  # scripted group (container) (typed FeaturePython)
  n = 0.105
FEATURE [App::DocumentObjectGroupPython] C_element110  label="C_element : 0.256"  # scripted group (container) (typed FeaturePython)
  n = 0.256
FEATURE [App::DocumentObjectGroupPython] N_element042  label="N_element : 0.760"  # scripted group (container) (typed FeaturePython)
  n = 0.027
FEATURE [App::DocumentObjectGroupPython] O_element094  label="O_element : 0.602"  # scripted group (container) (typed FeaturePython)
  n = 0.602
FEATURE [App::DocumentObjectGroupPython] Na_element019  label="Na_element : 0.102"  # scripted group (container) (typed FeaturePython)
  n = 0.001
FEATURE [App::DocumentObjectGroupPython] P_element011  label="P_element : 0.109"  # scripted group (container) (typed FeaturePython)
  n = 0.002
FEATURE [App::DocumentObjectGroupPython] S_element022  label="S_element : 0.023"  # scripted group (container) (typed FeaturePython)
  n = 0.003
FEATURE [App::DocumentObjectGroupPython] Cl_element027  label="Cl_element : 0.591"  # scripted group (container) (typed FeaturePython)
  n = 0.002
FEATURE [App::DocumentObjectGroupPython] K_element012  label="K_element : 0.018"  # scripted group (container) (typed FeaturePython)
  n = 0.002
FEATURE [App::DocumentObjectGroupPython] G4_TISSUE_SOFT_ICRP  # scripted group (container) (typed FeaturePython)
  Dunit = g/cm3
  Dvalue = 1.03
  Group = -> [H_element100,C_element110,N_element042,O_element094,Na_element019,P_element011,S_element022,Cl_element027,K_element012]
  conduct = 2
  density = 1
  expand = 3
  formula = G4_TISSUE_SOFT_ICRP
  name = G4_TISSUE_SOFT_ICRP
  specific = 4
FEATURE [App::DocumentObjectGroupPython] H_element101  label="H_element : 0.148"  # scripted group (container) (typed FeaturePython)
  n = 0.101
FEATURE [App::DocumentObjectGroupPython] C_element111  label="C_element : 0.111"  # scripted group (container) (typed FeaturePython)
  n = 0.111
FEATURE [App::DocumentObjectGroupPython] N_element043  label="N_element : 0.026"  # scripted group (container) (typed FeaturePython)
  n = 0.026
FEATURE [App::DocumentObjectGroupPython] O_element095  label="O_element : 0.762"  # scripted group (container) (typed FeaturePython)
  n = 0.762
FEATURE [App::DocumentObjectGroupPython] G4_TISSUE_SOFT_ICRU_4  label="G4_TISSUE_SOFT_ICRU-4"  # scripted group (container) (typed FeaturePython)
  Dunit = g/cm3
  Dvalue = 1
  Group = -> [H_element101,C_element111,N_element043,O_element095]
  conduct = 2
  density = 1
  expand = 3
  formula = G4_TISSUE_SOFT_ICRU-4
  name = G4_TISSUE_SOFT_ICRU-4
  specific = 4
FEATURE [App::DocumentObjectGroupPython] H_element102  label="H_element : 0.149"  # scripted group (container) (typed FeaturePython)
  n = 0.101869
FEATURE [App::DocumentObjectGroupPython] C_element112  label="C_element : 0.456"  # scripted group (container) (typed FeaturePython)
  n = 0.456179
FEATURE [App::DocumentObjectGroupPython] N_element044  label="N_element : 0.761"  # scripted group (container) (typed FeaturePython)
  n = 0.035172
FEATURE [App::DocumentObjectGroupPython] O_element096  label="O_element : 0.407"  # scripted group (container) (typed FeaturePython)
  n = 0.40678
FEATURE [App::DocumentObjectGroupPython] G4_TISSUE_METHANE  label="G4_TISSUE-METHANE"  # scripted group (container) (typed FeaturePython)
  Dunit = g/cm3
  Dvalue = 0.00106409
  Group = -> [H_element102,C_element112,N_element044,O_element096]
  conduct = 2
  density = 1
  expand = 3
  formula = G4_TISSUE-METHANE
  name = G4_TISSUE-METHANE
  specific = 4
FEATURE [App::DocumentObjectGroupPython] H_element103  label="H_element : 0.103"  # scripted group (container) (typed FeaturePython)
  n = 0.102672
FEATURE [App::DocumentObjectGroupPython] C_element113  label="C_element : 0.569"  # scripted group (container) (typed FeaturePython)
  n = 0.56894
FEATURE [App::DocumentObjectGroupPython] N_element045  label="N_element : 0.762"  # scripted group (container) (typed FeaturePython)
  n = 0.035022
FEATURE [App::DocumentObjectGroupPython] O_element097  label="O_element : 0.293"  # scripted group (container) (typed FeaturePython)
  n = 0.293366
FEATURE [App::DocumentObjectGroupPython] G4_TISSUE_PROPANE  label="G4_TISSUE-PROPANE"  # scripted group (container) (typed FeaturePython)
  Dunit = g/cm3
  Dvalue = 0.00182628
  Group = -> [H_element103,C_element113,N_element045,O_element097]
  conduct = 2
  density = 1
  expand = 3
  formula = G4_TISSUE-PROPANE
  name = G4_TISSUE-PROPANE
  specific = 4
FEATURE [App::DocumentObjectGroupPython] Ti_element003  label="Ti_element : 1"  # scripted group (container) (typed FeaturePython)
  n = 1
  ref = Ti_element
FEATURE [App::DocumentObjectGroupPython] O_element098  label="O_element : 052"  # scripted group (container) (typed FeaturePython)
  n = 2
  ref = O_element
FEATURE [App::DocumentObjectGroupPython] G4_TITANIUM_DIOXIDE  # scripted group (container) (typed FeaturePython)
  Dunit = g/cm3
  Dvalue = 4.26
  Group = -> [Ti_element003,O_element098]
  conduct = 2
  density = 1
  expand = 3
  formula = G4_TITANIUM_DIOXIDE
  name = G4_TITANIUM_DIOXIDE
  specific = 4
FEATURE [App::DocumentObjectGroupPython] C_element114  label="C_element : 061"  # scripted group (container) (typed FeaturePython)
  n = 7
  ref = C_element
FEATURE [App::DocumentObjectGroupPython] H_element104  label="H_element : 055"  # scripted group (container) (typed FeaturePython)
  n = 8
  ref = H_element
FEATURE [App::DocumentObjectGroupPython] G4_TOLUENE  # scripted group (container) (typed FeaturePython)
  Dunit = g/cm3
  Dvalue = 0.8669
  Group = -> [C_element114,H_element104]
  conduct = 2
  density = 1
  expand = 3
  formula = G4_TOLUENE
  name = G4_TOLUENE
  specific = 4
FEATURE [App::DocumentObjectGroupPython] C_element115  label="C_element : 062"  # scripted group (container) (typed FeaturePython)
  n = 2
  ref = C_element
FEATURE [App::DocumentObjectGroupPython] H_element105  label="H_element : 056"  # scripted group (container) (typed FeaturePython)
  n = 1
  ref = H_element
FEATURE [App::DocumentObjectGroupPython] Cl_element028  label="Cl_element : 014"  # scripted group (container) (typed FeaturePython)
  n = 3
  ref = Cl_element
FEATURE [App::DocumentObjectGroupPython] G4_TRICHLOROETHYLENE  # scripted group (container) (typed FeaturePython)
  Dunit = g/cm3
  Dvalue = 1.46
  Group = -> [C_element115,H_element105,Cl_element028]
  conduct = 2
  density = 1
  expand = 3
  formula = G4_TRICHLOROETHYLENE
  name = G4_TRICHLOROETHYLENE
  specific = 4
FEATURE [App::DocumentObjectGroupPython] C_element116  label="C_element : 063"  # scripted group (container) (typed FeaturePython)
  n = 6
  ref = C_element
FEATURE [App::DocumentObjectGroupPython] H_element106  label="H_element : 15"  # scripted group (container) (typed FeaturePython)
  n = 15
  ref = H_element
FEATURE [App::DocumentObjectGroupPython] O_element099  label="O_element : 053"  # scripted group (container) (typed FeaturePython)
  n = 4
  ref = O_element
FEATURE [App::DocumentObjectGroupPython] P_element012  label="P_element : 1"  # scripted group (container) (typed FeaturePython)
  n = 1
  ref = P_element
FEATURE [App::DocumentObjectGroupPython] G4_TRIETHYL_PHOSPHATE  # scripted group (container) (typed FeaturePython)
  Dunit = g/cm3
  Dvalue = 1.07
  Group = -> [C_element116,H_element106,O_element099,P_element012]
  conduct = 2
  density = 1
  expand = 3
  formula = G4_TRIETHYL_PHOSPHATE
  name = G4_TRIETHYL_PHOSPHATE
  specific = 4
FEATURE [App::DocumentObjectGroupPython] W_element003  label="W_element : 003"  # scripted group (container) (typed FeaturePython)
  n = 1
  ref = W_element
FEATURE [App::DocumentObjectGroupPython] F_element017  label="F_element : 6"  # scripted group (container) (typed FeaturePython)
  n = 6
  ref = F_element
FEATURE [App::DocumentObjectGroupPython] G4_TUNGSTEN_HEXAFLUORIDE  # scripted group (container) (typed FeaturePython)
  Dunit = g/cm3
  Dvalue = 2.4
  Group = -> [W_element003,F_element017]
  conduct = 2
  density = 1
  expand = 3
  formula = G4_TUNGSTEN_HEXAFLUORIDE
  name = G4_TUNGSTEN_HEXAFLUORIDE
  specific = 4
FEATURE [App::DocumentObjectGroupPython] U_element001  label="U_element : 1"  # scripted group (container) (typed FeaturePython)
  n = 1
  ref = U_element
FEATURE [App::DocumentObjectGroupPython] C_element117  label="C_element : 064"  # scripted group (container) (typed FeaturePython)
  n = 2
  ref = C_element
FEATURE [App::DocumentObjectGroupPython] G4_URANIUM_DICARBIDE  # scripted group (container) (typed FeaturePython)
  Dunit = g/cm3
  Dvalue = 11.28
  Group = -> [U_element001,C_element117]
  conduct = 2
  density = 1
  expand = 3
  formula = G4_URANIUM_DICARBIDE
  name = G4_URANIUM_DICARBIDE
  specific = 4
FEATURE [App::DocumentObjectGroupPython] U_element002  label="U_element : 002"  # scripted group (container) (typed FeaturePython)
  n = 1
  ref = U_element
FEATURE [App::DocumentObjectGroupPython] C_element118  label="C_element : 065"  # scripted group (container) (typed FeaturePython)
  n = 1
  ref = C_element
FEATURE [App::DocumentObjectGroupPython] G4_URANIUM_MONOCARBIDE  # scripted group (container) (typed FeaturePython)
  Dunit = g/cm3
  Dvalue = 13.63
  Group = -> [U_element002,C_element118]
  conduct = 2
  density = 1
  expand = 3
  formula = G4_URANIUM_MONOCARBIDE
  name = G4_URANIUM_MONOCARBIDE
  specific = 4
FEATURE [App::DocumentObjectGroupPython] U_element003  label="U_element : 003"  # scripted group (container) (typed FeaturePython)
  n = 1
  ref = U_element
FEATURE [App::DocumentObjectGroupPython] O_element100  label="O_element : 054"  # scripted group (container) (typed FeaturePython)
  n = 2
  ref = O_element
FEATURE [App::DocumentObjectGroupPython] G4_URANIUM_OXIDE  # scripted group (container) (typed FeaturePython)
  Dunit = g/cm3
  Dvalue = 10.96
  Group = -> [U_element003,O_element100]
  conduct = 2
  density = 1
  expand = 3
  formula = G4_URANIUM_OXIDE
  name = G4_URANIUM_OXIDE
  specific = 4
FEATURE [App::DocumentObjectGroupPython] C_element119  label="C_element : 066"  # scripted group (container) (typed FeaturePython)
  n = 1
  ref = C_element
FEATURE [App::DocumentObjectGroupPython] H_element107  label="H_element : 057"  # scripted group (container) (typed FeaturePython)
  n = 4
  ref = H_element
FEATURE [App::DocumentObjectGroupPython] N_element046  label="N_element : 019"  # scripted group (container) (typed FeaturePython)
  n = 2
  ref = N_element
FEATURE [App::DocumentObjectGroupPython] O_element101  label="O_element : 055"  # scripted group (container) (typed FeaturePython)
  n = 1
  ref = O_element
FEATURE [App::DocumentObjectGroupPython] G4_UREA  # scripted group (container) (typed FeaturePython)
  Dunit = g/cm3
  Dvalue = 1.323
  Group = -> [C_element119,H_element107,N_element046,O_element101]
  conduct = 2
  density = 1
  expand = 3
  formula = G4_UREA
  name = G4_UREA
  specific = 4
FEATURE [App::DocumentObjectGroupPython] C_element120  label="C_element : 067"  # scripted group (container) (typed FeaturePython)
  n = 5
  ref = C_element
FEATURE [App::DocumentObjectGroupPython] H_element108  label="H_element : 058"  # scripted group (container) (typed FeaturePython)
  n = 11
  ref = H_element
FEATURE [App::DocumentObjectGroupPython] N_element047  label="N_element : 020"  # scripted group (container) (typed FeaturePython)
  n = 1
  ref = N_element
FEATURE [App::DocumentObjectGroupPython] O_element102  label="O_element : 056"  # scripted group (container) (typed FeaturePython)
  n = 2
  ref = O_element
FEATURE [App::DocumentObjectGroupPython] G4_VALINE  # scripted group (container) (typed FeaturePython)
  Dunit = g/cm3
  Dvalue = 1.23
  Group = -> [C_element120,H_element108,N_element047,O_element102]
  conduct = 2
  density = 1
  expand = 3
  formula = G4_VALINE
  name = G4_VALINE
  specific = 4
FEATURE [App::DocumentObjectGroupPython] H_element109  label="H_element : 0.009"  # scripted group (container) (typed FeaturePython)
  n = 0.009417
FEATURE [App::DocumentObjectGroupPython] C_element121  label="C_element : 0.281"  # scripted group (container) (typed FeaturePython)
  n = 0.280555
FEATURE [App::DocumentObjectGroupPython] F_element018  label="F_element : 0.710"  # scripted group (container) (typed FeaturePython)
  n = 0.710028
FEATURE [App::DocumentObjectGroupPython] G4_VITON  # scripted group (container) (typed FeaturePython)
  Dunit = g/cm3
  Dvalue = 1.8
  Group = -> [H_element109,C_element121,F_element018]
  conduct = 2
  density = 1
  expand = 3
  formula = G4_VITON
  name = G4_VITON
  specific = 4
FEATURE [App::DocumentObjectGroupPython] H_element110  label="H_element : 059"  # scripted group (container) (typed FeaturePython)
  n = 2
  ref = H_element
FEATURE [App::DocumentObjectGroupPython] O_element103  label="O_element : 057"  # scripted group (container) (typed FeaturePython)
  n = 1
  ref = O_element
FEATURE [App::DocumentObjectGroupPython] G4_WATER  # scripted group (container) (typed FeaturePython)
  Dunit = g/cm3
  Dvalue = 1
  Group = -> [H_element110,O_element103]
  conduct = 2
  density = 1
  expand = 3
  formula = G4_WATER
  name = G4_WATER
  specific = 4
FEATURE [App::DocumentObjectGroupPython] H_element111  label="H_element : 060"  # scripted group (container) (typed FeaturePython)
  n = 2
  ref = H_element
FEATURE [App::DocumentObjectGroupPython] O_element104  label="O_element : 058"  # scripted group (container) (typed FeaturePython)
  n = 1
  ref = O_element
FEATURE [App::DocumentObjectGroupPython] G4_WATER_VAPOR  # scripted group (container) (typed FeaturePython)
  Dunit = g/cm3
  Dvalue = 0.000756182
  Group = -> [H_element111,O_element104]
  conduct = 2
  density = 1
  expand = 3
  formula = G4_WATER_VAPOR
  name = G4_WATER_VAPOR
  specific = 4
FEATURE [App::DocumentObjectGroupPython] C_element122  label="C_element : 068"  # scripted group (container) (typed FeaturePython)
  n = 8
  ref = C_element
FEATURE [App::DocumentObjectGroupPython] H_element112  label="H_element : 061"  # scripted group (container) (typed FeaturePython)
  n = 10
  ref = H_element
FEATURE [App::DocumentObjectGroupPython] G4_XYLENE  # scripted group (container) (typed FeaturePython)
  Dunit = g/cm3
  Dvalue = 0.87
  Group = -> [C_element122,H_element112]
  conduct = 2
  density = 1
  expand = 3
  formula = G4_XYLENE
  name = G4_XYLENE
  specific = 4
FEATURE [App::DocumentObjectGroupPython] C_element123  label="C_element : 069"  # scripted group (container) (typed FeaturePython)
  n = 1
  ref = C_element
FEATURE [App::DocumentObjectGroupPython] G4_GRAPHITE  # scripted group (container) (typed FeaturePython)
  Dunit = g/cm3
  Dvalue = 2.21
  Group = -> [C_element123]
  conduct = 2
  density = 1
  expand = 3
  formula = G4_GRAPHITE
  name = G4_GRAPHITE
  specific = 4
FEATURE [App::DocumentObjectGroupPython] NIST  # scripted group (container) (typed FeaturePython)
  Group = -> [G4_A_150_TISSUE,G4_ACETONE,G4_ACETYLENE,G4_ADENINE,G4_ADIPOSE_TISSUE_ICRP,G4_AIR,G4_ALANINE,G4_ALUMINUM_OXIDE,G4_AMBER,G4_AMMONIA,G4_ANILINE,G4_ANTHRACENE,G4_B_100_BONE,G4_BAKELITE,G4_BARIUM_FLUORIDE,G4_BARIUM_SULFATE,G4_BENZENE,G4_BERYLLIUM_OXIDE,G4_BGO,G4_BLOOD_ICRP,G4_BONE_COMPACT_ICRU,G4_BONE_CORTICAL_ICRP,G4_BORON_CARBIDE,G4_BORON_OXIDE,G4_BRAIN_ICRP,G4_BUTANE,G4_N_BUTYL_ALCOHOL,G4_C_552,+152 more]
FEATURE [App::DocumentObjectGroupPython] H_element113  label="H_element : 062"  # scripted group (container) (typed FeaturePython)
  n = 1
  ref = H_element
FEATURE [App::DocumentObjectGroupPython] G4_H  # scripted group (container) (typed FeaturePython)
  Dunit = g/cm3
  Dvalue = 8.3748e-05
  Group = -> [H_element113]
  conduct = 2
  density = 1
  expand = 3
  formula = H
  name = G4_H
  specific = 4
FEATURE [App::DocumentObjectGroupPython] He_element001  label="He_element : 1"  # scripted group (container) (typed FeaturePython)
  n = 1
  ref = He_element
FEATURE [App::DocumentObjectGroupPython] G4_He  # scripted group (container) (typed FeaturePython)
  Dunit = g/cm3
  Dvalue = 0.000166322
  Group = -> [He_element001]
  conduct = 2
  density = 1
  expand = 3
  formula = He
  name = G4_He
  specific = 4
FEATURE [App::DocumentObjectGroupPython] Li_element008  label="Li_element : 008"  # scripted group (container) (typed FeaturePython)
  n = 1
  ref = Li_element
FEATURE [App::DocumentObjectGroupPython] G4_Li  # scripted group (container) (typed FeaturePython)
  Dunit = g/cm3
  Dvalue = 0.534
  Group = -> [Li_element008]
  conduct = 2
  density = 1
  expand = 3
  formula = Li
  name = G4_Li
  specific = 4
FEATURE [App::DocumentObjectGroupPython] Be_element002  label="Be_element : 002"  # scripted group (container) (typed FeaturePython)
  n = 1
  ref = Be_element
FEATURE [App::DocumentObjectGroupPython] G4_Be  # scripted group (container) (typed FeaturePython)
  Dunit = g/cm3
  Dvalue = 1.848
  Group = -> [Be_element002]
  conduct = 2
  density = 1
  expand = 3
  formula = Be
  name = G4_Be
  specific = 4
FEATURE [App::DocumentObjectGroupPython] B_element007  label="B_element : 007"  # scripted group (container) (typed FeaturePython)
  n = 1
  ref = B_element
FEATURE [App::DocumentObjectGroupPython] G4_B  # scripted group (container) (typed FeaturePython)
  Dunit = g/cm3
  Dvalue = 2.37
  Group = -> [B_element007]
  conduct = 2
  density = 1
  expand = 3
  formula = B
  name = G4_B
  specific = 4
FEATURE [App::DocumentObjectGroupPython] C_element124  label="C_element : 070"  # scripted group (container) (typed FeaturePython)
  n = 1
  ref = C_element
FEATURE [App::DocumentObjectGroupPython] G4_C  # scripted group (container) (typed FeaturePython)
  Dunit = g/cm3
  Dvalue = 2
  Group = -> [C_element124]
  conduct = 2
  density = 1
  expand = 3
  formula = C
  name = G4_C
  specific = 4
FEATURE [App::DocumentObjectGroupPython] N_element048  label="N_element : 021"  # scripted group (container) (typed FeaturePython)
  n = 1
  ref = N_element
FEATURE [App::DocumentObjectGroupPython] G4_N  # scripted group (container) (typed FeaturePython)
  Dunit = g/cm3
  Dvalue = 0.0011652
  Group = -> [N_element048]
  conduct = 2
  density = 1
  expand = 3
  formula = N
  name = G4_N
  specific = 4
FEATURE [App::DocumentObjectGroupPython] O_element105  label="O_element : 059"  # scripted group (container) (typed FeaturePython)
  n = 1
  ref = O_element
FEATURE [App::DocumentObjectGroupPython] G4_O  # scripted group (container) (typed FeaturePython)
  Dunit = g/cm3
  Dvalue = 0.00133151
  Group = -> [O_element105]
  conduct = 2
  density = 1
  expand = 3
  formula = O
  name = G4_O
  specific = 4
FEATURE [App::DocumentObjectGroupPython] F_element019  label="F_element : 008"  # scripted group (container) (typed FeaturePython)
  n = 1
  ref = F_element
FEATURE [App::DocumentObjectGroupPython] G4_F  # scripted group (container) (typed FeaturePython)
  Dunit = g/cm3
  Dvalue = 0.00158029
  Group = -> [F_element019]
  conduct = 2
  density = 1
  expand = 3
  formula = F
  name = G4_F
  specific = 4
FEATURE [App::DocumentObjectGroupPython] Ne_element001  label="Ne_element : 1"  # scripted group (container) (typed FeaturePython)
  n = 1
  ref = Ne_element
FEATURE [App::DocumentObjectGroupPython] G4_Ne  # scripted group (container) (typed FeaturePython)
  Dunit = g/cm3
  Dvalue = 0.000838505
  Group = -> [Ne_element001]
  conduct = 2
  density = 1
  expand = 3
  formula = Ne
  name = G4_Ne
  specific = 4
FEATURE [App::DocumentObjectGroupPython] Na_element020  label="Na_element : 005"  # scripted group (container) (typed FeaturePython)
  n = 1
  ref = Na_element
FEATURE [App::DocumentObjectGroupPython] G4_Na  # scripted group (container) (typed FeaturePython)
  Dunit = g/cm3
  Dvalue = 0.971
  Group = -> [Na_element020]
  conduct = 2
  density = 1
  expand = 3
  formula = Na
  name = G4_Na
  specific = 4
FEATURE [App::DocumentObjectGroupPython] Mg_element011  label="Mg_element : 005"  # scripted group (container) (typed FeaturePython)
  n = 1
  ref = Mg_element
FEATURE [App::DocumentObjectGroupPython] G4_Mg  # scripted group (container) (typed FeaturePython)
  Dunit = g/cm3
  Dvalue = 1.74
  Group = -> [Mg_element011]
  conduct = 2
  density = 1
  expand = 3
  formula = Mg
  name = G4_Mg
  specific = 4
FEATURE [App::DocumentObjectGroupPython] Al_element004  label="Al_element : 1"  # scripted group (container) (typed FeaturePython)
  n = 1
  ref = Al_element
FEATURE [App::DocumentObjectGroupPython] G4_Al  # scripted group (container) (typed FeaturePython)
  Dunit = g/cm3
  Dvalue = 2.699
  Group = -> [Al_element004]
  conduct = 2
  density = 1
  expand = 3
  formula = Al
  name = G4_Al
  specific = 4
FEATURE [App::DocumentObjectGroupPython] Si_element007  label="Si_element : 002"  # scripted group (container) (typed FeaturePython)
  n = 1
  ref = Si_element
FEATURE [App::DocumentObjectGroupPython] G4_Si  # scripted group (container) (typed FeaturePython)
  Dunit = g/cm3
  Dvalue = 2.33
  Group = -> [Si_element007]
  conduct = 2
  density = 1
  expand = 3
  formula = Si
  name = G4_Si
  specific = 4
FEATURE [App::DocumentObjectGroupPython] P_element013  label="P_element : 002"  # scripted group (container) (typed FeaturePython)
  n = 1
  ref = P_element
FEATURE [App::DocumentObjectGroupPython] G4_P  # scripted group (container) (typed FeaturePython)
  Dunit = g/cm3
  Dvalue = 2.2
  Group = -> [P_element013]
  conduct = 2
  density = 1
  expand = 3
  formula = P
  name = G4_P
  specific = 4
FEATURE [App::DocumentObjectGroupPython] S_element023  label="S_element : 007"  # scripted group (container) (typed FeaturePython)
  n = 1
  ref = S_element
FEATURE [App::DocumentObjectGroupPython] G4_S  # scripted group (container) (typed FeaturePython)
  Dunit = g/cm3
  Dvalue = 2
  Group = -> [S_element023]
  conduct = 2
  density = 1
  expand = 3
  formula = S
  name = G4_S
  specific = 4
FEATURE [App::DocumentObjectGroupPython] Cl_element029  label="Cl_element : 015"  # scripted group (container) (typed FeaturePython)
  n = 1
  ref = Cl_element
FEATURE [App::DocumentObjectGroupPython] G4_Cl  # scripted group (container) (typed FeaturePython)
  Dunit = g/cm3
  Dvalue = 0.00299473
  Group = -> [Cl_element029]
  conduct = 2
  density = 1
  expand = 3
  formula = Cl
  name = G4_Cl
  specific = 4
FEATURE [App::DocumentObjectGroupPython] Ar_element002  label="Ar_element : 1"  # scripted group (container) (typed FeaturePython)
  n = 1
  ref = Ar_element
FEATURE [App::DocumentObjectGroupPython] G4_Ar  # scripted group (container) (typed FeaturePython)
  Dunit = g/cm3
  Dvalue = 0.00166201
  Group = -> [Ar_element002]
  conduct = 2
  density = 1
  expand = 3
  formula = Ar
  name = G4_Ar
  specific = 4
FEATURE [App::DocumentObjectGroupPython] K_element013  label="K_element : 003"  # scripted group (container) (typed FeaturePython)
  n = 1
  ref = K_element
FEATURE [App::DocumentObjectGroupPython] G4_K  # scripted group (container) (typed FeaturePython)
  Dunit = g/cm3
  Dvalue = 0.862
  Group = -> [K_element013]
  conduct = 2
  density = 1
  expand = 3
  formula = K
  name = G4_K
  specific = 4
FEATURE [App::DocumentObjectGroupPython] Ca_element014  label="Ca_element : 007"  # scripted group (container) (typed FeaturePython)
  n = 1
  ref = Ca_element
FEATURE [App::DocumentObjectGroupPython] G4_Ca  # scripted group (container) (typed FeaturePython)
  Dunit = g/cm3
  Dvalue = 1.55
  Group = -> [Ca_element014]
  conduct = 2
  density = 1
  expand = 3
  formula = Ca
  name = G4_Ca
  specific = 4
FEATURE [App::DocumentObjectGroupPython] Sc_element001  label="Sc_element : 1"  # scripted group (container) (typed FeaturePython)
  n = 1
  ref = Sc_element
FEATURE [App::DocumentObjectGroupPython] G4_Sc  # scripted group (container) (typed FeaturePython)
  Dunit = g/cm3
  Dvalue = 2.989
  Group = -> [Sc_element001]
  conduct = 2
  density = 1
  expand = 3
  formula = Sc
  name = G4_Sc
  specific = 4
FEATURE [App::DocumentObjectGroupPython] Ti_element004  label="Ti_element : 002"  # scripted group (container) (typed FeaturePython)
  n = 1
  ref = Ti_element
FEATURE [App::DocumentObjectGroupPython] G4_Ti  # scripted group (container) (typed FeaturePython)
  Dunit = g/cm3
  Dvalue = 4.54
  Group = -> [Ti_element004]
  conduct = 2
  density = 1
  expand = 3
  formula = Ti
  name = G4_Ti
  specific = 4
FEATURE [App::DocumentObjectGroupPython] V_element001  label="V_element : 1"  # scripted group (container) (typed FeaturePython)
  n = 1
  ref = V_element
FEATURE [App::DocumentObjectGroupPython] G4_V  # scripted group (container) (typed FeaturePython)
  Dunit = g/cm3
  Dvalue = 6.11
  Group = -> [V_element001]
  conduct = 2
  density = 1
  expand = 3
  formula = V
  name = G4_V
  specific = 4
FEATURE [App::DocumentObjectGroupPython] Cr_element001  label="Cr_element : 1"  # scripted group (container) (typed FeaturePython)
  n = 1
  ref = Cr_element
FEATURE [App::DocumentObjectGroupPython] G4_Cr  # scripted group (container) (typed FeaturePython)
  Dunit = g/cm3
  Dvalue = 7.18
  Group = -> [Cr_element001]
  conduct = 2
  density = 1
  expand = 3
  formula = Cr
  name = G4_Cr
  specific = 4
FEATURE [App::DocumentObjectGroupPython] Mn_element001  label="Mn_element : 1"  # scripted group (container) (typed FeaturePython)
  n = 1
  ref = Mn_element
FEATURE [App::DocumentObjectGroupPython] G4_Mn  # scripted group (container) (typed FeaturePython)
  Dunit = g/cm3
  Dvalue = 7.44
  Group = -> [Mn_element001]
  conduct = 2
  density = 1
  expand = 3
  formula = Mn
  name = G4_Mn
  specific = 4
FEATURE [App::DocumentObjectGroupPython] Fe_element007  label="Fe_element : 004"  # scripted group (container) (typed FeaturePython)
  n = 1
  ref = Fe_element
FEATURE [App::DocumentObjectGroupPython] G4_Fe  # scripted group (container) (typed FeaturePython)
  Dunit = g/cm3
  Dvalue = 7.874
  Group = -> [Fe_element007]
  conduct = 2
  density = 1
  expand = 3
  formula = Fe
  name = G4_Fe
  specific = 4
FEATURE [App::DocumentObjectGroupPython] Co_element001  label="Co_element : 1"  # scripted group (container) (typed FeaturePython)
  n = 1
  ref = Co_element
FEATURE [App::DocumentObjectGroupPython] G4_Co  # scripted group (container) (typed FeaturePython)
  Dunit = g/cm3
  Dvalue = 8.9
  Group = -> [Co_element001]
  conduct = 2
  density = 1
  expand = 3
  formula = Co
  name = G4_Co
  specific = 4
FEATURE [App::DocumentObjectGroupPython] Ni_element001  label="Ni_element : 1"  # scripted group (container) (typed FeaturePython)
  n = 1
  ref = Ni_element
FEATURE [App::DocumentObjectGroupPython] G4_Ni  # scripted group (container) (typed FeaturePython)
  Dunit = g/cm3
  Dvalue = 8.902
  Group = -> [Ni_element001]
  conduct = 2
  density = 1
  expand = 3
  formula = Ni
  name = G4_Ni
  specific = 4
FEATURE [App::DocumentObjectGroupPython] Cu_element001  label="Cu_element : 1"  # scripted group (container) (typed FeaturePython)
  n = 1
  ref = Cu_element
FEATURE [App::DocumentObjectGroupPython] G4_Cu  # scripted group (container) (typed FeaturePython)
  Dunit = g/cm3
  Dvalue = 8.96
  Group = -> [Cu_element001]
  conduct = 2
  density = 1
  expand = 3
  formula = Cu
  name = G4_Cu
  specific = 4
FEATURE [App::DocumentObjectGroupPython] Zn_element001  label="Zn_element : 1"  # scripted group (container) (typed FeaturePython)
  n = 1
  ref = Zn_element
FEATURE [App::DocumentObjectGroupPython] G4_Zn  # scripted group (container) (typed FeaturePython)
  Dunit = g/cm3
  Dvalue = 7.133
  Group = -> [Zn_element001]
  conduct = 2
  density = 1
  expand = 3
  formula = Zn
  name = G4_Zn
  specific = 4
FEATURE [App::DocumentObjectGroupPython] Ga_element002  label="Ga_element : 002"  # scripted group (container) (typed FeaturePython)
  n = 1
  ref = Ga_element
FEATURE [App::DocumentObjectGroupPython] G4_Ga  # scripted group (container) (typed FeaturePython)
  Dunit = g/cm3
  Dvalue = 5.904
  Group = -> [Ga_element002]
  conduct = 2
  density = 1
  expand = 3
  formula = Ga
  name = G4_Ga
  specific = 4
FEATURE [App::DocumentObjectGroupPython] Ge_element002  label="Ge_element : 1"  # scripted group (container) (typed FeaturePython)
  n = 1
  ref = Ge_element
FEATURE [App::DocumentObjectGroupPython] G4_Ge  # scripted group (container) (typed FeaturePython)
  Dunit = g/cm3
  Dvalue = 5.323
  Group = -> [Ge_element002]
  conduct = 2
  density = 1
  expand = 3
  formula = Ge
  name = G4_Ge
  specific = 4
FEATURE [App::DocumentObjectGroupPython] As_element003  label="As_element : 002"  # scripted group (container) (typed FeaturePython)
  n = 1
  ref = As_element
FEATURE [App::DocumentObjectGroupPython] G4_As  # scripted group (container) (typed FeaturePython)
  Dunit = g/cm3
  Dvalue = 5.73
  Group = -> [As_element003]
  conduct = 2
  density = 1
  expand = 3
  formula = As
  name = G4_As
  specific = 4
FEATURE [App::DocumentObjectGroupPython] Se_element001  label="Se_element : 1"  # scripted group (container) (typed FeaturePython)
  n = 1
  ref = Se_element
FEATURE [App::DocumentObjectGroupPython] G4_Se  # scripted group (container) (typed FeaturePython)
  Dunit = g/cm3
  Dvalue = 4.5
  Group = -> [Se_element001]
  conduct = 2
  density = 1
  expand = 3
  formula = Se
  name = G4_Se
  specific = 4
FEATURE [App::DocumentObjectGroupPython] Br_element007  label="Br_element : 004"  # scripted group (container) (typed FeaturePython)
  n = 1
  ref = Br_element
FEATURE [App::DocumentObjectGroupPython] G4_Br  # scripted group (container) (typed FeaturePython)
  Dunit = g/cm3
  Dvalue = 0.0070721
  Group = -> [Br_element007]
  conduct = 2
  density = 1
  expand = 3
  formula = Br
  name = G4_Br
  specific = 4
FEATURE [App::DocumentObjectGroupPython] Kr_element001  label="Kr_element : 1"  # scripted group (container) (typed FeaturePython)
  n = 1
  ref = Kr_element
FEATURE [App::DocumentObjectGroupPython] G4_Kr  # scripted group (container) (typed FeaturePython)
  Dunit = g/cm3
  Dvalue = 0.00347832
  Group = -> [Kr_element001]
  conduct = 2
  density = 1
  expand = 3
  formula = Kr
  name = G4_Kr
  specific = 4
FEATURE [App::DocumentObjectGroupPython] Rb_element001  label="Rb_element : 1"  # scripted group (container) (typed FeaturePython)
  n = 1
  ref = Rb_element
FEATURE [App::DocumentObjectGroupPython] G4_Rb  # scripted group (container) (typed FeaturePython)
  Dunit = g/cm3
  Dvalue = 1.532
  Group = -> [Rb_element001]
  conduct = 2
  density = 1
  expand = 3
  formula = Rb
  name = G4_Rb
  specific = 4
FEATURE [App::DocumentObjectGroupPython] Sr_element001  label="Sr_element : 1"  # scripted group (container) (typed FeaturePython)
  n = 1
  ref = Sr_element
FEATURE [App::DocumentObjectGroupPython] G4_Sr  # scripted group (container) (typed FeaturePython)
  Dunit = g/cm3
  Dvalue = 2.54
  Group = -> [Sr_element001]
  conduct = 2
  density = 1
  expand = 3
  formula = Sr
  name = G4_Sr
  specific = 4
FEATURE [App::DocumentObjectGroupPython] Y_element001  label="Y_element : 1"  # scripted group (container) (typed FeaturePython)
  n = 1
  ref = Y_element
FEATURE [App::DocumentObjectGroupPython] G4_Y  # scripted group (container) (typed FeaturePython)
  Dunit = g/cm3
  Dvalue = 4.469
  Group = -> [Y_element001]
  conduct = 2
  density = 1
  expand = 3
  formula = Y
  name = G4_Y
  specific = 4
FEATURE [App::DocumentObjectGroupPython] Zr_element001  label="Zr_element : 1"  # scripted group (container) (typed FeaturePython)
  n = 1
  ref = Zr_element
FEATURE [App::DocumentObjectGroupPython] G4_Zr  # scripted group (container) (typed FeaturePython)
  Dunit = g/cm3
  Dvalue = 6.506
  Group = -> [Zr_element001]
  conduct = 2
  density = 1
  expand = 3
  formula = Zr
  name = G4_Zr
  specific = 4
FEATURE [App::DocumentObjectGroupPython] Nb_element001  label="Nb_element : 1"  # scripted group (container) (typed FeaturePython)
  n = 1
  ref = Nb_element
FEATURE [App::DocumentObjectGroupPython] G4_Nb  # scripted group (container) (typed FeaturePython)
  Dunit = g/cm3
  Dvalue = 8.57
  Group = -> [Nb_element001]
  conduct = 2
  density = 1
  expand = 3
  formula = Nb
  name = G4_Nb
  specific = 4
FEATURE [App::DocumentObjectGroupPython] Mo_element001  label="Mo_element : 1"  # scripted group (container) (typed FeaturePython)
  n = 1
  ref = Mo_element
FEATURE [App::DocumentObjectGroupPython] G4_Mo  # scripted group (container) (typed FeaturePython)
  Dunit = g/cm3
  Dvalue = 10.22
  Group = -> [Mo_element001]
  conduct = 2
  density = 1
  expand = 3
  formula = Mo
  name = G4_Mo
  specific = 4
FEATURE [App::DocumentObjectGroupPython] Tc_element001  label="Tc_element : 1"  # scripted group (container) (typed FeaturePython)
  n = 1
  ref = Tc_element
FEATURE [App::DocumentObjectGroupPython] G4_Tc  # scripted group (container) (typed FeaturePython)
  Dunit = g/cm3
  Dvalue = 11.5
  Group = -> [Tc_element001]
  conduct = 2
  density = 1
  expand = 3
  formula = Tc
  name = G4_Tc
  specific = 4
FEATURE [App::DocumentObjectGroupPython] Ru_element001  label="Ru_element : 1"  # scripted group (container) (typed FeaturePython)
  n = 1
  ref = Ru_element
FEATURE [App::DocumentObjectGroupPython] G4_Ru  # scripted group (container) (typed FeaturePython)
  Dunit = g/cm3
  Dvalue = 12.41
  Group = -> [Ru_element001]
  conduct = 2
  density = 1
  expand = 3
  formula = Ru
  name = G4_Ru
  specific = 4
FEATURE [App::DocumentObjectGroupPython] Rh_element001  label="Rh_element : 1"  # scripted group (container) (typed FeaturePython)
  n = 1
  ref = Rh_element
FEATURE [App::DocumentObjectGroupPython] G4_Rh  # scripted group (container) (typed FeaturePython)
  Dunit = g/cm3
  Dvalue = 12.41
  Group = -> [Rh_element001]
  conduct = 2
  density = 1
  expand = 3
  formula = Rh
  name = G4_Rh
  specific = 4
FEATURE [App::DocumentObjectGroupPython] Pd_element001  label="Pd_element : 1"  # scripted group (container) (typed FeaturePython)
  n = 1
  ref = Pd_element
FEATURE [App::DocumentObjectGroupPython] G4_Pd  # scripted group (container) (typed FeaturePython)
  Dunit = g/cm3
  Dvalue = 12.02
  Group = -> [Pd_element001]
  conduct = 2
  density = 1
  expand = 3
  formula = Pd
  name = G4_Pd
  specific = 4
FEATURE [App::DocumentObjectGroupPython] Ag_element006  label="Ag_element : 004"  # scripted group (container) (typed FeaturePython)
  n = 1
  ref = Ag_element
FEATURE [App::DocumentObjectGroupPython] G4_Ag  # scripted group (container) (typed FeaturePython)
  Dunit = g/cm3
  Dvalue = 10.5
  Group = -> [Ag_element006]
  conduct = 2
  density = 1
  expand = 3
  formula = Ag
  name = G4_Ag
  specific = 4
FEATURE [App::DocumentObjectGroupPython] Cd_element003  label="Cd_element : 003"  # scripted group (container) (typed FeaturePython)
  n = 1
  ref = Cd_element
FEATURE [App::DocumentObjectGroupPython] G4_Cd  # scripted group (container) (typed FeaturePython)
  Dunit = g/cm3
  Dvalue = 8.65
  Group = -> [Cd_element003]
  conduct = 2
  density = 1
  expand = 3
  formula = Cd
  name = G4_Cd
  specific = 4
FEATURE [App::DocumentObjectGroupPython] In_element001  label="In_element : 1"  # scripted group (container) (typed FeaturePython)
  n = 1
  ref = In_element
FEATURE [App::DocumentObjectGroupPython] G4_In  # scripted group (container) (typed FeaturePython)
  Dunit = g/cm3
  Dvalue = 7.31
  Group = -> [In_element001]
  conduct = 2
  density = 1
  expand = 3
  formula = In
  name = G4_In
  specific = 4
FEATURE [App::DocumentObjectGroupPython] Sn_element001  label="Sn_element : 1"  # scripted group (container) (typed FeaturePython)
  n = 1
  ref = Sn_element
FEATURE [App::DocumentObjectGroupPython] G4_Sn  # scripted group (container) (typed FeaturePython)
  Dunit = g/cm3
  Dvalue = 7.31
  Group = -> [Sn_element001]
  conduct = 2
  density = 1
  expand = 3
  formula = Sn
  name = G4_Sn
  specific = 4
FEATURE [App::DocumentObjectGroupPython] Sb_element001  label="Sb_element : 1"  # scripted group (container) (typed FeaturePython)
  n = 1
  ref = Sb_element
FEATURE [App::DocumentObjectGroupPython] G4_Sb  # scripted group (container) (typed FeaturePython)
  Dunit = g/cm3
  Dvalue = 6.691
  Group = -> [Sb_element001]
  conduct = 2
  density = 1
  expand = 3
  formula = Sb
  name = G4_Sb
  specific = 4
FEATURE [App::DocumentObjectGroupPython] Te_element002  label="Te_element : 002"  # scripted group (container) (typed FeaturePython)
  n = 1
  ref = Te_element
FEATURE [App::DocumentObjectGroupPython] G4_Te  # scripted group (container) (typed FeaturePython)
  Dunit = g/cm3
  Dvalue = 6.24
  Group = -> [Te_element002]
  conduct = 2
  density = 1
  expand = 3
  formula = Te
  name = G4_Te
  specific = 4
FEATURE [App::DocumentObjectGroupPython] I_element010  label="I_element : 006"  # scripted group (container) (typed FeaturePython)
  n = 1
  ref = I_element
FEATURE [App::DocumentObjectGroupPython] G4_I  # scripted group (container) (typed FeaturePython)
  Dunit = g/cm3
  Dvalue = 4.93
  Group = -> [I_element010]
  conduct = 2
  density = 1
  expand = 3
  formula = I
  name = G4_I
  specific = 4
FEATURE [App::DocumentObjectGroupPython] Xe_element001  label="Xe_element : 1"  # scripted group (container) (typed FeaturePython)
  n = 1
  ref = Xe_element
FEATURE [App::DocumentObjectGroupPython] G4_Xe  # scripted group (container) (typed FeaturePython)
  Dunit = g/cm3
  Dvalue = 0.00548536
  Group = -> [Xe_element001]
  conduct = 2
  density = 1
  expand = 3
  formula = Xe
  name = G4_Xe
  specific = 4
FEATURE [App::DocumentObjectGroupPython] Cs_element003  label="Cs_element : 003"  # scripted group (container) (typed FeaturePython)
  n = 1
  ref = Cs_element
FEATURE [App::DocumentObjectGroupPython] G4_Cs  # scripted group (container) (typed FeaturePython)
  Dunit = g/cm3
  Dvalue = 1.873
  Group = -> [Cs_element003]
  conduct = 2
  density = 1
  expand = 3
  formula = Cs
  name = G4_Cs
  specific = 4
FEATURE [App::DocumentObjectGroupPython] Ba_element003  label="Ba_element : 003"  # scripted group (container) (typed FeaturePython)
  n = 1
  ref = Ba_element
FEATURE [App::DocumentObjectGroupPython] G4_Ba  # scripted group (container) (typed FeaturePython)
  Dunit = g/cm3
  Dvalue = 3.5
  Group = -> [Ba_element003]
  conduct = 2
  density = 1
  expand = 3
  formula = Ba
  name = G4_Ba
  specific = 4
FEATURE [App::DocumentObjectGroupPython] La_element003  label="La_element : 003"  # scripted group (container) (typed FeaturePython)
  n = 1
  ref = La_element
FEATURE [App::DocumentObjectGroupPython] G4_La  # scripted group (container) (typed FeaturePython)
  Dunit = g/cm3
  Dvalue = 6.154
  Group = -> [La_element003]
  conduct = 2
  density = 1
  expand = 3
  formula = La
  name = G4_La
  specific = 4
FEATURE [App::DocumentObjectGroupPython] Ce_element002  label="Ce_element : 1"  # scripted group (container) (typed FeaturePython)
  n = 1
  ref = Ce_element
FEATURE [App::DocumentObjectGroupPython] G4_Ce  # scripted group (container) (typed FeaturePython)
  Dunit = g/cm3
  Dvalue = 6.657
  Group = -> [Ce_element002]
  conduct = 2
  density = 1
  expand = 3
  formula = Ce
  name = G4_Ce
  specific = 4
FEATURE [App::DocumentObjectGroupPython] Pr_element001  label="Pr_element : 1"  # scripted group (container) (typed FeaturePython)
  n = 1
  ref = Pr_element
FEATURE [App::DocumentObjectGroupPython] G4_Pr  # scripted group (container) (typed FeaturePython)
  Dunit = g/cm3
  Dvalue = 6.71
  Group = -> [Pr_element001]
  conduct = 2
  density = 1
  expand = 3
  formula = Pr
  name = G4_Pr
  specific = 4
FEATURE [App::DocumentObjectGroupPython] Nd_element001  label="Nd_element : 1"  # scripted group (container) (typed FeaturePython)
  n = 1
  ref = Nd_element
FEATURE [App::DocumentObjectGroupPython] G4_Nd  # scripted group (container) (typed FeaturePython)
  Dunit = g/cm3
  Dvalue = 6.9
  Group = -> [Nd_element001]
  conduct = 2
  density = 1
  expand = 3
  formula = Nd
  name = G4_Nd
  specific = 4
FEATURE [App::DocumentObjectGroupPython] Pm_element001  label="Pm_element : 1"  # scripted group (container) (typed FeaturePython)
  n = 1
  ref = Pm_element
FEATURE [App::DocumentObjectGroupPython] G4_Pm  # scripted group (container) (typed FeaturePython)
  Dunit = g/cm3
  Dvalue = 7.22
  Group = -> [Pm_element001]
  conduct = 2
  density = 1
  expand = 3
  formula = Pm
  name = G4_Pm
  specific = 4
FEATURE [App::DocumentObjectGroupPython] Sm_element001  label="Sm_element : 1"  # scripted group (container) (typed FeaturePython)
  n = 1
  ref = Sm_element
FEATURE [App::DocumentObjectGroupPython] G4_Sm  # scripted group (container) (typed FeaturePython)
  Dunit = g/cm3
  Dvalue = 7.46
  Group = -> [Sm_element001]
  conduct = 2
  density = 1
  expand = 3
  formula = Sm
  name = G4_Sm
  specific = 4
FEATURE [App::DocumentObjectGroupPython] Eu_element001  label="Eu_element : 1"  # scripted group (container) (typed FeaturePython)
  n = 1
  ref = Eu_element
FEATURE [App::DocumentObjectGroupPython] G4_Eu  # scripted group (container) (typed FeaturePython)
  Dunit = g/cm3
  Dvalue = 5.243
  Group = -> [Eu_element001]
  conduct = 2
  density = 1
  expand = 3
  formula = Eu
  name = G4_Eu
  specific = 4
FEATURE [App::DocumentObjectGroupPython] Gd_element002  label="Gd_element : 1"  # scripted group (container) (typed FeaturePython)
  n = 1
  ref = Gd_element
FEATURE [App::DocumentObjectGroupPython] G4_Gd  # scripted group (container) (typed FeaturePython)
  Dunit = g/cm3
  Dvalue = 7.9004
  Group = -> [Gd_element002]
  conduct = 2
  density = 1
  expand = 3
  formula = Gd
  name = G4_Gd
  specific = 4
FEATURE [App::DocumentObjectGroupPython] Tb_element001  label="Tb_element : 1"  # scripted group (container) (typed FeaturePython)
  n = 1
  ref = Tb_element
FEATURE [App::DocumentObjectGroupPython] G4_Tb  # scripted group (container) (typed FeaturePython)
  Dunit = g/cm3
  Dvalue = 8.229
  Group = -> [Tb_element001]
  conduct = 2
  density = 1
  expand = 3
  formula = Tb
  name = G4_Tb
  specific = 4
FEATURE [App::DocumentObjectGroupPython] Dy_element001  label="Dy_element : 1"  # scripted group (container) (typed FeaturePython)
  n = 1
  ref = Dy_element
FEATURE [App::DocumentObjectGroupPython] G4_Dy  # scripted group (container) (typed FeaturePython)
  Dunit = g/cm3
  Dvalue = 8.55
  Group = -> [Dy_element001]
  conduct = 2
  density = 1
  expand = 3
  formula = Dy
  name = G4_Dy
  specific = 4
FEATURE [App::DocumentObjectGroupPython] Ho_element001  label="Ho_element : 1"  # scripted group (container) (typed FeaturePython)
  n = 1
  ref = Ho_element
FEATURE [App::DocumentObjectGroupPython] G4_Ho  # scripted group (container) (typed FeaturePython)
  Dunit = g/cm3
  Dvalue = 8.795
  Group = -> [Ho_element001]
  conduct = 2
  density = 1
  expand = 3
  formula = Ho
  name = G4_Ho
  specific = 4
FEATURE [App::DocumentObjectGroupPython] Er_element001  label="Er_element : 1"  # scripted group (container) (typed FeaturePython)
  n = 1
  ref = Er_element
FEATURE [App::DocumentObjectGroupPython] G4_Er  # scripted group (container) (typed FeaturePython)
  Dunit = g/cm3
  Dvalue = 9.066
  Group = -> [Er_element001]
  conduct = 2
  density = 1
  expand = 3
  formula = Er
  name = G4_Er
  specific = 4
FEATURE [App::DocumentObjectGroupPython] Tm_element001  label="Tm_element : 1"  # scripted group (container) (typed FeaturePython)
  n = 1
  ref = Tm_element
FEATURE [App::DocumentObjectGroupPython] G4_Tm  # scripted group (container) (typed FeaturePython)
  Dunit = g/cm3
  Dvalue = 9.321
  Group = -> [Tm_element001]
  conduct = 2
  density = 1
  expand = 3
  formula = Tm
  name = G4_Tm
  specific = 4
FEATURE [App::DocumentObjectGroupPython] Yb_element001  label="Yb_element : 1"  # scripted group (container) (typed FeaturePython)
  n = 1
  ref = Yb_element
FEATURE [App::DocumentObjectGroupPython] G4_Yb  # scripted group (container) (typed FeaturePython)
  Dunit = g/cm3
  Dvalue = 6.73
  Group = -> [Yb_element001]
  conduct = 2
  density = 1
  expand = 3
  formula = Yb
  name = G4_Yb
  specific = 4
FEATURE [App::DocumentObjectGroupPython] Lu_element001  label="Lu_element : 1"  # scripted group (container) (typed FeaturePython)
  n = 1
  ref = Lu_element
FEATURE [App::DocumentObjectGroupPython] G4_Lu  # scripted group (container) (typed FeaturePython)
  Dunit = g/cm3
  Dvalue = 9.84
  Group = -> [Lu_element001]
  conduct = 2
  density = 1
  expand = 3
  formula = Lu
  name = G4_Lu
  specific = 4
FEATURE [App::DocumentObjectGroupPython] Hf_element001  label="Hf_element : 1"  # scripted group (container) (typed FeaturePython)
  n = 1
  ref = Hf_element
FEATURE [App::DocumentObjectGroupPython] G4_Hf  # scripted group (container) (typed FeaturePython)
  Dunit = g/cm3
  Dvalue = 13.31
  Group = -> [Hf_element001]
  conduct = 2
  density = 1
  expand = 3
  formula = Hf
  name = G4_Hf
  specific = 4
FEATURE [App::DocumentObjectGroupPython] Ta_element001  label="Ta_element : 1"  # scripted group (container) (typed FeaturePython)
  n = 1
  ref = Ta_element
FEATURE [App::DocumentObjectGroupPython] G4_Ta  # scripted group (container) (typed FeaturePython)
  Dunit = g/cm3
  Dvalue = 16.654
  Group = -> [Ta_element001]
  conduct = 2
  density = 1
  expand = 3
  formula = Ta
  name = G4_Ta
  specific = 4
FEATURE [App::DocumentObjectGroupPython] W_element004  label="W_element : 004"  # scripted group (container) (typed FeaturePython)
  n = 1
  ref = W_element
FEATURE [App::DocumentObjectGroupPython] G4_W  # scripted group (container) (typed FeaturePython)
  Dunit = g/cm3
  Dvalue = 19.3
  Group = -> [W_element004]
  conduct = 2
  density = 1
  expand = 3
  formula = W
  name = G4_W
  specific = 4
FEATURE [App::DocumentObjectGroupPython] Re_element001  label="Re_element : 1"  # scripted group (container) (typed FeaturePython)
  n = 1
  ref = Re_element
FEATURE [App::DocumentObjectGroupPython] G4_Re  # scripted group (container) (typed FeaturePython)
  Dunit = g/cm3
  Dvalue = 21.02
  Group = -> [Re_element001]
  conduct = 2
  density = 1
  expand = 3
  formula = Re
  name = G4_Re
  specific = 4
FEATURE [App::DocumentObjectGroupPython] Os_element001  label="Os_element : 1"  # scripted group (container) (typed FeaturePython)
  n = 1
  ref = Os_element
FEATURE [App::DocumentObjectGroupPython] G4_Os  # scripted group (container) (typed FeaturePython)
  Dunit = g/cm3
  Dvalue = 22.57
  Group = -> [Os_element001]
  conduct = 2
  density = 1
  expand = 3
  formula = Os
  name = G4_Os
  specific = 4
FEATURE [App::DocumentObjectGroupPython] Ir_element001  label="Ir_element : 1"  # scripted group (container) (typed FeaturePython)
  n = 1
  ref = Ir_element
FEATURE [App::DocumentObjectGroupPython] G4_Ir  # scripted group (container) (typed FeaturePython)
  Dunit = g/cm3
  Dvalue = 22.42
  Group = -> [Ir_element001]
  conduct = 2
  density = 1
  expand = 3
  formula = Ir
  name = G4_Ir
  specific = 4
FEATURE [App::DocumentObjectGroupPython] Pt_element001  label="Pt_element : 1"  # scripted group (container) (typed FeaturePython)
  n = 1
  ref = Pt_element
FEATURE [App::DocumentObjectGroupPython] G4_Pt  # scripted group (container) (typed FeaturePython)
  Dunit = g/cm3
  Dvalue = 21.45
  Group = -> [Pt_element001]
  conduct = 2
  density = 1
  expand = 3
  formula = Pt
  name = G4_Pt
  specific = 4
FEATURE [App::DocumentObjectGroupPython] Au_element001  label="Au_element : 1"  # scripted group (container) (typed FeaturePython)
  n = 1
  ref = Au_element
FEATURE [App::DocumentObjectGroupPython] G4_Au  # scripted group (container) (typed FeaturePython)
  Dunit = g/cm3
  Dvalue = 19.32
  Group = -> [Au_element001]
  conduct = 2
  density = 1
  expand = 3
  formula = Au
  name = G4_Au
  specific = 4
FEATURE [App::DocumentObjectGroupPython] Hg_element002  label="Hg_element : 002"  # scripted group (container) (typed FeaturePython)
  n = 1
  ref = Hg_element
FEATURE [App::DocumentObjectGroupPython] G4_Hg  # scripted group (container) (typed FeaturePython)
  Dunit = g/cm3
  Dvalue = 13.546
  Group = -> [Hg_element002]
  conduct = 2
  density = 1
  expand = 3
  formula = Hg
  name = G4_Hg
  specific = 4
FEATURE [App::DocumentObjectGroupPython] Tl_element002  label="Tl_element : 002"  # scripted group (container) (typed FeaturePython)
  n = 1
  ref = Tl_element
FEATURE [App::DocumentObjectGroupPython] G4_Tl  # scripted group (container) (typed FeaturePython)
  Dunit = g/cm3
  Dvalue = 11.72
  Group = -> [Tl_element002]
  conduct = 2
  density = 1
  expand = 3
  formula = Tl
  name = G4_Tl
  specific = 4
FEATURE [App::DocumentObjectGroupPython] Pb_element003  label="Pb_element : 1"  # scripted group (container) (typed FeaturePython)
  n = 1
  ref = Pb_element
FEATURE [App::DocumentObjectGroupPython] G4_Pb  # scripted group (container) (typed FeaturePython)
  Dunit = g/cm3
  Dvalue = 11.35
  Group = -> [Pb_element003]
  conduct = 2
  density = 1
  expand = 3
  formula = Pb
  name = G4_Pb
  specific = 4
FEATURE [App::DocumentObjectGroupPython] Bi_element002  label="Bi_element : 1"  # scripted group (container) (typed FeaturePython)
  n = 1
  ref = Bi_element
FEATURE [App::DocumentObjectGroupPython] G4_Bi  # scripted group (container) (typed FeaturePython)
  Dunit = g/cm3
  Dvalue = 9.747
  Group = -> [Bi_element002]
  conduct = 2
  density = 1
  expand = 3
  formula = Bi
  name = G4_Bi
  specific = 4
FEATURE [App::DocumentObjectGroupPython] Po_element001  label="Po_element : 1"  # scripted group (container) (typed FeaturePython)
  n = 1
  ref = Po_element
FEATURE [App::DocumentObjectGroupPython] G4_Po  # scripted group (container) (typed FeaturePython)
  Dunit = g/cm3
  Dvalue = 9.32
  Group = -> [Po_element001]
  conduct = 2
  density = 1
  expand = 3
  formula = Po
  name = G4_Po
  specific = 4
FEATURE [App::DocumentObjectGroupPython] At_element001  label="At_element : 1"  # scripted group (container) (typed FeaturePython)
  n = 1
  ref = At_element
FEATURE [App::DocumentObjectGroupPython] G4_At  # scripted group (container) (typed FeaturePython)
  Dunit = g/cm3
  Dvalue = 9.32
  Group = -> [At_element001]
  conduct = 2
  density = 1
  expand = 3
  formula = At
  name = G4_At
  specific = 4
FEATURE [App::DocumentObjectGroupPython] Rn_element001  label="Rn_element : 1"  # scripted group (container) (typed FeaturePython)
  n = 1
  ref = Rn_element
FEATURE [App::DocumentObjectGroupPython] G4_Rn  # scripted group (container) (typed FeaturePython)
  Dunit = g/cm3
  Dvalue = 0.00900662
  Group = -> [Rn_element001]
  conduct = 2
  density = 1
  expand = 3
  formula = Rn
  name = G4_Rn
  specific = 4
FEATURE [App::DocumentObjectGroupPython] Fr_element001  label="Fr_element : 1"  # scripted group (container) (typed FeaturePython)
  n = 1
  ref = Fr_element
FEATURE [App::DocumentObjectGroupPython] G4_Fr  # scripted group (container) (typed FeaturePython)
  Dunit = g/cm3
  Dvalue = 1
  Group = -> [Fr_element001]
  conduct = 2
  density = 1
  expand = 3
  formula = Fr
  name = G4_Fr
  specific = 4
FEATURE [App::DocumentObjectGroupPython] Ra_element001  label="Ra_element : 1"  # scripted group (container) (typed FeaturePython)
  n = 1
  ref = Ra_element
FEATURE [App::DocumentObjectGroupPython] G4_Ra  # scripted group (container) (typed FeaturePython)
  Dunit = g/cm3
  Dvalue = 5
  Group = -> [Ra_element001]
  conduct = 2
  density = 1
  expand = 3
  formula = Ra
  name = G4_Ra
  specific = 4
FEATURE [App::DocumentObjectGroupPython] Ac_element001  label="Ac_element : 1"  # scripted group (container) (typed FeaturePython)
  n = 1
  ref = Ac_element
FEATURE [App::DocumentObjectGroupPython] G4_Ac  # scripted group (container) (typed FeaturePython)
  Dunit = g/cm3
  Dvalue = 10.07
  Group = -> [Ac_element001]
  conduct = 2
  density = 1
  expand = 3
  formula = Ac
  name = G4_Ac
  specific = 4
FEATURE [App::DocumentObjectGroupPython] Th_element001  label="Th_element : 1"  # scripted group (container) (typed FeaturePython)
  n = 1
  ref = Th_element
FEATURE [App::DocumentObjectGroupPython] G4_Th  # scripted group (container) (typed FeaturePython)
  Dunit = g/cm3
  Dvalue = 11.72
  Group = -> [Th_element001]
  conduct = 2
  density = 1
  expand = 3
  formula = Th
  name = G4_Th
  specific = 4
FEATURE [App::DocumentObjectGroupPython] Pa_element001  label="Pa_element : 1"  # scripted group (container) (typed FeaturePython)
  n = 1
  ref = Pa_element
FEATURE [App::DocumentObjectGroupPython] G4_Pa  # scripted group (container) (typed FeaturePython)
  Dunit = g/cm3
  Dvalue = 15.37
  Group = -> [Pa_element001]
  conduct = 2
  density = 1
  expand = 3
  formula = Pa
  name = G4_Pa
  specific = 4
FEATURE [App::DocumentObjectGroupPython] U_element004  label="U_element : 004"  # scripted group (container) (typed FeaturePython)
  n = 1
  ref = U_element
FEATURE [App::DocumentObjectGroupPython] G4_U  # scripted group (container) (typed FeaturePython)
  Dunit = g/cm3
  Dvalue = 18.95
  Group = -> [U_element004]
  conduct = 2
  density = 1
  expand = 3
  formula = U
  name = G4_U
  specific = 4
FEATURE [App::DocumentObjectGroupPython] Np_element001  label="Np_element : 1"  # scripted group (container) (typed FeaturePython)
  n = 1
  ref = Np_element
FEATURE [App::DocumentObjectGroupPython] G4_Np  # scripted group (container) (typed FeaturePython)
  Dunit = g/cm3
  Dvalue = 20.25
  Group = -> [Np_element001]
  conduct = 2
  density = 1
  expand = 3
  formula = Np
  name = G4_Np
  specific = 4
FEATURE [App::DocumentObjectGroupPython] Pu_element002  label="Pu_element : 002"  # scripted group (container) (typed FeaturePython)
  n = 1
  ref = Pu_element
FEATURE [App::DocumentObjectGroupPython] G4_Pu  # scripted group (container) (typed FeaturePython)
  Dunit = g/cm3
  Dvalue = 19.84
  Group = -> [Pu_element002]
  conduct = 2
  density = 1
  expand = 3
  formula = Pu
  name = G4_Pu
  specific = 4
FEATURE [App::DocumentObjectGroupPython] Am_element001  label="Am_element : 1"  # scripted group (container) (typed FeaturePython)
  n = 1
  ref = Am_element
FEATURE [App::DocumentObjectGroupPython] G4_Am  # scripted group (container) (typed FeaturePython)
  Dunit = g/cm3
  Dvalue = 13.67
  Group = -> [Am_element001]
  conduct = 2
  density = 1
  expand = 3
  formula = Am
  name = G4_Am
  specific = 4
FEATURE [App::DocumentObjectGroupPython] Cm_element001  label="Cm_element : 1"  # scripted group (container) (typed FeaturePython)
  n = 1
  ref = Cm_element
FEATURE [App::DocumentObjectGroupPython] G4_Cm  # scripted group (container) (typed FeaturePython)
  Dunit = g/cm3
  Dvalue = 13.51
  Group = -> [Cm_element001]
  conduct = 2
  density = 1
  expand = 3
  formula = Cm
  name = G4_Cm
  specific = 4
FEATURE [App::DocumentObjectGroupPython] Bk_element001  label="Bk_element : 1"  # scripted group (container) (typed FeaturePython)
  n = 1
  ref = Bk_element
FEATURE [App::DocumentObjectGroupPython] G4_Bk  # scripted group (container) (typed FeaturePython)
  Dunit = g/cm3
  Dvalue = 14
  Group = -> [Bk_element001]
  conduct = 2
  density = 1
  expand = 3
  formula = Bk
  name = G4_Bk
  specific = 4
FEATURE [App::DocumentObjectGroupPython] Cf_element001  label="Cf_element : 1"  # scripted group (container) (typed FeaturePython)
  n = 1
  ref = Cf_element
FEATURE [App::DocumentObjectGroupPython] G4_Cf  # scripted group (container) (typed FeaturePython)
  Dunit = g/cm3
  Dvalue = 10
  Group = -> [Cf_element001]
  conduct = 2
  density = 1
  expand = 3
  formula = Cf
  name = G4_Cf
  specific = 4
FEATURE [App::DocumentObjectGroupPython] Element  # scripted group (container) (typed FeaturePython)
  Group = -> [G4_H,G4_He,G4_Li,G4_Be,G4_B,G4_C,G4_N,G4_O,G4_F,G4_Ne,G4_Na,G4_Mg,G4_Al,G4_Si,G4_P,G4_S,G4_Cl,G4_Ar,G4_K,G4_Ca,G4_Sc,G4_Ti,G4_V,G4_Cr,G4_Mn,G4_Fe,G4_Co,G4_Ni,G4_Cu,G4_Zn,G4_Ga,G4_Ge,G4_As,G4_Se,G4_Br,G4_Kr,G4_Rb,G4_Sr,G4_Y,G4_Zr,G4_Nb,G4_Mo,G4_Tc,G4_Ru,G4_Rh,G4_Pd,G4_Ag,G4_Cd,G4_In,G4_Sn,G4_Sb,G4_Te,G4_I,G4_Xe,G4_Cs,G4_Ba,G4_La,G4_Ce,G4_Pr,G4_Nd,G4_Pm,G4_Sm,G4_Eu,G4_Gd,G4_Tb,G4_Dy,G4_Ho,G4_Er,+30 more]
FEATURE [App::DocumentObjectGroupPython] H_element114  label="H_element : 063"  # scripted group (container) (typed FeaturePython)
  n = 2
  ref = H_element
FEATURE [App::DocumentObjectGroupPython] G4_lH2  # scripted group (container) (typed FeaturePython)
  Dunit = g/cm3
  Dvalue = 0.0708
  Group = -> [H_element114]
  conduct = 2
  density = 1
  expand = 3
  formula = G4_lH2
  name = G4_lH2
  specific = 4
FEATURE [App::DocumentObjectGroupPython] N_element049  label="N_element : 022"  # scripted group (container) (typed FeaturePython)
  n = 2
  ref = N_element
FEATURE [App::DocumentObjectGroupPython] G4_lN2  # scripted group (container) (typed FeaturePython)
  Dunit = g/cm3
  Dvalue = 0.807
  Group = -> [N_element049]
  conduct = 2
  density = 1
  expand = 3
  formula = G4_lN2
  name = G4_lN2
  specific = 4
FEATURE [App::DocumentObjectGroupPython] O_element106  label="O_element : 060"  # scripted group (container) (typed FeaturePython)
  n = 2
  ref = O_element
FEATURE [App::DocumentObjectGroupPython] G4_lO2  # scripted group (container) (typed FeaturePython)
  Dunit = g/cm3
  Dvalue = 1.141
  Group = -> [O_element106]
  conduct = 2
  density = 1
  expand = 3
  formula = G4_lO2
  name = G4_lO2
  specific = 4
FEATURE [App::DocumentObjectGroupPython] Ar_element003  label="Ar_element : 002"  # scripted group (container) (typed FeaturePython)
  n = 1
  ref = Ar_element
FEATURE [App::DocumentObjectGroupPython] G4_lAr  # scripted group (container) (typed FeaturePython)
  Dunit = g/cm3
  Dvalue = 1.396
  Group = -> [Ar_element003]
  conduct = 2
  density = 1
  expand = 3
  formula = G4_lAr
  name = G4_lAr
  specific = 4
FEATURE [App::DocumentObjectGroupPython] Br_element008  label="Br_element : 005"  # scripted group (container) (typed FeaturePython)
  n = 1
  ref = Br_element
FEATURE [App::DocumentObjectGroupPython] G4_lBr  # scripted group (container) (typed FeaturePython)
  Dunit = g/cm3
  Dvalue = 3.1028
  Group = -> [Br_element008]
  conduct = 2
  density = 1
  expand = 3
  formula = G4_lBr
  name = G4_lBr
  specific = 4
FEATURE [App::DocumentObjectGroupPython] Kr_element002  label="Kr_element : 002"  # scripted group (container) (typed FeaturePython)
  n = 1
  ref = Kr_element
FEATURE [App::DocumentObjectGroupPython] G4_lKr  # scripted group (container) (typed FeaturePython)
  Dunit = g/cm3
  Dvalue = 2.418
  Group = -> [Kr_element002]
  conduct = 2
  density = 1
  expand = 3
  formula = G4_lKr
  name = G4_lKr
  specific = 4
FEATURE [App::DocumentObjectGroupPython] Xe_element002  label="Xe_element : 002"  # scripted group (container) (typed FeaturePython)
  n = 1
  ref = Xe_element
FEATURE [App::DocumentObjectGroupPython] G4_lXe  # scripted group (container) (typed FeaturePython)
  Dunit = g/cm3
  Dvalue = 2.953
  Group = -> [Xe_element002]
  conduct = 2
  density = 1
  expand = 3
  formula = G4_lXe
  name = G4_lXe
  specific = 4
FEATURE [App::DocumentObjectGroupPython] O_element107  label="O_element : 061"  # scripted group (container) (typed FeaturePython)
  n = 4
  ref = O_element
FEATURE [App::DocumentObjectGroupPython] Pb_element004  label="Pb_element : 002"  # scripted group (container) (typed FeaturePython)
  n = 1
  ref = Pb_element
FEATURE [App::DocumentObjectGroupPython] W_element005  label="W_element : 005"  # scripted group (container) (typed FeaturePython)
  n = 1
  ref = W_element
FEATURE [App::DocumentObjectGroupPython] G4_PbWO4  # scripted group (container) (typed FeaturePython)
  Dunit = g/cm3
  Dvalue = 8.28
  Group = -> [O_element107,Pb_element004,W_element005]
  conduct = 2
  density = 1
  expand = 3
  formula = G4_PbWO4
  name = G4_PbWO4
  specific = 4
FEATURE [App::DocumentObjectGroupPython] H_element115  label="H_element : 064"  # scripted group (container) (typed FeaturePython)
  n = 1
  ref = H_element
FEATURE [App::DocumentObjectGroupPython] G4_Galactic  # scripted group (container) (typed FeaturePython)
  Dunit = g/cm3
  Dvalue = 0
  Group = -> [H_element115]
  conduct = 2
  density = 1
  expand = 3
  formula = G4_Galactic
  name = G4_Galactic
  specific = 4
FEATURE [App::DocumentObjectGroupPython] C_element125  label="C_element : 071"  # scripted group (container) (typed FeaturePython)
  n = 1
  ref = C_element
FEATURE [App::DocumentObjectGroupPython] G4_GRAPHITE_POROUS  # scripted group (container) (typed FeaturePython)
  Dunit = g/cm3
  Dvalue = 1.7
  Group = -> [C_element125]
  conduct = 2
  density = 1
  expand = 3
  formula = G4_GRAPHITE_POROUS
  name = G4_GRAPHITE_POROUS
  specific = 4
FEATURE [App::DocumentObjectGroupPython] H_element116  label="H_element : 0.150"  # scripted group (container) (typed FeaturePython)
  n = 0.080538
FEATURE [App::DocumentObjectGroupPython] C_element126  label="C_element : 0.600"  # scripted group (container) (typed FeaturePython)
  n = 0.599848
FEATURE [App::DocumentObjectGroupPython] O_element108  label="O_element : 0.320"  # scripted group (container) (typed FeaturePython)
  n = 0.319614
FEATURE [App::DocumentObjectGroupPython] G4_LUCITE  # scripted group (container) (typed FeaturePython)
  Dunit = g/cm3
  Dvalue = 1.19
  Group = -> [H_element116,C_element126,O_element108]
  conduct = 2
  density = 1
  expand = 3
  formula = G4_LUCITE
  name = G4_LUCITE
  specific = 4
FEATURE [App::DocumentObjectGroupPython] Cu_element002  label="Cu_element : 62"  # scripted group (container) (typed FeaturePython)
  n = 62
  ref = Cu_element
FEATURE [App::DocumentObjectGroupPython] Zn_element002  label="Zn_element : 35"  # scripted group (container) (typed FeaturePython)
  n = 35
  ref = Zn_element
FEATURE [App::DocumentObjectGroupPython] Pb_element005  label="Pb_element : 3"  # scripted group (container) (typed FeaturePython)
  n = 3
  ref = Pb_element
FEATURE [App::DocumentObjectGroupPython] G4_BRASS  # scripted group (container) (typed FeaturePython)
  Dunit = g/cm3
  Dvalue = 8.52
  Group = -> [Cu_element002,Zn_element002,Pb_element005]
  conduct = 2
  density = 1
  expand = 3
  formula = G4_BRASS
  name = G4_BRASS
  specific = 4
FEATURE [App::DocumentObjectGroupPython] Cu_element003  label="Cu_element : 89"  # scripted group (container) (typed FeaturePython)
  n = 89
  ref = Cu_element
FEATURE [App::DocumentObjectGroupPython] Zn_element003  label="Zn_element : 9"  # scripted group (container) (typed FeaturePython)
  n = 9
  ref = Zn_element
FEATURE [App::DocumentObjectGroupPython] Pb_element006  label="Pb_element : 2"  # scripted group (container) (typed FeaturePython)
  n = 2
  ref = Pb_element
FEATURE [App::DocumentObjectGroupPython] G4_BRONZE  # scripted group (container) (typed FeaturePython)
  Dunit = g/cm3
  Dvalue = 8.82
  Group = -> [Cu_element003,Zn_element003,Pb_element006]
  conduct = 2
  density = 1
  expand = 3
  formula = G4_BRONZE
  name = G4_BRONZE
  specific = 4
FEATURE [App::DocumentObjectGroupPython] Fe_element008  label="Fe_element : 74"  # scripted group (container) (typed FeaturePython)
  n = 74
  ref = Fe_element
FEATURE [App::DocumentObjectGroupPython] Cr_element002  label="Cr_element : 18"  # scripted group (container) (typed FeaturePython)
  n = 18
  ref = Cr_element
FEATURE [App::DocumentObjectGroupPython] Ni_element002  label="Ni_element : 8"  # scripted group (container) (typed FeaturePython)
  n = 8
  ref = Ni_element
FEATURE [App::DocumentObjectGroupPython] G4_STAINLESS_STEEL  label="G4_STAINLESS-STEEL"  # scripted group (container) (typed FeaturePython)
  Dunit = g/cm3
  Dvalue = 8
  Group = -> [Fe_element008,Cr_element002,Ni_element002]
  conduct = 2
  density = 1
  expand = 3
  formula = G4_STAINLESS-STEEL
  name = G4_STAINLESS-STEEL
  specific = 4
FEATURE [App::DocumentObjectGroupPython] H_element117  label="H_element : 065"  # scripted group (container) (typed FeaturePython)
  n = 18
  ref = H_element
FEATURE [App::DocumentObjectGroupPython] C_element127  label="C_element : 072"  # scripted group (container) (typed FeaturePython)
  n = 12
  ref = C_element
FEATURE [App::DocumentObjectGroupPython] O_element109  label="O_element : 062"  # scripted group (container) (typed FeaturePython)
  n = 7
  ref = O_element
FEATURE [App::DocumentObjectGroupPython] G4_CR39  # scripted group (container) (typed FeaturePython)
  Dunit = g/cm3
  Dvalue = 1.32
  Group = -> [H_element117,C_element127,O_element109]
  conduct = 2
  density = 1
  expand = 3
  formula = G4_CR39
  name = G4_CR39
  specific = 4
FEATURE [App::DocumentObjectGroupPython] H_element118  label="H_element : 38"  # scripted group (container) (typed FeaturePython)
  n = 38
  ref = H_element
FEATURE [App::DocumentObjectGroupPython] C_element128  label="C_element : 073"  # scripted group (container) (typed FeaturePython)
  n = 18
  ref = C_element
FEATURE [App::DocumentObjectGroupPython] O_element110  label="O_element : 063"  # scripted group (container) (typed FeaturePython)
  n = 1
  ref = O_element
FEATURE [App::DocumentObjectGroupPython] G4_OCTADECANOL  # scripted group (container) (typed FeaturePython)
  Dunit = g/cm3
  Dvalue = 0.812
  Group = -> [H_element118,C_element128,O_element110]
  conduct = 2
  density = 1
  expand = 3
  formula = G4_OCTADECANOL
  name = G4_OCTADECANOL
  specific = 4
FEATURE [App::DocumentObjectGroupPython] HEP  # scripted group (container) (typed FeaturePython)
  Group = -> [G4_lH2,G4_lN2,G4_lO2,G4_lAr,G4_lBr,G4_lKr,G4_lXe,G4_PbWO4,G4_Galactic,G4_GRAPHITE_POROUS,G4_LUCITE,G4_BRASS,G4_BRONZE,G4_STAINLESS_STEEL,G4_CR39,G4_OCTADECANOL]
FEATURE [App::DocumentObjectGroupPython] C_element129  label="C_element : 074"  # scripted group (container) (typed FeaturePython)
  n = 14
  ref = C_element
FEATURE [App::DocumentObjectGroupPython] H_element119  label="H_element : 066"  # scripted group (container) (typed FeaturePython)
  n = 10
  ref = H_element
FEATURE [App::DocumentObjectGroupPython] O_element111  label="O_element : 064"  # scripted group (container) (typed FeaturePython)
  n = 2
  ref = O_element
FEATURE [App::DocumentObjectGroupPython] N_element050  label="N_element : 023"  # scripted group (container) (typed FeaturePython)
  n = 2
  ref = N_element
FEATURE [App::DocumentObjectGroupPython] G4_KEVLAR  # scripted group (container) (typed FeaturePython)
  Dunit = g/cm3
  Dvalue = 1.44
  Group = -> [C_element129,H_element119,O_element111,N_element050]
  conduct = 2
  density = 1
  expand = 3
  formula = G4_KEVLAR
  name = G4_KEVLAR
  specific = 4
FEATURE [App::DocumentObjectGroupPython] C_element130  label="C_element : 075"  # scripted group (container) (typed FeaturePython)
  n = 10
  ref = C_element
FEATURE [App::DocumentObjectGroupPython] H_element120  label="H_element : 067"  # scripted group (container) (typed FeaturePython)
  n = 8
  ref = H_element
FEATURE [App::DocumentObjectGroupPython] O_element112  label="O_element : 065"  # scripted group (container) (typed FeaturePython)
  n = 4
  ref = O_element
FEATURE [App::DocumentObjectGroupPython] G4_DACRON  # scripted group (container) (typed FeaturePython)
  Dunit = g/cm3
  Dvalue = 1.4
  Group = -> [C_element130,H_element120,O_element112]
  conduct = 2
  density = 1
  expand = 3
  formula = G4_DACRON
  name = G4_DACRON
  specific = 4
FEATURE [App::DocumentObjectGroupPython] C_element131  label="C_element : 076"  # scripted group (container) (typed FeaturePython)
  n = 4
  ref = C_element
FEATURE [App::DocumentObjectGroupPython] H_element121  label="H_element : 068"  # scripted group (container) (typed FeaturePython)
  n = 5
  ref = H_element
FEATURE [App::DocumentObjectGroupPython] Cl_element030  label="Cl_element : 016"  # scripted group (container) (typed FeaturePython)
  n = 1
  ref = Cl_element
FEATURE [App::DocumentObjectGroupPython] G4_NEOPRENE  # scripted group (container) (typed FeaturePython)
  Dunit = g/cm3
  Dvalue = 1.23
  Group = -> [C_element131,H_element121,Cl_element030]
  conduct = 2
  density = 1
  expand = 3
  formula = G4_NEOPRENE
  name = G4_NEOPRENE
  specific = 4
FEATURE [App::DocumentObjectGroupPython] Space  # scripted group (container) (typed FeaturePython)
  Group = -> [G4_KEVLAR,G4_DACRON,G4_NEOPRENE]
FEATURE [App::DocumentObjectGroupPython] H_element122  label="H_element : 069"  # scripted group (container) (typed FeaturePython)
  n = 5
  ref = H_element
FEATURE [App::DocumentObjectGroupPython] C_element132  label="C_element : 077"  # scripted group (container) (typed FeaturePython)
  n = 4
  ref = C_element
FEATURE [App::DocumentObjectGroupPython] N_element051  label="N_element : 3"  # scripted group (container) (typed FeaturePython)
  n = 3
  ref = N_element
FEATURE [App::DocumentObjectGroupPython] O_element113  label="O_element : 066"  # scripted group (container) (typed FeaturePython)
  n = 1
  ref = O_element
FEATURE [App::DocumentObjectGroupPython] G4_CYTOSINE  # scripted group (container) (typed FeaturePython)
  Dunit = g/cm3
  Dvalue = 1.55
  Group = -> [H_element122,C_element132,N_element051,O_element113]
  conduct = 2
  density = 1
  expand = 3
  formula = G4_CYTOSINE
  name = G4_CYTOSINE
  specific = 4
FEATURE [App::DocumentObjectGroupPython] H_element123  label="H_element : 070"  # scripted group (container) (typed FeaturePython)
  n = 6
  ref = H_element
FEATURE [App::DocumentObjectGroupPython] C_element133  label="C_element : 078"  # scripted group (container) (typed FeaturePython)
  n = 5
  ref = C_element
FEATURE [App::DocumentObjectGroupPython] N_element052  label="N_element : 024"  # scripted group (container) (typed FeaturePython)
  n = 2
  ref = N_element
FEATURE [App::DocumentObjectGroupPython] O_element114  label="O_element : 067"  # scripted group (container) (typed FeaturePython)
  n = 2
  ref = O_element
FEATURE [App::DocumentObjectGroupPython] G4_THYMINE  # scripted group (container) (typed FeaturePython)
  Dunit = g/cm3
  Dvalue = 1.23
  Group = -> [H_element123,C_element133,N_element052,O_element114]
  conduct = 2
  density = 1
  expand = 3
  formula = G4_THYMINE
  name = G4_THYMINE
  specific = 4
FEATURE [App::DocumentObjectGroupPython] H_element124  label="H_element : 071"  # scripted group (container) (typed FeaturePython)
  n = 4
  ref = H_element
FEATURE [App::DocumentObjectGroupPython] C_element134  label="C_element : 079"  # scripted group (container) (typed FeaturePython)
  n = 4
  ref = C_element
FEATURE [App::DocumentObjectGroupPython] N_element053  label="N_element : 025"  # scripted group (container) (typed FeaturePython)
  n = 2
  ref = N_element
FEATURE [App::DocumentObjectGroupPython] O_element115  label="O_element : 068"  # scripted group (container) (typed FeaturePython)
  n = 2
  ref = O_element
FEATURE [App::DocumentObjectGroupPython] G4_URACIL  # scripted group (container) (typed FeaturePython)
  Dunit = g/cm3
  Dvalue = 1.32
  Group = -> [H_element124,C_element134,N_element053,O_element115]
  conduct = 2
  density = 1
  expand = 3
  formula = G4_URACIL
  name = G4_URACIL
  specific = 4
FEATURE [App::DocumentObjectGroupPython] H_element125  label="H_element : 072"  # scripted group (container) (typed FeaturePython)
  n = 4
  ref = H_element
FEATURE [App::DocumentObjectGroupPython] C_element135  label="C_element : 080"  # scripted group (container) (typed FeaturePython)
  n = 5
  ref = C_element
FEATURE [App::DocumentObjectGroupPython] N_element054  label="N_element : 026"  # scripted group (container) (typed FeaturePython)
  n = 5
  ref = N_element
FEATURE [App::DocumentObjectGroupPython] G4_DNA_ADENINE  # scripted group (container) (typed FeaturePython)
  Dunit = g/cm3
  Dvalue = 1
  Group = -> [H_element125,C_element135,N_element054]
  conduct = 2
  density = 1
  expand = 3
  formula = G4_DNA_ADENINE
  name = G4_DNA_ADENINE
  specific = 4
FEATURE [App::DocumentObjectGroupPython] H_element126  label="H_element : 073"  # scripted group (container) (typed FeaturePython)
  n = 4
  ref = H_element
FEATURE [App::DocumentObjectGroupPython] C_element136  label="C_element : 081"  # scripted group (container) (typed FeaturePython)
  n = 5
  ref = C_element
FEATURE [App::DocumentObjectGroupPython] N_element055  label="N_element : 027"  # scripted group (container) (typed FeaturePython)
  n = 5
  ref = N_element
FEATURE [App::DocumentObjectGroupPython] O_element116  label="O_element : 069"  # scripted group (container) (typed FeaturePython)
  n = 1
  ref = O_element
FEATURE [App::DocumentObjectGroupPython] G4_DNA_GUANINE  # scripted group (container) (typed FeaturePython)
  Dunit = g/cm3
  Dvalue = 1
  Group = -> [H_element126,C_element136,N_element055,O_element116]
  conduct = 2
  density = 1
  expand = 3
  formula = G4_DNA_GUANINE
  name = G4_DNA_GUANINE
  specific = 4
FEATURE [App::DocumentObjectGroupPython] H_element127  label="H_element : 074"  # scripted group (container) (typed FeaturePython)
  n = 4
  ref = H_element
FEATURE [App::DocumentObjectGroupPython] C_element137  label="C_element : 082"  # scripted group (container) (typed FeaturePython)
  n = 4
  ref = C_element
FEATURE [App::DocumentObjectGroupPython] N_element056  label="N_element : 028"  # scripted group (container) (typed FeaturePython)
  n = 3
  ref = N_element
FEATURE [App::DocumentObjectGroupPython] O_element117  label="O_element : 070"  # scripted group (container) (typed FeaturePython)
  n = 1
  ref = O_element
FEATURE [App::DocumentObjectGroupPython] G4_DNA_CYTOSINE  # scripted group (container) (typed FeaturePython)
  Dunit = g/cm3
  Dvalue = 1
  Group = -> [H_element127,C_element137,N_element056,O_element117]
  conduct = 2
  density = 1
  expand = 3
  formula = G4_DNA_CYTOSINE
  name = G4_DNA_CYTOSINE
  specific = 4
FEATURE [App::DocumentObjectGroupPython] H_element128  label="H_element : 075"  # scripted group (container) (typed FeaturePython)
  n = 5
  ref = H_element
FEATURE [App::DocumentObjectGroupPython] C_element138  label="C_element : 083"  # scripted group (container) (typed FeaturePython)
  n = 5
  ref = C_element
FEATURE [App::DocumentObjectGroupPython] N_element057  label="N_element : 029"  # scripted group (container) (typed FeaturePython)
  n = 2
  ref = N_element
FEATURE [App::DocumentObjectGroupPython] O_element118  label="O_element : 071"  # scripted group (container) (typed FeaturePython)
  n = 2
  ref = O_element
FEATURE [App::DocumentObjectGroupPython] G4_DNA_THYMINE  # scripted group (container) (typed FeaturePython)
  Dunit = g/cm3
  Dvalue = 1
  Group = -> [H_element128,C_element138,N_element057,O_element118]
  conduct = 2
  density = 1
  expand = 3
  formula = G4_DNA_THYMINE
  name = G4_DNA_THYMINE
  specific = 4
FEATURE [App::DocumentObjectGroupPython] H_element129  label="H_element : 076"  # scripted group (container) (typed FeaturePython)
  n = 3
  ref = H_element
FEATURE [App::DocumentObjectGroupPython] C_element139  label="C_element : 084"  # scripted group (container) (typed FeaturePython)
  n = 4
  ref = C_element
FEATURE [App::DocumentObjectGroupPython] N_element058  label="N_element : 030"  # scripted group (container) (typed FeaturePython)
  n = 2
  ref = N_element
FEATURE [App::DocumentObjectGroupPython] O_element119  label="O_element : 072"  # scripted group (container) (typed FeaturePython)
  n = 2
  ref = O_element
FEATURE [App::DocumentObjectGroupPython] G4_DNA_URACIL  # scripted group (container) (typed FeaturePython)
  Dunit = g/cm3
  Dvalue = 1
  Group = -> [H_element129,C_element139,N_element058,O_element119]
  conduct = 2
  density = 1
  expand = 3
  formula = G4_DNA_URACIL
  name = G4_DNA_URACIL
  specific = 4
FEATURE [App::DocumentObjectGroupPython] H_element130  label="H_element : 077"  # scripted group (container) (typed FeaturePython)
  n = 10
  ref = H_element
FEATURE [App::DocumentObjectGroupPython] C_element140  label="C_element : 085"  # scripted group (container) (typed FeaturePython)
  n = 10
  ref = C_element
FEATURE [App::DocumentObjectGroupPython] N_element059  label="N_element : 031"  # scripted group (container) (typed FeaturePython)
  n = 5
  ref = N_element
FEATURE [App::DocumentObjectGroupPython] O_element120  label="O_element : 073"  # scripted group (container) (typed FeaturePython)
  n = 4
  ref = O_element
FEATURE [App::DocumentObjectGroupPython] G4_DNA_ADENOSINE  # scripted group (container) (typed FeaturePython)
  Dunit = g/cm3
  Dvalue = 1
  Group = -> [H_element130,C_element140,N_element059,O_element120]
  conduct = 2
  density = 1
  expand = 3
  formula = G4_DNA_ADENOSINE
  name = G4_DNA_ADENOSINE
  specific = 4
FEATURE [App::DocumentObjectGroupPython] H_element131  label="H_element : 078"  # scripted group (container) (typed FeaturePython)
  n = 10
  ref = H_element
FEATURE [App::DocumentObjectGroupPython] C_element141  label="C_element : 086"  # scripted group (container) (typed FeaturePython)
  n = 10
  ref = C_element
FEATURE [App::DocumentObjectGroupPython] N_element060  label="N_element : 032"  # scripted group (container) (typed FeaturePython)
  n = 5
  ref = N_element
FEATURE [App::DocumentObjectGroupPython] O_element121  label="O_element : 074"  # scripted group (container) (typed FeaturePython)
  n = 5
  ref = O_element
FEATURE [App::DocumentObjectGroupPython] G4_DNA_GUANOSINE  # scripted group (container) (typed FeaturePython)
  Dunit = g/cm3
  Dvalue = 1
  Group = -> [H_element131,C_element141,N_element060,O_element121]
  conduct = 2
  density = 1
  expand = 3
  formula = G4_DNA_GUANOSINE
  name = G4_DNA_GUANOSINE
  specific = 4
FEATURE [App::DocumentObjectGroupPython] H_element132  label="H_element : 079"  # scripted group (container) (typed FeaturePython)
  n = 10
  ref = H_element
FEATURE [App::DocumentObjectGroupPython] C_element142  label="C_element : 087"  # scripted group (container) (typed FeaturePython)
  n = 9
  ref = C_element
FEATURE [App::DocumentObjectGroupPython] N_element061  label="N_element : 033"  # scripted group (container) (typed FeaturePython)
  n = 3
  ref = N_element
FEATURE [App::DocumentObjectGroupPython] O_element122  label="O_element : 075"  # scripted group (container) (typed FeaturePython)
  n = 5
  ref = O_element
FEATURE [App::DocumentObjectGroupPython] G4_DNA_CYTIDINE  # scripted group (container) (typed FeaturePython)
  Dunit = g/cm3
  Dvalue = 1
  Group = -> [H_element132,C_element142,N_element061,O_element122]
  conduct = 2
  density = 1
  expand = 3
  formula = G4_DNA_CYTIDINE
  name = G4_DNA_CYTIDINE
  specific = 4
FEATURE [App::DocumentObjectGroupPython] H_element133  label="H_element : 080"  # scripted group (container) (typed FeaturePython)
  n = 9
  ref = H_element
FEATURE [App::DocumentObjectGroupPython] C_element143  label="C_element : 088"  # scripted group (container) (typed FeaturePython)
  n = 9
  ref = C_element
FEATURE [App::DocumentObjectGroupPython] N_element062  label="N_element : 034"  # scripted group (container) (typed FeaturePython)
  n = 2
  ref = N_element
FEATURE [App::DocumentObjectGroupPython] O_element123  label="O_element : 076"  # scripted group (container) (typed FeaturePython)
  n = 6
  ref = O_element
FEATURE [App::DocumentObjectGroupPython] G4_DNA_URIDINE  # scripted group (container) (typed FeaturePython)
  Dunit = g/cm3
  Dvalue = 1
  Group = -> [H_element133,C_element143,N_element062,O_element123]
  conduct = 2
  density = 1
  expand = 3
  formula = G4_DNA_URIDINE
  name = G4_DNA_URIDINE
  specific = 4
FEATURE [App::DocumentObjectGroupPython] H_element134  label="H_element : 081"  # scripted group (container) (typed FeaturePython)
  n = 11
  ref = H_element
FEATURE [App::DocumentObjectGroupPython] C_element144  label="C_element : 089"  # scripted group (container) (typed FeaturePython)
  n = 10
  ref = C_element
FEATURE [App::DocumentObjectGroupPython] N_element063  label="N_element : 035"  # scripted group (container) (typed FeaturePython)
  n = 2
  ref = N_element
FEATURE [App::DocumentObjectGroupPython] O_element124  label="O_element : 077"  # scripted group (container) (typed FeaturePython)
  n = 6
  ref = O_element
FEATURE [App::DocumentObjectGroupPython] G4_DNA_METHYLURIDINE  # scripted group (container) (typed FeaturePython)
  Dunit = g/cm3
  Dvalue = 1
  Group = -> [H_element134,C_element144,N_element063,O_element124]
  conduct = 2
  density = 1
  expand = 3
  formula = G4_DNA_METHYLURIDINE
  name = G4_DNA_METHYLURIDINE
  specific = 4
FEATURE [App::DocumentObjectGroupPython] P_element014  label="P_element : 003"  # scripted group (container) (typed FeaturePython)
  n = 1
  ref = P_element
FEATURE [App::DocumentObjectGroupPython] O_element125  label="O_element : 078"  # scripted group (container) (typed FeaturePython)
  n = 3
  ref = O_element
FEATURE [App::DocumentObjectGroupPython] G4_DNA_MONOPHOSPHATE  # scripted group (container) (typed FeaturePython)
  Dunit = g/cm3
  Dvalue = 1
  Group = -> [P_element014,O_element125]
  conduct = 2
  density = 1
  expand = 3
  formula = G4_DNA_MONOPHOSPHATE
  name = G4_DNA_MONOPHOSPHATE
  specific = 4
FEATURE [App::DocumentObjectGroupPython] H_element135  label="H_element : 082"  # scripted group (container) (typed FeaturePython)
  n = 10
  ref = H_element
FEATURE [App::DocumentObjectGroupPython] C_element145  label="C_element : 090"  # scripted group (container) (typed FeaturePython)
  n = 10
  ref = C_element
FEATURE [App::DocumentObjectGroupPython] N_element064  label="N_element : 036"  # scripted group (container) (typed FeaturePython)
  n = 5
  ref = N_element
FEATURE [App::DocumentObjectGroupPython] O_element126  label="O_element : 079"  # scripted group (container) (typed FeaturePython)
  n = 7
  ref = O_element
FEATURE [App::DocumentObjectGroupPython] P_element015  label="P_element : 004"  # scripted group (container) (typed FeaturePython)
  n = 1
  ref = P_element
FEATURE [App::DocumentObjectGroupPython] G4_DNA_A  # scripted group (container) (typed FeaturePython)
  Dunit = g/cm3
  Dvalue = 1
  Group = -> [H_element135,C_element145,N_element064,O_element126,P_element015]
  conduct = 2
  density = 1
  expand = 3
  formula = G4_DNA_A
  name = G4_DNA_A
  specific = 4
FEATURE [App::DocumentObjectGroupPython] H_element136  label="H_element : 083"  # scripted group (container) (typed FeaturePython)
  n = 10
  ref = H_element
FEATURE [App::DocumentObjectGroupPython] C_element146  label="C_element : 091"  # scripted group (container) (typed FeaturePython)
  n = 10
  ref = C_element
FEATURE [App::DocumentObjectGroupPython] N_element065  label="N_element : 037"  # scripted group (container) (typed FeaturePython)
  n = 5
  ref = N_element
FEATURE [App::DocumentObjectGroupPython] O_element127  label="O_element : 8"  # scripted group (container) (typed FeaturePython)
  n = 8
  ref = O_element
FEATURE [App::DocumentObjectGroupPython] P_element016  label="P_element : 005"  # scripted group (container) (typed FeaturePython)
  n = 1
  ref = P_element
FEATURE [App::DocumentObjectGroupPython] G4_DNA_G  # scripted group (container) (typed FeaturePython)
  Dunit = g/cm3
  Dvalue = 1
  Group = -> [H_element136,C_element146,N_element065,O_element127,P_element016]
  conduct = 2
  density = 1
  expand = 3
  formula = G4_DNA_G
  name = G4_DNA_G
  specific = 4
FEATURE [App::DocumentObjectGroupPython] H_element137  label="H_element : 084"  # scripted group (container) (typed FeaturePython)
  n = 10
  ref = H_element
FEATURE [App::DocumentObjectGroupPython] C_element147  label="C_element : 092"  # scripted group (container) (typed FeaturePython)
  n = 9
  ref = C_element
FEATURE [App::DocumentObjectGroupPython] N_element066  label="N_element : 038"  # scripted group (container) (typed FeaturePython)
  n = 3
  ref = N_element
FEATURE [App::DocumentObjectGroupPython] O_element128  label="O_element : 080"  # scripted group (container) (typed FeaturePython)
  n = 8
  ref = O_element
FEATURE [App::DocumentObjectGroupPython] P_element017  label="P_element : 006"  # scripted group (container) (typed FeaturePython)
  n = 1
  ref = P_element
FEATURE [App::DocumentObjectGroupPython] G4_DNA_C  # scripted group (container) (typed FeaturePython)
  Dunit = g/cm3
  Dvalue = 1
  Group = -> [H_element137,C_element147,N_element066,O_element128,P_element017]
  conduct = 2
  density = 1
  expand = 3
  formula = G4_DNA_C
  name = G4_DNA_C
  specific = 4
FEATURE [App::DocumentObjectGroupPython] H_element138  label="H_element : 085"  # scripted group (container) (typed FeaturePython)
  n = 9
  ref = H_element
FEATURE [App::DocumentObjectGroupPython] C_element148  label="C_element : 093"  # scripted group (container) (typed FeaturePython)
  n = 9
  ref = C_element
FEATURE [App::DocumentObjectGroupPython] N_element067  label="N_element : 039"  # scripted group (container) (typed FeaturePython)
  n = 2
  ref = N_element
FEATURE [App::DocumentObjectGroupPython] O_element129  label="O_element : 9"  # scripted group (container) (typed FeaturePython)
  n = 9
  ref = O_element
FEATURE [App::DocumentObjectGroupPython] P_element018  label="P_element : 007"  # scripted group (container) (typed FeaturePython)
  n = 1
  ref = P_element
FEATURE [App::DocumentObjectGroupPython] G4_DNA_U  # scripted group (container) (typed FeaturePython)
  Dunit = g/cm3
  Dvalue = 1
  Group = -> [H_element138,C_element148,N_element067,O_element129,P_element018]
  conduct = 2
  density = 1
  expand = 3
  formula = G4_DNA_U
  name = G4_DNA_U
  specific = 4
FEATURE [App::DocumentObjectGroupPython] H_element139  label="H_element : 086"  # scripted group (container) (typed FeaturePython)
  n = 11
  ref = H_element
FEATURE [App::DocumentObjectGroupPython] C_element149  label="C_element : 094"  # scripted group (container) (typed FeaturePython)
  n = 10
  ref = C_element
FEATURE [App::DocumentObjectGroupPython] N_element068  label="N_element : 040"  # scripted group (container) (typed FeaturePython)
  n = 2
  ref = N_element
FEATURE [App::DocumentObjectGroupPython] O_element130  label="O_element : 081"  # scripted group (container) (typed FeaturePython)
  n = 9
  ref = O_element
FEATURE [App::DocumentObjectGroupPython] P_element019  label="P_element : 008"  # scripted group (container) (typed FeaturePython)
  n = 1
  ref = P_element
FEATURE [App::DocumentObjectGroupPython] G4_DNA_MU  # scripted group (container) (typed FeaturePython)
  Dunit = g/cm3
  Dvalue = 1
  Group = -> [H_element139,C_element149,N_element068,O_element130,P_element019]
  conduct = 2
  density = 1
  expand = 3
  formula = G4_DNA_MU
  name = G4_DNA_MU
  specific = 4
FEATURE [App::DocumentObjectGroupPython] BioChemical  # scripted group (container) (typed FeaturePython)
  Group = -> [G4_CYTOSINE,G4_THYMINE,G4_URACIL,G4_DNA_ADENINE,G4_DNA_GUANINE,G4_DNA_CYTOSINE,G4_DNA_THYMINE,G4_DNA_URACIL,G4_DNA_ADENOSINE,G4_DNA_GUANOSINE,G4_DNA_CYTIDINE,G4_DNA_URIDINE,G4_DNA_METHYLURIDINE,G4_DNA_MONOPHOSPHATE,G4_DNA_A,G4_DNA_G,G4_DNA_C,G4_DNA_U,G4_DNA_MU]
FEATURE [App::DocumentObjectGroupPython] G4Materials  # scripted group (container) (typed FeaturePython)
  Group = -> [NIST,Element,HEP,Space,BioChemical]
  version = 1
FEATURE [App::DocumentObjectGroupPython] Geant4  # scripted group (container) (typed FeaturePython)
  Group = -> [G4Isotopes,G4Elements,G4Materials]
FEATURE [App::DocumentObjectGroupPython] Materials  # scripted group (container) (typed FeaturePython)
  Group = -> [Geant4]
FEATURE [Part::FeaturePython] GDMLBox_WorldBox  # WARN: FeaturePython — macro-defined, semantics opaque (R4)
  lunit = 2
  material = 5
  x = 1000
  y = 3000
  z = 1000
FEATURE [Part::FeaturePython] GDMLBox_Box  # WARN: FeaturePython — macro-defined, semantics opaque (R4)
  lunit = 2
  material = 253
  x = 20
  y = 20
  z = 20
FEATURE [App::Part] LV_Box
  Group = -> [GDMLBox_Box]
  Origin = -> Origin001
FEATURE [Part::FeaturePython] Array  # Draft array (typed FeaturePython)
  AlwaysSyncPlacement = false
  Angle = 360
  ArrayType = 0
  Axis = (0,0,1)
  Base = -> LV_Box
  Center = (0,0,0)
  Count = 31250
  ExpandArray = false
  Fuse = false
  IntervalAxis = (0,0,0)
  IntervalX = (20,0,0)
  IntervalY = (0,20,0)
  IntervalZ = (0,0,20)
  NumberCircles = 3
  NumberPolar = 5
  NumberX = 25
  NumberY = 50
  NumberZ = 25
  Placement = pos=(1.52588e-05,340,1.52588e-05) rot=(0,0,1;0rad)
  PlacementList = 31250 placements: [(0,0,0),(0,0,20),(0,0,40),(0,0,60),(0,0,80),(0,0,100),(0,0,120),(0,0,140),(0,0,160),(0,0,180),(0,0,200),(0,0,220),(0,0,240),(0,0,260),(0,0,280),(0,0,300),(0,0,320),(0,0,340),(0,0,360),(0,0,380),(0,0,400),(0,0,420),(0,0,440),(0,0,460),(0,0,480),(0,20,0),(0,20,20),(0,20,40),(0,20,60),(0,20,80),(0,20,100),(0,20,120),(0,20,140),(0,20,160),(0,20,180),(0,20,200),(0,20,220),(0,20,240),(0,20,260),+31211 more]
  RadialDistance = 50
  Symmetry = 1
  TangentialDistance = 25
FEATURE [App::Part] Part
  Group = -> [Array,LV_Box]
  Origin = -> Origin002
  Placement = pos=(-240,-100,-240) rot=(0,0,1;0rad)
FEATURE [App::Part] worldVOL
  Group = -> [GDMLBox_WorldBox,Part]
  Origin = -> Origin
